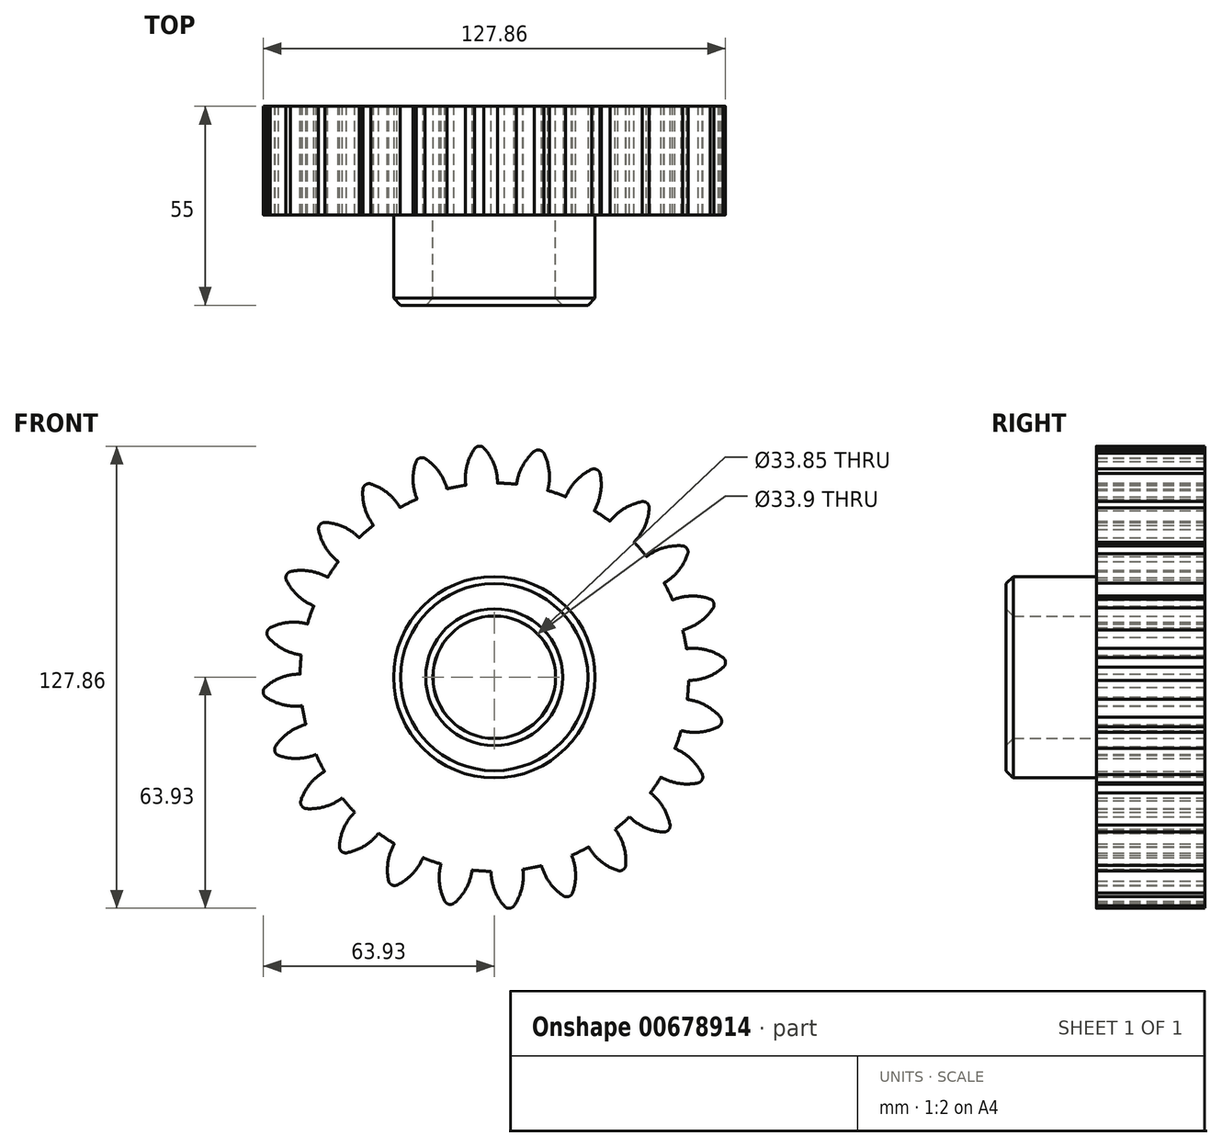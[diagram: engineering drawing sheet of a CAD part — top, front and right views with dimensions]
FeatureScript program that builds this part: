
annotation { "Feature Type Name" : "Feature", "Feature Type Description" : "" }
export const myFeature = defineFeature(function(context is Context, id is Id, definition is map)
    precondition{}
    {
        {
            var Q0;
            Q0=qCreatedBy(makeId("Front.planeOp"),FACE);
            var sketch = newSketch(context, id + "F0", { "sketchPlane" : qUnion([Q0])});
            skCircle(sketch, "E0", {"center": v(0, 0) * mm, "radius": 63.5 * mm, "construction": true});
            skCircle(sketch, "E1", {"center": v(0, 0) * mm, "radius": 58.67 * mm, "construction": true});
            skCircle(sketch, "E2", {"center": v(0, 0) * mm, "radius": 53.72 * mm});
            skLineSegment(sketch, "E3", {"start": v(0, 0) * mm, "end": v(0, 81.95) * mm, "construction": true});
            skLineSegment(sketch, "E4", {"start": v(0, 81.95) * mm, "end": v(0, 0) * mm, "construction": true});
            skLineSegment(sketch, "E5", {"start": v(0, 0) * mm, "end": v(-5.35, 81.6) * mm, "construction": true});
            skLineSegment(sketch, "E6", {"start": v(0, 58.67) * mm, "end": v(-69.28, 58.67) * mm, "construction": true});
            skLineSegment(sketch, "E7", {"start": v(0, 58.67) * mm, "end": v(-66.67, 34.4) * mm, "construction": true});
            skCircle(sketch, "E8", {"center": v(0, 0) * mm, "radius": 55.14 * mm, "construction": true});
            skCircle(sketch, "E9", {"center": v(0, 58.67) * mm, "radius": 14.6 * mm, "construction": true});
            skCircle(sketch, "E10", {"center": v(-13.72, 53.68) * mm, "radius": 14.6 * mm, "construction": true});
            skArc(sketch, "E11", {"start": v(0, 58.67) * mm, "mid": v(-1.2, 61.2) * mm, "end": v(-2.86, 63.44) * mm});
            skArc(sketch, "E12", {"start": v(0.88, 53.71) * mm, "mid": v(0.65, 56.23) * mm, "end": v(0, 58.67) * mm});
            skArc(sketch, "E13.MirrorCS", {"start": v(-7.66, 58.17) * mm, "mid": v(-6.8, 60.82) * mm, "end": v(-5.45, 63.27) * mm});
            skArc(sketch, "E14.MirrorCS", {"start": v(-7.88, 53.14) * mm, "mid": v(-7.99, 55.67) * mm, "end": v(-7.66, 58.17) * mm});
            skArc(sketch, "E15", {"start": v(-2.86, 63.44) * mm, "mid": v(-4.2, 63.93) * mm, "end": v(-5.45, 63.27) * mm});
            skPoint(sketch, "E16.0.midPoint", {"position": v(20.96, 6.95) * mm});
            skCircle(sketch, "E17", {"center": v(0, 0) * mm, "radius": 33.14 * mm});
            skPoint(sketch, "E18.0.midPoint", {"position": v(11.07, -7.08) * mm});
            skCircle(sketch, "E19", {"center": v(0, 0) * mm, "radius": 16.92 * mm});
            skSolve(sketch);
        }
        {
            var Q0;
            Q0=makeQuery(id+"F0.imprint","IMPRINT",FACE,{"disambiguationData":[TD([[makeQuery(id+"F0.imprint","IMPRINT",EDGE,{"derivedFrom":sQuery(id+"F0.wireOp",EDGE,"E17")}),-1.0]])]});
            var Q1;
            Q1=makeQuery(id+"F0.imprint","IMPRINT",FACE,{"disambiguationData":[TD([[makeQuery(id+"F0.imprint","IMPRINT",EDGE,{"derivedFrom":sQuery(id+"F0.wireOp",EDGE,"E17")}),1.0]])]});
            var Q2;
            Q2=makeQuery(id+"F0.imprint","IMPRINT",FACE,{"disambiguationData":[TD([[makeQuery(id+"F0.imprint","IMPRINT",EDGE,{"derivedFrom":sQuery(id+"F0.wireOp",EDGE,"E11")}),1.0]])]});
            extrude(context, id + "F1", {"entities" : qUnion([Q0, Q1, Q2]), "depth" : 30 * mm, "offsetDistance" : 25 * mm});
        }
        {
            var Q0;
            Q0=makeQuery(id+"F1.opExtrude","SWEPT_BODY",BODY,{"disambiguationData":[OSD([sQuery(id+"F0.wireOp",EDGE,"E2"),sQuery(id+"F0.wireOp",EDGE,"E11"),sQuery(id+"F0.wireOp",EDGE,"E12"),sQuery(id+"F0.wireOp",EDGE,"E13.MirrorCS"),sQuery(id+"F0.wireOp",EDGE,"E14.MirrorCS"),sQuery(id+"F0.wireOp",EDGE,"E15")])]});
            var Q1;
            Q1=makeQuery(id+"F1.opExtrude","SWEPT_FACE",FACE,{"disambiguationData":[OSD([sQuery(id+"F0.wireOp",EDGE,"E2")])]});
            circularPattern(context, id + "F2", {"operationType" : NewBodyOperationType.ADD, "entities" : qUnion([Q0]), "axis" : qUnion([Q1]), "angle" : 360 * degree, "instanceCount" : 24, "equalSpace" : true});
        }
        {
            var Q0;
            Q0=makeQuery(id+"F1.opExtrude","CAP_FACE",FACE,{"disambiguationData":[OSD([sQuery(id+"F0.wireOp",EDGE,"E2"),sQuery(id+"F0.wireOp",EDGE,"E11"),sQuery(id+"F0.wireOp",EDGE,"E12"),sQuery(id+"F0.wireOp",EDGE,"E13.MirrorCS"),sQuery(id+"F0.wireOp",EDGE,"E14.MirrorCS"),sQuery(id+"F0.wireOp",EDGE,"E15"),sQuery(id+"F0.wireOp",EDGE,"E16.0"),sQuery(id+"F0.wireOp",EDGE,"E16.1"),sQuery(id+"F0.wireOp",EDGE,"E16.2"),sQuery(id+"F0.wireOp",EDGE,"E16.3"),sQuery(id+"F0.wireOp",EDGE,"E16.4")])],"isStart":false});
            fillet(context, id + "F3", {"entities" : qUnion([Q0]), "radius" : 0.02 * mm, "tangentPropagation" : true, "allowEdgeOverflow" : false});
        }
        {
            var Q0;
            {var subQ0=makeQuery(id+"F1.opExtrude","CAP_FACE",FACE,{"disambiguationData":[OSD([sQuery(id+"F0.wireOp",EDGE,"E2"),sQuery(id+"F0.wireOp",EDGE,"E11"),sQuery(id+"F0.wireOp",EDGE,"E12"),sQuery(id+"F0.wireOp",EDGE,"E13.MirrorCS"),sQuery(id+"F0.wireOp",EDGE,"E14.MirrorCS"),sQuery(id+"F0.wireOp",EDGE,"E15"),sQuery(id+"F0.wireOp",EDGE,"E18.0"),sQuery(id+"F0.wireOp",EDGE,"E18.1"),sQuery(id+"F0.wireOp",EDGE,"E18.2"),sQuery(id+"F0.wireOp",EDGE,"E18.3"),sQuery(id+"F0.wireOp",EDGE,"E18.4"),sQuery(id+"F0.wireOp",EDGE,"E18.5")])],"isStart":false});Q0=makeQuery(id+"F2.boolean.opBoolean","MERGE",FACE,{"derivedFrom":[subQ0,makeQuery(id+"F2.opPattern","COPY",FACE,{"derivedFrom":subQ0,"instanceName":"1"}),makeQuery(id+"F2.opPattern","COPY",FACE,{"derivedFrom":subQ0,"instanceName":"2"}),makeQuery(id+"F2.opPattern","COPY",FACE,{"derivedFrom":subQ0,"instanceName":"3"}),makeQuery(id+"F2.opPattern","COPY",FACE,{"derivedFrom":subQ0,"instanceName":"4"}),makeQuery(id+"F2.opPattern","COPY",FACE,{"derivedFrom":subQ0,"instanceName":"5"}),makeQuery(id+"F2.opPattern","COPY",FACE,{"derivedFrom":subQ0,"instanceName":"6"}),makeQuery(id+"F2.opPattern","COPY",FACE,{"derivedFrom":subQ0,"instanceName":"7"}),makeQuery(id+"F2.opPattern","COPY",FACE,{"derivedFrom":subQ0,"instanceName":"8"}),makeQuery(id+"F2.opPattern","COPY",FACE,{"derivedFrom":subQ0,"instanceName":"9"}),makeQuery(id+"F2.opPattern","COPY",FACE,{"derivedFrom":subQ0,"instanceName":"10"}),makeQuery(id+"F2.opPattern","COPY",FACE,{"derivedFrom":subQ0,"instanceName":"11"}),makeQuery(id+"F2.opPattern","COPY",FACE,{"derivedFrom":subQ0,"instanceName":"12"}),makeQuery(id+"F2.opPattern","COPY",FACE,{"derivedFrom":subQ0,"instanceName":"13"}),makeQuery(id+"F2.opPattern","COPY",FACE,{"derivedFrom":subQ0,"instanceName":"14"}),makeQuery(id+"F2.opPattern","COPY",FACE,{"derivedFrom":subQ0,"instanceName":"15"}),makeQuery(id+"F2.opPattern","COPY",FACE,{"derivedFrom":subQ0,"instanceName":"16"}),makeQuery(id+"F2.opPattern","COPY",FACE,{"derivedFrom":subQ0,"instanceName":"17"}),makeQuery(id+"F2.opPattern","COPY",FACE,{"derivedFrom":subQ0,"instanceName":"18"}),makeQuery(id+"F2.opPattern","COPY",FACE,{"derivedFrom":subQ0,"instanceName":"19"}),makeQuery(id+"F2.opPattern","COPY",FACE,{"derivedFrom":subQ0,"instanceName":"20"}),makeQuery(id+"F2.opPattern","COPY",FACE,{"derivedFrom":subQ0,"instanceName":"21"}),makeQuery(id+"F2.opPattern","COPY",FACE,{"derivedFrom":subQ0,"instanceName":"22"}),makeQuery(id+"F2.opPattern","COPY",FACE,{"derivedFrom":subQ0,"instanceName":"23"})]});}
            var sketch = newSketch(context, id + "F4", { "sketchPlane" : qUnion([Q0])});
            skCircle(sketch, "E20", {"center": v(0, 0) * mm, "radius": 27.86 * mm});
            skSolve(sketch);
        }
        {
            var Q0;
            Q0=makeQuery(id+"F4.imprint","IMPRINT",FACE,{"disambiguationData":[TD([[makeQuery(id+"F4.imprint","IMPRINT",EDGE,{"derivedFrom":sQuery(id+"F4.wireOp",EDGE,"E20")}),1.0]])]});
            extrude(context, id + "F5", {"entities" : qUnion([Q0]), "operationType" : NewBodyOperationType.ADD, "depth" : 25 * mm, "offsetDistance" : 25 * mm});
        }
        {
            var Q0;
            Q0=makeQuery(id+"F5.opExtrude","CAP_EDGE",EDGE,{"disambiguationData":[OSD([sQuery(id+"F4.wireOp",EDGE,"E20")])],"isStart":false});
            var Q1;
            Q1=makeQuery(id+"F5.opExtrude","CAP_EDGE",EDGE,{"disambiguationData":[OSD([sQuery(id+"F0.wireOp",EDGE,"E2"),sQuery(id+"F0.wireOp",EDGE,"E11"),sQuery(id+"F0.wireOp",EDGE,"E12"),sQuery(id+"F0.wireOp",EDGE,"E13.MirrorCS"),sQuery(id+"F0.wireOp",EDGE,"E14.MirrorCS"),sQuery(id+"F0.wireOp",EDGE,"E15"),sQuery(id+"F0.wireOp",EDGE,"E19")])],"isStart":false});
            var Q2;
            {var subQ0=sQuery(id+"F0.wireOp",EDGE,"E14.MirrorCS");var subQ1=makeQuery(id+"F1.opExtrude","CAP_FACE",FACE,{"disambiguationData":[OSD([sQuery(id+"F0.wireOp",EDGE,"E2"),sQuery(id+"F0.wireOp",EDGE,"E11"),sQuery(id+"F0.wireOp",EDGE,"E12"),sQuery(id+"F0.wireOp",EDGE,"E13.MirrorCS"),subQ0,sQuery(id+"F0.wireOp",EDGE,"E15"),sQuery(id+"F0.wireOp",EDGE,"E19")])],"isStart":false});Q2=makeQuery(id+"F3.opFillet","BLEND_EDGE",EDGE,{"blendedFrom":[makeQuery(id+"F1.opExtrude","CAP_EDGE",EDGE,{"disambiguationData":[OSD([subQ0])],"isStart":false}),makeQuery(id+"F2.boolean.opBoolean","MERGE",FACE,{"derivedFrom":[subQ1,makeQuery(id+"F2.opPattern","COPY",FACE,{"derivedFrom":subQ1,"instanceName":"1"}),makeQuery(id+"F2.opPattern","COPY",FACE,{"derivedFrom":subQ1,"instanceName":"2"}),makeQuery(id+"F2.opPattern","COPY",FACE,{"derivedFrom":subQ1,"instanceName":"3"}),makeQuery(id+"F2.opPattern","COPY",FACE,{"derivedFrom":subQ1,"instanceName":"4"}),makeQuery(id+"F2.opPattern","COPY",FACE,{"derivedFrom":subQ1,"instanceName":"5"}),makeQuery(id+"F2.opPattern","COPY",FACE,{"derivedFrom":subQ1,"instanceName":"6"}),makeQuery(id+"F2.opPattern","COPY",FACE,{"derivedFrom":subQ1,"instanceName":"7"}),makeQuery(id+"F2.opPattern","COPY",FACE,{"derivedFrom":subQ1,"instanceName":"8"}),makeQuery(id+"F2.opPattern","COPY",FACE,{"derivedFrom":subQ1,"instanceName":"9"}),makeQuery(id+"F2.opPattern","COPY",FACE,{"derivedFrom":subQ1,"instanceName":"10"}),makeQuery(id+"F2.opPattern","COPY",FACE,{"derivedFrom":subQ1,"instanceName":"11"}),makeQuery(id+"F2.opPattern","COPY",FACE,{"derivedFrom":subQ1,"instanceName":"12"}),makeQuery(id+"F2.opPattern","COPY",FACE,{"derivedFrom":subQ1,"instanceName":"13"}),makeQuery(id+"F2.opPattern","COPY",FACE,{"derivedFrom":subQ1,"instanceName":"14"}),makeQuery(id+"F2.opPattern","COPY",FACE,{"derivedFrom":subQ1,"instanceName":"15"}),makeQuery(id+"F2.opPattern","COPY",FACE,{"derivedFrom":subQ1,"instanceName":"16"}),makeQuery(id+"F2.opPattern","COPY",FACE,{"derivedFrom":subQ1,"instanceName":"17"}),makeQuery(id+"F2.opPattern","COPY",FACE,{"derivedFrom":subQ1,"instanceName":"18"}),makeQuery(id+"F2.opPattern","COPY",FACE,{"derivedFrom":subQ1,"instanceName":"19"}),makeQuery(id+"F2.opPattern","COPY",FACE,{"derivedFrom":subQ1,"instanceName":"20"}),makeQuery(id+"F2.opPattern","COPY",FACE,{"derivedFrom":subQ1,"instanceName":"21"}),makeQuery(id+"F2.opPattern","COPY",FACE,{"derivedFrom":subQ1,"instanceName":"22"}),makeQuery(id+"F2.opPattern","COPY",FACE,{"derivedFrom":subQ1,"instanceName":"23"})]})],"blendedInto":[makeQuery(id+"F2.boolean.opBoolean","MERGE",FACE,{"derivedFrom":[subQ1,makeQuery(id+"F2.opPattern","COPY",FACE,{"derivedFrom":subQ1,"instanceName":"1"}),makeQuery(id+"F2.opPattern","COPY",FACE,{"derivedFrom":subQ1,"instanceName":"2"}),makeQuery(id+"F2.opPattern","COPY",FACE,{"derivedFrom":subQ1,"instanceName":"3"}),makeQuery(id+"F2.opPattern","COPY",FACE,{"derivedFrom":subQ1,"instanceName":"4"}),makeQuery(id+"F2.opPattern","COPY",FACE,{"derivedFrom":subQ1,"instanceName":"5"}),makeQuery(id+"F2.opPattern","COPY",FACE,{"derivedFrom":subQ1,"instanceName":"6"}),makeQuery(id+"F2.opPattern","COPY",FACE,{"derivedFrom":subQ1,"instanceName":"7"}),makeQuery(id+"F2.opPattern","COPY",FACE,{"derivedFrom":subQ1,"instanceName":"8"}),makeQuery(id+"F2.opPattern","COPY",FACE,{"derivedFrom":subQ1,"instanceName":"9"}),makeQuery(id+"F2.opPattern","COPY",FACE,{"derivedFrom":subQ1,"instanceName":"10"}),makeQuery(id+"F2.opPattern","COPY",FACE,{"derivedFrom":subQ1,"instanceName":"11"}),makeQuery(id+"F2.opPattern","COPY",FACE,{"derivedFrom":subQ1,"instanceName":"12"}),makeQuery(id+"F2.opPattern","COPY",FACE,{"derivedFrom":subQ1,"instanceName":"13"}),makeQuery(id+"F2.opPattern","COPY",FACE,{"derivedFrom":subQ1,"instanceName":"14"}),makeQuery(id+"F2.opPattern","COPY",FACE,{"derivedFrom":subQ1,"instanceName":"15"}),makeQuery(id+"F2.opPattern","COPY",FACE,{"derivedFrom":subQ1,"instanceName":"16"}),makeQuery(id+"F2.opPattern","COPY",FACE,{"derivedFrom":subQ1,"instanceName":"17"}),makeQuery(id+"F2.opPattern","COPY",FACE,{"derivedFrom":subQ1,"instanceName":"18"}),makeQuery(id+"F2.opPattern","COPY",FACE,{"derivedFrom":subQ1,"instanceName":"19"}),makeQuery(id+"F2.opPattern","COPY",FACE,{"derivedFrom":subQ1,"instanceName":"20"}),makeQuery(id+"F2.opPattern","COPY",FACE,{"derivedFrom":subQ1,"instanceName":"21"}),makeQuery(id+"F2.opPattern","COPY",FACE,{"derivedFrom":subQ1,"instanceName":"22"}),makeQuery(id+"F2.opPattern","COPY",FACE,{"derivedFrom":subQ1,"instanceName":"23"})]})]});}
            var Q3;
            {var subQ0=sQuery(id+"F0.wireOp",EDGE,"E12");var subQ1=makeQuery(id+"F1.opExtrude","CAP_FACE",FACE,{"disambiguationData":[OSD([sQuery(id+"F0.wireOp",EDGE,"E2"),sQuery(id+"F0.wireOp",EDGE,"E11"),subQ0,sQuery(id+"F0.wireOp",EDGE,"E13.MirrorCS"),sQuery(id+"F0.wireOp",EDGE,"E14.MirrorCS"),sQuery(id+"F0.wireOp",EDGE,"E15"),sQuery(id+"F0.wireOp",EDGE,"E19")])],"isStart":false});Q3=makeQuery(id+"F3.opFillet","BLEND_EDGE",EDGE,{"blendedFrom":[makeQuery(id+"F1.opExtrude","CAP_EDGE",EDGE,{"disambiguationData":[OSD([subQ0])],"isStart":false}),makeQuery(id+"F2.boolean.opBoolean","MERGE",FACE,{"derivedFrom":[subQ1,makeQuery(id+"F2.opPattern","COPY",FACE,{"derivedFrom":subQ1,"instanceName":"1"}),makeQuery(id+"F2.opPattern","COPY",FACE,{"derivedFrom":subQ1,"instanceName":"2"}),makeQuery(id+"F2.opPattern","COPY",FACE,{"derivedFrom":subQ1,"instanceName":"3"}),makeQuery(id+"F2.opPattern","COPY",FACE,{"derivedFrom":subQ1,"instanceName":"4"}),makeQuery(id+"F2.opPattern","COPY",FACE,{"derivedFrom":subQ1,"instanceName":"5"}),makeQuery(id+"F2.opPattern","COPY",FACE,{"derivedFrom":subQ1,"instanceName":"6"}),makeQuery(id+"F2.opPattern","COPY",FACE,{"derivedFrom":subQ1,"instanceName":"7"}),makeQuery(id+"F2.opPattern","COPY",FACE,{"derivedFrom":subQ1,"instanceName":"8"}),makeQuery(id+"F2.opPattern","COPY",FACE,{"derivedFrom":subQ1,"instanceName":"9"}),makeQuery(id+"F2.opPattern","COPY",FACE,{"derivedFrom":subQ1,"instanceName":"10"}),makeQuery(id+"F2.opPattern","COPY",FACE,{"derivedFrom":subQ1,"instanceName":"11"}),makeQuery(id+"F2.opPattern","COPY",FACE,{"derivedFrom":subQ1,"instanceName":"12"}),makeQuery(id+"F2.opPattern","COPY",FACE,{"derivedFrom":subQ1,"instanceName":"13"}),makeQuery(id+"F2.opPattern","COPY",FACE,{"derivedFrom":subQ1,"instanceName":"14"}),makeQuery(id+"F2.opPattern","COPY",FACE,{"derivedFrom":subQ1,"instanceName":"15"}),makeQuery(id+"F2.opPattern","COPY",FACE,{"derivedFrom":subQ1,"instanceName":"16"}),makeQuery(id+"F2.opPattern","COPY",FACE,{"derivedFrom":subQ1,"instanceName":"17"}),makeQuery(id+"F2.opPattern","COPY",FACE,{"derivedFrom":subQ1,"instanceName":"18"}),makeQuery(id+"F2.opPattern","COPY",FACE,{"derivedFrom":subQ1,"instanceName":"19"}),makeQuery(id+"F2.opPattern","COPY",FACE,{"derivedFrom":subQ1,"instanceName":"20"}),makeQuery(id+"F2.opPattern","COPY",FACE,{"derivedFrom":subQ1,"instanceName":"21"}),makeQuery(id+"F2.opPattern","COPY",FACE,{"derivedFrom":subQ1,"instanceName":"22"}),makeQuery(id+"F2.opPattern","COPY",FACE,{"derivedFrom":subQ1,"instanceName":"23"})]})],"blendedInto":[makeQuery(id+"F2.boolean.opBoolean","MERGE",FACE,{"derivedFrom":[subQ1,makeQuery(id+"F2.opPattern","COPY",FACE,{"derivedFrom":subQ1,"instanceName":"1"}),makeQuery(id+"F2.opPattern","COPY",FACE,{"derivedFrom":subQ1,"instanceName":"2"}),makeQuery(id+"F2.opPattern","COPY",FACE,{"derivedFrom":subQ1,"instanceName":"3"}),makeQuery(id+"F2.opPattern","COPY",FACE,{"derivedFrom":subQ1,"instanceName":"4"}),makeQuery(id+"F2.opPattern","COPY",FACE,{"derivedFrom":subQ1,"instanceName":"5"}),makeQuery(id+"F2.opPattern","COPY",FACE,{"derivedFrom":subQ1,"instanceName":"6"}),makeQuery(id+"F2.opPattern","COPY",FACE,{"derivedFrom":subQ1,"instanceName":"7"}),makeQuery(id+"F2.opPattern","COPY",FACE,{"derivedFrom":subQ1,"instanceName":"8"}),makeQuery(id+"F2.opPattern","COPY",FACE,{"derivedFrom":subQ1,"instanceName":"9"}),makeQuery(id+"F2.opPattern","COPY",FACE,{"derivedFrom":subQ1,"instanceName":"10"}),makeQuery(id+"F2.opPattern","COPY",FACE,{"derivedFrom":subQ1,"instanceName":"11"}),makeQuery(id+"F2.opPattern","COPY",FACE,{"derivedFrom":subQ1,"instanceName":"12"}),makeQuery(id+"F2.opPattern","COPY",FACE,{"derivedFrom":subQ1,"instanceName":"13"}),makeQuery(id+"F2.opPattern","COPY",FACE,{"derivedFrom":subQ1,"instanceName":"14"}),makeQuery(id+"F2.opPattern","COPY",FACE,{"derivedFrom":subQ1,"instanceName":"15"}),makeQuery(id+"F2.opPattern","COPY",FACE,{"derivedFrom":subQ1,"instanceName":"16"}),makeQuery(id+"F2.opPattern","COPY",FACE,{"derivedFrom":subQ1,"instanceName":"17"}),makeQuery(id+"F2.opPattern","COPY",FACE,{"derivedFrom":subQ1,"instanceName":"18"}),makeQuery(id+"F2.opPattern","COPY",FACE,{"derivedFrom":subQ1,"instanceName":"19"}),makeQuery(id+"F2.opPattern","COPY",FACE,{"derivedFrom":subQ1,"instanceName":"20"}),makeQuery(id+"F2.opPattern","COPY",FACE,{"derivedFrom":subQ1,"instanceName":"21"}),makeQuery(id+"F2.opPattern","COPY",FACE,{"derivedFrom":subQ1,"instanceName":"22"}),makeQuery(id+"F2.opPattern","COPY",FACE,{"derivedFrom":subQ1,"instanceName":"23"})]})]});}
            var Q4;
            {var subQ0=sQuery(id+"F0.wireOp",EDGE,"E14.MirrorCS");var subQ1=makeQuery(id+"F1.opExtrude","CAP_FACE",FACE,{"disambiguationData":[OSD([sQuery(id+"F0.wireOp",EDGE,"E2"),sQuery(id+"F0.wireOp",EDGE,"E11"),sQuery(id+"F0.wireOp",EDGE,"E12"),sQuery(id+"F0.wireOp",EDGE,"E13.MirrorCS"),subQ0,sQuery(id+"F0.wireOp",EDGE,"E15"),sQuery(id+"F0.wireOp",EDGE,"E19")])],"isStart":false});Q4=makeQuery(id+"F3.opFillet","BLEND_EDGE",EDGE,{"blendedFrom":[makeQuery(id+"F2.opPattern","COPY",EDGE,{"derivedFrom":makeQuery(id+"F1.opExtrude","CAP_EDGE",EDGE,{"disambiguationData":[OSD([subQ0])],"isStart":false}),"instanceName":"1"}),makeQuery(id+"F2.boolean.opBoolean","MERGE",FACE,{"derivedFrom":[subQ1,makeQuery(id+"F2.opPattern","COPY",FACE,{"derivedFrom":subQ1,"instanceName":"1"}),makeQuery(id+"F2.opPattern","COPY",FACE,{"derivedFrom":subQ1,"instanceName":"2"}),makeQuery(id+"F2.opPattern","COPY",FACE,{"derivedFrom":subQ1,"instanceName":"3"}),makeQuery(id+"F2.opPattern","COPY",FACE,{"derivedFrom":subQ1,"instanceName":"4"}),makeQuery(id+"F2.opPattern","COPY",FACE,{"derivedFrom":subQ1,"instanceName":"5"}),makeQuery(id+"F2.opPattern","COPY",FACE,{"derivedFrom":subQ1,"instanceName":"6"}),makeQuery(id+"F2.opPattern","COPY",FACE,{"derivedFrom":subQ1,"instanceName":"7"}),makeQuery(id+"F2.opPattern","COPY",FACE,{"derivedFrom":subQ1,"instanceName":"8"}),makeQuery(id+"F2.opPattern","COPY",FACE,{"derivedFrom":subQ1,"instanceName":"9"}),makeQuery(id+"F2.opPattern","COPY",FACE,{"derivedFrom":subQ1,"instanceName":"10"}),makeQuery(id+"F2.opPattern","COPY",FACE,{"derivedFrom":subQ1,"instanceName":"11"}),makeQuery(id+"F2.opPattern","COPY",FACE,{"derivedFrom":subQ1,"instanceName":"12"}),makeQuery(id+"F2.opPattern","COPY",FACE,{"derivedFrom":subQ1,"instanceName":"13"}),makeQuery(id+"F2.opPattern","COPY",FACE,{"derivedFrom":subQ1,"instanceName":"14"}),makeQuery(id+"F2.opPattern","COPY",FACE,{"derivedFrom":subQ1,"instanceName":"15"}),makeQuery(id+"F2.opPattern","COPY",FACE,{"derivedFrom":subQ1,"instanceName":"16"}),makeQuery(id+"F2.opPattern","COPY",FACE,{"derivedFrom":subQ1,"instanceName":"17"}),makeQuery(id+"F2.opPattern","COPY",FACE,{"derivedFrom":subQ1,"instanceName":"18"}),makeQuery(id+"F2.opPattern","COPY",FACE,{"derivedFrom":subQ1,"instanceName":"19"}),makeQuery(id+"F2.opPattern","COPY",FACE,{"derivedFrom":subQ1,"instanceName":"20"}),makeQuery(id+"F2.opPattern","COPY",FACE,{"derivedFrom":subQ1,"instanceName":"21"}),makeQuery(id+"F2.opPattern","COPY",FACE,{"derivedFrom":subQ1,"instanceName":"22"}),makeQuery(id+"F2.opPattern","COPY",FACE,{"derivedFrom":subQ1,"instanceName":"23"})]})],"blendedInto":[makeQuery(id+"F2.boolean.opBoolean","MERGE",FACE,{"derivedFrom":[subQ1,makeQuery(id+"F2.opPattern","COPY",FACE,{"derivedFrom":subQ1,"instanceName":"1"}),makeQuery(id+"F2.opPattern","COPY",FACE,{"derivedFrom":subQ1,"instanceName":"2"}),makeQuery(id+"F2.opPattern","COPY",FACE,{"derivedFrom":subQ1,"instanceName":"3"}),makeQuery(id+"F2.opPattern","COPY",FACE,{"derivedFrom":subQ1,"instanceName":"4"}),makeQuery(id+"F2.opPattern","COPY",FACE,{"derivedFrom":subQ1,"instanceName":"5"}),makeQuery(id+"F2.opPattern","COPY",FACE,{"derivedFrom":subQ1,"instanceName":"6"}),makeQuery(id+"F2.opPattern","COPY",FACE,{"derivedFrom":subQ1,"instanceName":"7"}),makeQuery(id+"F2.opPattern","COPY",FACE,{"derivedFrom":subQ1,"instanceName":"8"}),makeQuery(id+"F2.opPattern","COPY",FACE,{"derivedFrom":subQ1,"instanceName":"9"}),makeQuery(id+"F2.opPattern","COPY",FACE,{"derivedFrom":subQ1,"instanceName":"10"}),makeQuery(id+"F2.opPattern","COPY",FACE,{"derivedFrom":subQ1,"instanceName":"11"}),makeQuery(id+"F2.opPattern","COPY",FACE,{"derivedFrom":subQ1,"instanceName":"12"}),makeQuery(id+"F2.opPattern","COPY",FACE,{"derivedFrom":subQ1,"instanceName":"13"}),makeQuery(id+"F2.opPattern","COPY",FACE,{"derivedFrom":subQ1,"instanceName":"14"}),makeQuery(id+"F2.opPattern","COPY",FACE,{"derivedFrom":subQ1,"instanceName":"15"}),makeQuery(id+"F2.opPattern","COPY",FACE,{"derivedFrom":subQ1,"instanceName":"16"}),makeQuery(id+"F2.opPattern","COPY",FACE,{"derivedFrom":subQ1,"instanceName":"17"}),makeQuery(id+"F2.opPattern","COPY",FACE,{"derivedFrom":subQ1,"instanceName":"18"}),makeQuery(id+"F2.opPattern","COPY",FACE,{"derivedFrom":subQ1,"instanceName":"19"}),makeQuery(id+"F2.opPattern","COPY",FACE,{"derivedFrom":subQ1,"instanceName":"20"}),makeQuery(id+"F2.opPattern","COPY",FACE,{"derivedFrom":subQ1,"instanceName":"21"}),makeQuery(id+"F2.opPattern","COPY",FACE,{"derivedFrom":subQ1,"instanceName":"22"}),makeQuery(id+"F2.opPattern","COPY",FACE,{"derivedFrom":subQ1,"instanceName":"23"})]})]});}
            var Q5;
            {var subQ0=sQuery(id+"F0.wireOp",EDGE,"E12");var subQ1=makeQuery(id+"F1.opExtrude","CAP_FACE",FACE,{"disambiguationData":[OSD([sQuery(id+"F0.wireOp",EDGE,"E2"),sQuery(id+"F0.wireOp",EDGE,"E11"),subQ0,sQuery(id+"F0.wireOp",EDGE,"E13.MirrorCS"),sQuery(id+"F0.wireOp",EDGE,"E14.MirrorCS"),sQuery(id+"F0.wireOp",EDGE,"E15"),sQuery(id+"F0.wireOp",EDGE,"E19")])],"isStart":false});Q5=makeQuery(id+"F3.opFillet","BLEND_EDGE",EDGE,{"blendedFrom":[makeQuery(id+"F2.opPattern","COPY",EDGE,{"derivedFrom":makeQuery(id+"F1.opExtrude","CAP_EDGE",EDGE,{"disambiguationData":[OSD([subQ0])],"isStart":false}),"instanceName":"1"}),makeQuery(id+"F2.boolean.opBoolean","MERGE",FACE,{"derivedFrom":[subQ1,makeQuery(id+"F2.opPattern","COPY",FACE,{"derivedFrom":subQ1,"instanceName":"1"}),makeQuery(id+"F2.opPattern","COPY",FACE,{"derivedFrom":subQ1,"instanceName":"2"}),makeQuery(id+"F2.opPattern","COPY",FACE,{"derivedFrom":subQ1,"instanceName":"3"}),makeQuery(id+"F2.opPattern","COPY",FACE,{"derivedFrom":subQ1,"instanceName":"4"}),makeQuery(id+"F2.opPattern","COPY",FACE,{"derivedFrom":subQ1,"instanceName":"5"}),makeQuery(id+"F2.opPattern","COPY",FACE,{"derivedFrom":subQ1,"instanceName":"6"}),makeQuery(id+"F2.opPattern","COPY",FACE,{"derivedFrom":subQ1,"instanceName":"7"}),makeQuery(id+"F2.opPattern","COPY",FACE,{"derivedFrom":subQ1,"instanceName":"8"}),makeQuery(id+"F2.opPattern","COPY",FACE,{"derivedFrom":subQ1,"instanceName":"9"}),makeQuery(id+"F2.opPattern","COPY",FACE,{"derivedFrom":subQ1,"instanceName":"10"}),makeQuery(id+"F2.opPattern","COPY",FACE,{"derivedFrom":subQ1,"instanceName":"11"}),makeQuery(id+"F2.opPattern","COPY",FACE,{"derivedFrom":subQ1,"instanceName":"12"}),makeQuery(id+"F2.opPattern","COPY",FACE,{"derivedFrom":subQ1,"instanceName":"13"}),makeQuery(id+"F2.opPattern","COPY",FACE,{"derivedFrom":subQ1,"instanceName":"14"}),makeQuery(id+"F2.opPattern","COPY",FACE,{"derivedFrom":subQ1,"instanceName":"15"}),makeQuery(id+"F2.opPattern","COPY",FACE,{"derivedFrom":subQ1,"instanceName":"16"}),makeQuery(id+"F2.opPattern","COPY",FACE,{"derivedFrom":subQ1,"instanceName":"17"}),makeQuery(id+"F2.opPattern","COPY",FACE,{"derivedFrom":subQ1,"instanceName":"18"}),makeQuery(id+"F2.opPattern","COPY",FACE,{"derivedFrom":subQ1,"instanceName":"19"}),makeQuery(id+"F2.opPattern","COPY",FACE,{"derivedFrom":subQ1,"instanceName":"20"}),makeQuery(id+"F2.opPattern","COPY",FACE,{"derivedFrom":subQ1,"instanceName":"21"}),makeQuery(id+"F2.opPattern","COPY",FACE,{"derivedFrom":subQ1,"instanceName":"22"}),makeQuery(id+"F2.opPattern","COPY",FACE,{"derivedFrom":subQ1,"instanceName":"23"})]})],"blendedInto":[makeQuery(id+"F2.boolean.opBoolean","MERGE",FACE,{"derivedFrom":[subQ1,makeQuery(id+"F2.opPattern","COPY",FACE,{"derivedFrom":subQ1,"instanceName":"1"}),makeQuery(id+"F2.opPattern","COPY",FACE,{"derivedFrom":subQ1,"instanceName":"2"}),makeQuery(id+"F2.opPattern","COPY",FACE,{"derivedFrom":subQ1,"instanceName":"3"}),makeQuery(id+"F2.opPattern","COPY",FACE,{"derivedFrom":subQ1,"instanceName":"4"}),makeQuery(id+"F2.opPattern","COPY",FACE,{"derivedFrom":subQ1,"instanceName":"5"}),makeQuery(id+"F2.opPattern","COPY",FACE,{"derivedFrom":subQ1,"instanceName":"6"}),makeQuery(id+"F2.opPattern","COPY",FACE,{"derivedFrom":subQ1,"instanceName":"7"}),makeQuery(id+"F2.opPattern","COPY",FACE,{"derivedFrom":subQ1,"instanceName":"8"}),makeQuery(id+"F2.opPattern","COPY",FACE,{"derivedFrom":subQ1,"instanceName":"9"}),makeQuery(id+"F2.opPattern","COPY",FACE,{"derivedFrom":subQ1,"instanceName":"10"}),makeQuery(id+"F2.opPattern","COPY",FACE,{"derivedFrom":subQ1,"instanceName":"11"}),makeQuery(id+"F2.opPattern","COPY",FACE,{"derivedFrom":subQ1,"instanceName":"12"}),makeQuery(id+"F2.opPattern","COPY",FACE,{"derivedFrom":subQ1,"instanceName":"13"}),makeQuery(id+"F2.opPattern","COPY",FACE,{"derivedFrom":subQ1,"instanceName":"14"}),makeQuery(id+"F2.opPattern","COPY",FACE,{"derivedFrom":subQ1,"instanceName":"15"}),makeQuery(id+"F2.opPattern","COPY",FACE,{"derivedFrom":subQ1,"instanceName":"16"}),makeQuery(id+"F2.opPattern","COPY",FACE,{"derivedFrom":subQ1,"instanceName":"17"}),makeQuery(id+"F2.opPattern","COPY",FACE,{"derivedFrom":subQ1,"instanceName":"18"}),makeQuery(id+"F2.opPattern","COPY",FACE,{"derivedFrom":subQ1,"instanceName":"19"}),makeQuery(id+"F2.opPattern","COPY",FACE,{"derivedFrom":subQ1,"instanceName":"20"}),makeQuery(id+"F2.opPattern","COPY",FACE,{"derivedFrom":subQ1,"instanceName":"21"}),makeQuery(id+"F2.opPattern","COPY",FACE,{"derivedFrom":subQ1,"instanceName":"22"}),makeQuery(id+"F2.opPattern","COPY",FACE,{"derivedFrom":subQ1,"instanceName":"23"})]})]});}
            var Q6;
            {var subQ0=sQuery(id+"F0.wireOp",EDGE,"E14.MirrorCS");var subQ1=makeQuery(id+"F1.opExtrude","CAP_FACE",FACE,{"disambiguationData":[OSD([sQuery(id+"F0.wireOp",EDGE,"E2"),sQuery(id+"F0.wireOp",EDGE,"E11"),sQuery(id+"F0.wireOp",EDGE,"E12"),sQuery(id+"F0.wireOp",EDGE,"E13.MirrorCS"),subQ0,sQuery(id+"F0.wireOp",EDGE,"E15"),sQuery(id+"F0.wireOp",EDGE,"E19")])],"isStart":false});Q6=makeQuery(id+"F3.opFillet","BLEND_EDGE",EDGE,{"blendedFrom":[makeQuery(id+"F2.opPattern","COPY",EDGE,{"derivedFrom":makeQuery(id+"F1.opExtrude","CAP_EDGE",EDGE,{"disambiguationData":[OSD([subQ0])],"isStart":false}),"instanceName":"2"}),makeQuery(id+"F2.boolean.opBoolean","MERGE",FACE,{"derivedFrom":[subQ1,makeQuery(id+"F2.opPattern","COPY",FACE,{"derivedFrom":subQ1,"instanceName":"1"}),makeQuery(id+"F2.opPattern","COPY",FACE,{"derivedFrom":subQ1,"instanceName":"2"}),makeQuery(id+"F2.opPattern","COPY",FACE,{"derivedFrom":subQ1,"instanceName":"3"}),makeQuery(id+"F2.opPattern","COPY",FACE,{"derivedFrom":subQ1,"instanceName":"4"}),makeQuery(id+"F2.opPattern","COPY",FACE,{"derivedFrom":subQ1,"instanceName":"5"}),makeQuery(id+"F2.opPattern","COPY",FACE,{"derivedFrom":subQ1,"instanceName":"6"}),makeQuery(id+"F2.opPattern","COPY",FACE,{"derivedFrom":subQ1,"instanceName":"7"}),makeQuery(id+"F2.opPattern","COPY",FACE,{"derivedFrom":subQ1,"instanceName":"8"}),makeQuery(id+"F2.opPattern","COPY",FACE,{"derivedFrom":subQ1,"instanceName":"9"}),makeQuery(id+"F2.opPattern","COPY",FACE,{"derivedFrom":subQ1,"instanceName":"10"}),makeQuery(id+"F2.opPattern","COPY",FACE,{"derivedFrom":subQ1,"instanceName":"11"}),makeQuery(id+"F2.opPattern","COPY",FACE,{"derivedFrom":subQ1,"instanceName":"12"}),makeQuery(id+"F2.opPattern","COPY",FACE,{"derivedFrom":subQ1,"instanceName":"13"}),makeQuery(id+"F2.opPattern","COPY",FACE,{"derivedFrom":subQ1,"instanceName":"14"}),makeQuery(id+"F2.opPattern","COPY",FACE,{"derivedFrom":subQ1,"instanceName":"15"}),makeQuery(id+"F2.opPattern","COPY",FACE,{"derivedFrom":subQ1,"instanceName":"16"}),makeQuery(id+"F2.opPattern","COPY",FACE,{"derivedFrom":subQ1,"instanceName":"17"}),makeQuery(id+"F2.opPattern","COPY",FACE,{"derivedFrom":subQ1,"instanceName":"18"}),makeQuery(id+"F2.opPattern","COPY",FACE,{"derivedFrom":subQ1,"instanceName":"19"}),makeQuery(id+"F2.opPattern","COPY",FACE,{"derivedFrom":subQ1,"instanceName":"20"}),makeQuery(id+"F2.opPattern","COPY",FACE,{"derivedFrom":subQ1,"instanceName":"21"}),makeQuery(id+"F2.opPattern","COPY",FACE,{"derivedFrom":subQ1,"instanceName":"22"}),makeQuery(id+"F2.opPattern","COPY",FACE,{"derivedFrom":subQ1,"instanceName":"23"})]})],"blendedInto":[makeQuery(id+"F2.boolean.opBoolean","MERGE",FACE,{"derivedFrom":[subQ1,makeQuery(id+"F2.opPattern","COPY",FACE,{"derivedFrom":subQ1,"instanceName":"1"}),makeQuery(id+"F2.opPattern","COPY",FACE,{"derivedFrom":subQ1,"instanceName":"2"}),makeQuery(id+"F2.opPattern","COPY",FACE,{"derivedFrom":subQ1,"instanceName":"3"}),makeQuery(id+"F2.opPattern","COPY",FACE,{"derivedFrom":subQ1,"instanceName":"4"}),makeQuery(id+"F2.opPattern","COPY",FACE,{"derivedFrom":subQ1,"instanceName":"5"}),makeQuery(id+"F2.opPattern","COPY",FACE,{"derivedFrom":subQ1,"instanceName":"6"}),makeQuery(id+"F2.opPattern","COPY",FACE,{"derivedFrom":subQ1,"instanceName":"7"}),makeQuery(id+"F2.opPattern","COPY",FACE,{"derivedFrom":subQ1,"instanceName":"8"}),makeQuery(id+"F2.opPattern","COPY",FACE,{"derivedFrom":subQ1,"instanceName":"9"}),makeQuery(id+"F2.opPattern","COPY",FACE,{"derivedFrom":subQ1,"instanceName":"10"}),makeQuery(id+"F2.opPattern","COPY",FACE,{"derivedFrom":subQ1,"instanceName":"11"}),makeQuery(id+"F2.opPattern","COPY",FACE,{"derivedFrom":subQ1,"instanceName":"12"}),makeQuery(id+"F2.opPattern","COPY",FACE,{"derivedFrom":subQ1,"instanceName":"13"}),makeQuery(id+"F2.opPattern","COPY",FACE,{"derivedFrom":subQ1,"instanceName":"14"}),makeQuery(id+"F2.opPattern","COPY",FACE,{"derivedFrom":subQ1,"instanceName":"15"}),makeQuery(id+"F2.opPattern","COPY",FACE,{"derivedFrom":subQ1,"instanceName":"16"}),makeQuery(id+"F2.opPattern","COPY",FACE,{"derivedFrom":subQ1,"instanceName":"17"}),makeQuery(id+"F2.opPattern","COPY",FACE,{"derivedFrom":subQ1,"instanceName":"18"}),makeQuery(id+"F2.opPattern","COPY",FACE,{"derivedFrom":subQ1,"instanceName":"19"}),makeQuery(id+"F2.opPattern","COPY",FACE,{"derivedFrom":subQ1,"instanceName":"20"}),makeQuery(id+"F2.opPattern","COPY",FACE,{"derivedFrom":subQ1,"instanceName":"21"}),makeQuery(id+"F2.opPattern","COPY",FACE,{"derivedFrom":subQ1,"instanceName":"22"}),makeQuery(id+"F2.opPattern","COPY",FACE,{"derivedFrom":subQ1,"instanceName":"23"})]})]});}
            var Q7;
            {var subQ0=sQuery(id+"F0.wireOp",EDGE,"E12");var subQ1=makeQuery(id+"F1.opExtrude","CAP_FACE",FACE,{"disambiguationData":[OSD([sQuery(id+"F0.wireOp",EDGE,"E2"),sQuery(id+"F0.wireOp",EDGE,"E11"),subQ0,sQuery(id+"F0.wireOp",EDGE,"E13.MirrorCS"),sQuery(id+"F0.wireOp",EDGE,"E14.MirrorCS"),sQuery(id+"F0.wireOp",EDGE,"E15"),sQuery(id+"F0.wireOp",EDGE,"E19")])],"isStart":false});Q7=makeQuery(id+"F3.opFillet","BLEND_EDGE",EDGE,{"blendedFrom":[makeQuery(id+"F2.opPattern","COPY",EDGE,{"derivedFrom":makeQuery(id+"F1.opExtrude","CAP_EDGE",EDGE,{"disambiguationData":[OSD([subQ0])],"isStart":false}),"instanceName":"2"}),makeQuery(id+"F2.boolean.opBoolean","MERGE",FACE,{"derivedFrom":[subQ1,makeQuery(id+"F2.opPattern","COPY",FACE,{"derivedFrom":subQ1,"instanceName":"1"}),makeQuery(id+"F2.opPattern","COPY",FACE,{"derivedFrom":subQ1,"instanceName":"2"}),makeQuery(id+"F2.opPattern","COPY",FACE,{"derivedFrom":subQ1,"instanceName":"3"}),makeQuery(id+"F2.opPattern","COPY",FACE,{"derivedFrom":subQ1,"instanceName":"4"}),makeQuery(id+"F2.opPattern","COPY",FACE,{"derivedFrom":subQ1,"instanceName":"5"}),makeQuery(id+"F2.opPattern","COPY",FACE,{"derivedFrom":subQ1,"instanceName":"6"}),makeQuery(id+"F2.opPattern","COPY",FACE,{"derivedFrom":subQ1,"instanceName":"7"}),makeQuery(id+"F2.opPattern","COPY",FACE,{"derivedFrom":subQ1,"instanceName":"8"}),makeQuery(id+"F2.opPattern","COPY",FACE,{"derivedFrom":subQ1,"instanceName":"9"}),makeQuery(id+"F2.opPattern","COPY",FACE,{"derivedFrom":subQ1,"instanceName":"10"}),makeQuery(id+"F2.opPattern","COPY",FACE,{"derivedFrom":subQ1,"instanceName":"11"}),makeQuery(id+"F2.opPattern","COPY",FACE,{"derivedFrom":subQ1,"instanceName":"12"}),makeQuery(id+"F2.opPattern","COPY",FACE,{"derivedFrom":subQ1,"instanceName":"13"}),makeQuery(id+"F2.opPattern","COPY",FACE,{"derivedFrom":subQ1,"instanceName":"14"}),makeQuery(id+"F2.opPattern","COPY",FACE,{"derivedFrom":subQ1,"instanceName":"15"}),makeQuery(id+"F2.opPattern","COPY",FACE,{"derivedFrom":subQ1,"instanceName":"16"}),makeQuery(id+"F2.opPattern","COPY",FACE,{"derivedFrom":subQ1,"instanceName":"17"}),makeQuery(id+"F2.opPattern","COPY",FACE,{"derivedFrom":subQ1,"instanceName":"18"}),makeQuery(id+"F2.opPattern","COPY",FACE,{"derivedFrom":subQ1,"instanceName":"19"}),makeQuery(id+"F2.opPattern","COPY",FACE,{"derivedFrom":subQ1,"instanceName":"20"}),makeQuery(id+"F2.opPattern","COPY",FACE,{"derivedFrom":subQ1,"instanceName":"21"}),makeQuery(id+"F2.opPattern","COPY",FACE,{"derivedFrom":subQ1,"instanceName":"22"}),makeQuery(id+"F2.opPattern","COPY",FACE,{"derivedFrom":subQ1,"instanceName":"23"})]})],"blendedInto":[makeQuery(id+"F2.boolean.opBoolean","MERGE",FACE,{"derivedFrom":[subQ1,makeQuery(id+"F2.opPattern","COPY",FACE,{"derivedFrom":subQ1,"instanceName":"1"}),makeQuery(id+"F2.opPattern","COPY",FACE,{"derivedFrom":subQ1,"instanceName":"2"}),makeQuery(id+"F2.opPattern","COPY",FACE,{"derivedFrom":subQ1,"instanceName":"3"}),makeQuery(id+"F2.opPattern","COPY",FACE,{"derivedFrom":subQ1,"instanceName":"4"}),makeQuery(id+"F2.opPattern","COPY",FACE,{"derivedFrom":subQ1,"instanceName":"5"}),makeQuery(id+"F2.opPattern","COPY",FACE,{"derivedFrom":subQ1,"instanceName":"6"}),makeQuery(id+"F2.opPattern","COPY",FACE,{"derivedFrom":subQ1,"instanceName":"7"}),makeQuery(id+"F2.opPattern","COPY",FACE,{"derivedFrom":subQ1,"instanceName":"8"}),makeQuery(id+"F2.opPattern","COPY",FACE,{"derivedFrom":subQ1,"instanceName":"9"}),makeQuery(id+"F2.opPattern","COPY",FACE,{"derivedFrom":subQ1,"instanceName":"10"}),makeQuery(id+"F2.opPattern","COPY",FACE,{"derivedFrom":subQ1,"instanceName":"11"}),makeQuery(id+"F2.opPattern","COPY",FACE,{"derivedFrom":subQ1,"instanceName":"12"}),makeQuery(id+"F2.opPattern","COPY",FACE,{"derivedFrom":subQ1,"instanceName":"13"}),makeQuery(id+"F2.opPattern","COPY",FACE,{"derivedFrom":subQ1,"instanceName":"14"}),makeQuery(id+"F2.opPattern","COPY",FACE,{"derivedFrom":subQ1,"instanceName":"15"}),makeQuery(id+"F2.opPattern","COPY",FACE,{"derivedFrom":subQ1,"instanceName":"16"}),makeQuery(id+"F2.opPattern","COPY",FACE,{"derivedFrom":subQ1,"instanceName":"17"}),makeQuery(id+"F2.opPattern","COPY",FACE,{"derivedFrom":subQ1,"instanceName":"18"}),makeQuery(id+"F2.opPattern","COPY",FACE,{"derivedFrom":subQ1,"instanceName":"19"}),makeQuery(id+"F2.opPattern","COPY",FACE,{"derivedFrom":subQ1,"instanceName":"20"}),makeQuery(id+"F2.opPattern","COPY",FACE,{"derivedFrom":subQ1,"instanceName":"21"}),makeQuery(id+"F2.opPattern","COPY",FACE,{"derivedFrom":subQ1,"instanceName":"22"}),makeQuery(id+"F2.opPattern","COPY",FACE,{"derivedFrom":subQ1,"instanceName":"23"})]})]});}
            var Q8;
            {var subQ0=sQuery(id+"F0.wireOp",EDGE,"E14.MirrorCS");var subQ1=makeQuery(id+"F1.opExtrude","CAP_FACE",FACE,{"disambiguationData":[OSD([sQuery(id+"F0.wireOp",EDGE,"E2"),sQuery(id+"F0.wireOp",EDGE,"E11"),sQuery(id+"F0.wireOp",EDGE,"E12"),sQuery(id+"F0.wireOp",EDGE,"E13.MirrorCS"),subQ0,sQuery(id+"F0.wireOp",EDGE,"E15"),sQuery(id+"F0.wireOp",EDGE,"E19")])],"isStart":false});Q8=makeQuery(id+"F3.opFillet","BLEND_EDGE",EDGE,{"blendedFrom":[makeQuery(id+"F2.opPattern","COPY",EDGE,{"derivedFrom":makeQuery(id+"F1.opExtrude","CAP_EDGE",EDGE,{"disambiguationData":[OSD([subQ0])],"isStart":false}),"instanceName":"3"}),makeQuery(id+"F2.boolean.opBoolean","MERGE",FACE,{"derivedFrom":[subQ1,makeQuery(id+"F2.opPattern","COPY",FACE,{"derivedFrom":subQ1,"instanceName":"1"}),makeQuery(id+"F2.opPattern","COPY",FACE,{"derivedFrom":subQ1,"instanceName":"2"}),makeQuery(id+"F2.opPattern","COPY",FACE,{"derivedFrom":subQ1,"instanceName":"3"}),makeQuery(id+"F2.opPattern","COPY",FACE,{"derivedFrom":subQ1,"instanceName":"4"}),makeQuery(id+"F2.opPattern","COPY",FACE,{"derivedFrom":subQ1,"instanceName":"5"}),makeQuery(id+"F2.opPattern","COPY",FACE,{"derivedFrom":subQ1,"instanceName":"6"}),makeQuery(id+"F2.opPattern","COPY",FACE,{"derivedFrom":subQ1,"instanceName":"7"}),makeQuery(id+"F2.opPattern","COPY",FACE,{"derivedFrom":subQ1,"instanceName":"8"}),makeQuery(id+"F2.opPattern","COPY",FACE,{"derivedFrom":subQ1,"instanceName":"9"}),makeQuery(id+"F2.opPattern","COPY",FACE,{"derivedFrom":subQ1,"instanceName":"10"}),makeQuery(id+"F2.opPattern","COPY",FACE,{"derivedFrom":subQ1,"instanceName":"11"}),makeQuery(id+"F2.opPattern","COPY",FACE,{"derivedFrom":subQ1,"instanceName":"12"}),makeQuery(id+"F2.opPattern","COPY",FACE,{"derivedFrom":subQ1,"instanceName":"13"}),makeQuery(id+"F2.opPattern","COPY",FACE,{"derivedFrom":subQ1,"instanceName":"14"}),makeQuery(id+"F2.opPattern","COPY",FACE,{"derivedFrom":subQ1,"instanceName":"15"}),makeQuery(id+"F2.opPattern","COPY",FACE,{"derivedFrom":subQ1,"instanceName":"16"}),makeQuery(id+"F2.opPattern","COPY",FACE,{"derivedFrom":subQ1,"instanceName":"17"}),makeQuery(id+"F2.opPattern","COPY",FACE,{"derivedFrom":subQ1,"instanceName":"18"}),makeQuery(id+"F2.opPattern","COPY",FACE,{"derivedFrom":subQ1,"instanceName":"19"}),makeQuery(id+"F2.opPattern","COPY",FACE,{"derivedFrom":subQ1,"instanceName":"20"}),makeQuery(id+"F2.opPattern","COPY",FACE,{"derivedFrom":subQ1,"instanceName":"21"}),makeQuery(id+"F2.opPattern","COPY",FACE,{"derivedFrom":subQ1,"instanceName":"22"}),makeQuery(id+"F2.opPattern","COPY",FACE,{"derivedFrom":subQ1,"instanceName":"23"})]})],"blendedInto":[makeQuery(id+"F2.boolean.opBoolean","MERGE",FACE,{"derivedFrom":[subQ1,makeQuery(id+"F2.opPattern","COPY",FACE,{"derivedFrom":subQ1,"instanceName":"1"}),makeQuery(id+"F2.opPattern","COPY",FACE,{"derivedFrom":subQ1,"instanceName":"2"}),makeQuery(id+"F2.opPattern","COPY",FACE,{"derivedFrom":subQ1,"instanceName":"3"}),makeQuery(id+"F2.opPattern","COPY",FACE,{"derivedFrom":subQ1,"instanceName":"4"}),makeQuery(id+"F2.opPattern","COPY",FACE,{"derivedFrom":subQ1,"instanceName":"5"}),makeQuery(id+"F2.opPattern","COPY",FACE,{"derivedFrom":subQ1,"instanceName":"6"}),makeQuery(id+"F2.opPattern","COPY",FACE,{"derivedFrom":subQ1,"instanceName":"7"}),makeQuery(id+"F2.opPattern","COPY",FACE,{"derivedFrom":subQ1,"instanceName":"8"}),makeQuery(id+"F2.opPattern","COPY",FACE,{"derivedFrom":subQ1,"instanceName":"9"}),makeQuery(id+"F2.opPattern","COPY",FACE,{"derivedFrom":subQ1,"instanceName":"10"}),makeQuery(id+"F2.opPattern","COPY",FACE,{"derivedFrom":subQ1,"instanceName":"11"}),makeQuery(id+"F2.opPattern","COPY",FACE,{"derivedFrom":subQ1,"instanceName":"12"}),makeQuery(id+"F2.opPattern","COPY",FACE,{"derivedFrom":subQ1,"instanceName":"13"}),makeQuery(id+"F2.opPattern","COPY",FACE,{"derivedFrom":subQ1,"instanceName":"14"}),makeQuery(id+"F2.opPattern","COPY",FACE,{"derivedFrom":subQ1,"instanceName":"15"}),makeQuery(id+"F2.opPattern","COPY",FACE,{"derivedFrom":subQ1,"instanceName":"16"}),makeQuery(id+"F2.opPattern","COPY",FACE,{"derivedFrom":subQ1,"instanceName":"17"}),makeQuery(id+"F2.opPattern","COPY",FACE,{"derivedFrom":subQ1,"instanceName":"18"}),makeQuery(id+"F2.opPattern","COPY",FACE,{"derivedFrom":subQ1,"instanceName":"19"}),makeQuery(id+"F2.opPattern","COPY",FACE,{"derivedFrom":subQ1,"instanceName":"20"}),makeQuery(id+"F2.opPattern","COPY",FACE,{"derivedFrom":subQ1,"instanceName":"21"}),makeQuery(id+"F2.opPattern","COPY",FACE,{"derivedFrom":subQ1,"instanceName":"22"}),makeQuery(id+"F2.opPattern","COPY",FACE,{"derivedFrom":subQ1,"instanceName":"23"})]})]});}
            var Q9;
            {var subQ0=sQuery(id+"F0.wireOp",EDGE,"E12");Q9=makeQuery(id+"F3.opFillet","BLEND_EDGE",EDGE,{"blendedFrom":[makeQuery(id+"F2.opPattern","COPY",EDGE,{"derivedFrom":makeQuery(id+"F1.opExtrude","CAP_EDGE",EDGE,{"disambiguationData":[OSD([subQ0])],"isStart":false}),"instanceName":"3"}),makeQuery(id+"F2.opPattern","COPY",FACE,{"derivedFrom":makeQuery(id+"F1.opExtrude","SWEPT_FACE",FACE,{"disambiguationData":[OSD([subQ0])]}),"instanceName":"3"})],"blendedInto":[makeQuery(id+"F2.opPattern","COPY",FACE,{"derivedFrom":makeQuery(id+"F1.opExtrude","SWEPT_FACE",FACE,{"disambiguationData":[OSD([subQ0])]}),"instanceName":"3"})]});}
            var Q10;
            {var subQ0=sQuery(id+"F0.wireOp",EDGE,"E14.MirrorCS");var subQ1=makeQuery(id+"F1.opExtrude","CAP_FACE",FACE,{"disambiguationData":[OSD([sQuery(id+"F0.wireOp",EDGE,"E2"),sQuery(id+"F0.wireOp",EDGE,"E11"),sQuery(id+"F0.wireOp",EDGE,"E12"),sQuery(id+"F0.wireOp",EDGE,"E13.MirrorCS"),subQ0,sQuery(id+"F0.wireOp",EDGE,"E15"),sQuery(id+"F0.wireOp",EDGE,"E19")])],"isStart":false});Q10=makeQuery(id+"F3.opFillet","BLEND_EDGE",EDGE,{"blendedFrom":[makeQuery(id+"F2.opPattern","COPY",EDGE,{"derivedFrom":makeQuery(id+"F1.opExtrude","CAP_EDGE",EDGE,{"disambiguationData":[OSD([subQ0])],"isStart":false}),"instanceName":"4"}),makeQuery(id+"F2.boolean.opBoolean","MERGE",FACE,{"derivedFrom":[subQ1,makeQuery(id+"F2.opPattern","COPY",FACE,{"derivedFrom":subQ1,"instanceName":"1"}),makeQuery(id+"F2.opPattern","COPY",FACE,{"derivedFrom":subQ1,"instanceName":"2"}),makeQuery(id+"F2.opPattern","COPY",FACE,{"derivedFrom":subQ1,"instanceName":"3"}),makeQuery(id+"F2.opPattern","COPY",FACE,{"derivedFrom":subQ1,"instanceName":"4"}),makeQuery(id+"F2.opPattern","COPY",FACE,{"derivedFrom":subQ1,"instanceName":"5"}),makeQuery(id+"F2.opPattern","COPY",FACE,{"derivedFrom":subQ1,"instanceName":"6"}),makeQuery(id+"F2.opPattern","COPY",FACE,{"derivedFrom":subQ1,"instanceName":"7"}),makeQuery(id+"F2.opPattern","COPY",FACE,{"derivedFrom":subQ1,"instanceName":"8"}),makeQuery(id+"F2.opPattern","COPY",FACE,{"derivedFrom":subQ1,"instanceName":"9"}),makeQuery(id+"F2.opPattern","COPY",FACE,{"derivedFrom":subQ1,"instanceName":"10"}),makeQuery(id+"F2.opPattern","COPY",FACE,{"derivedFrom":subQ1,"instanceName":"11"}),makeQuery(id+"F2.opPattern","COPY",FACE,{"derivedFrom":subQ1,"instanceName":"12"}),makeQuery(id+"F2.opPattern","COPY",FACE,{"derivedFrom":subQ1,"instanceName":"13"}),makeQuery(id+"F2.opPattern","COPY",FACE,{"derivedFrom":subQ1,"instanceName":"14"}),makeQuery(id+"F2.opPattern","COPY",FACE,{"derivedFrom":subQ1,"instanceName":"15"}),makeQuery(id+"F2.opPattern","COPY",FACE,{"derivedFrom":subQ1,"instanceName":"16"}),makeQuery(id+"F2.opPattern","COPY",FACE,{"derivedFrom":subQ1,"instanceName":"17"}),makeQuery(id+"F2.opPattern","COPY",FACE,{"derivedFrom":subQ1,"instanceName":"18"}),makeQuery(id+"F2.opPattern","COPY",FACE,{"derivedFrom":subQ1,"instanceName":"19"}),makeQuery(id+"F2.opPattern","COPY",FACE,{"derivedFrom":subQ1,"instanceName":"20"}),makeQuery(id+"F2.opPattern","COPY",FACE,{"derivedFrom":subQ1,"instanceName":"21"}),makeQuery(id+"F2.opPattern","COPY",FACE,{"derivedFrom":subQ1,"instanceName":"22"}),makeQuery(id+"F2.opPattern","COPY",FACE,{"derivedFrom":subQ1,"instanceName":"23"})]})],"blendedInto":[makeQuery(id+"F2.boolean.opBoolean","MERGE",FACE,{"derivedFrom":[subQ1,makeQuery(id+"F2.opPattern","COPY",FACE,{"derivedFrom":subQ1,"instanceName":"1"}),makeQuery(id+"F2.opPattern","COPY",FACE,{"derivedFrom":subQ1,"instanceName":"2"}),makeQuery(id+"F2.opPattern","COPY",FACE,{"derivedFrom":subQ1,"instanceName":"3"}),makeQuery(id+"F2.opPattern","COPY",FACE,{"derivedFrom":subQ1,"instanceName":"4"}),makeQuery(id+"F2.opPattern","COPY",FACE,{"derivedFrom":subQ1,"instanceName":"5"}),makeQuery(id+"F2.opPattern","COPY",FACE,{"derivedFrom":subQ1,"instanceName":"6"}),makeQuery(id+"F2.opPattern","COPY",FACE,{"derivedFrom":subQ1,"instanceName":"7"}),makeQuery(id+"F2.opPattern","COPY",FACE,{"derivedFrom":subQ1,"instanceName":"8"}),makeQuery(id+"F2.opPattern","COPY",FACE,{"derivedFrom":subQ1,"instanceName":"9"}),makeQuery(id+"F2.opPattern","COPY",FACE,{"derivedFrom":subQ1,"instanceName":"10"}),makeQuery(id+"F2.opPattern","COPY",FACE,{"derivedFrom":subQ1,"instanceName":"11"}),makeQuery(id+"F2.opPattern","COPY",FACE,{"derivedFrom":subQ1,"instanceName":"12"}),makeQuery(id+"F2.opPattern","COPY",FACE,{"derivedFrom":subQ1,"instanceName":"13"}),makeQuery(id+"F2.opPattern","COPY",FACE,{"derivedFrom":subQ1,"instanceName":"14"}),makeQuery(id+"F2.opPattern","COPY",FACE,{"derivedFrom":subQ1,"instanceName":"15"}),makeQuery(id+"F2.opPattern","COPY",FACE,{"derivedFrom":subQ1,"instanceName":"16"}),makeQuery(id+"F2.opPattern","COPY",FACE,{"derivedFrom":subQ1,"instanceName":"17"}),makeQuery(id+"F2.opPattern","COPY",FACE,{"derivedFrom":subQ1,"instanceName":"18"}),makeQuery(id+"F2.opPattern","COPY",FACE,{"derivedFrom":subQ1,"instanceName":"19"}),makeQuery(id+"F2.opPattern","COPY",FACE,{"derivedFrom":subQ1,"instanceName":"20"}),makeQuery(id+"F2.opPattern","COPY",FACE,{"derivedFrom":subQ1,"instanceName":"21"}),makeQuery(id+"F2.opPattern","COPY",FACE,{"derivedFrom":subQ1,"instanceName":"22"}),makeQuery(id+"F2.opPattern","COPY",FACE,{"derivedFrom":subQ1,"instanceName":"23"})]})]});}
            var Q11;
            {var subQ0=sQuery(id+"F0.wireOp",EDGE,"E12");var subQ1=makeQuery(id+"F1.opExtrude","CAP_FACE",FACE,{"disambiguationData":[OSD([sQuery(id+"F0.wireOp",EDGE,"E2"),sQuery(id+"F0.wireOp",EDGE,"E11"),subQ0,sQuery(id+"F0.wireOp",EDGE,"E13.MirrorCS"),sQuery(id+"F0.wireOp",EDGE,"E14.MirrorCS"),sQuery(id+"F0.wireOp",EDGE,"E15"),sQuery(id+"F0.wireOp",EDGE,"E19")])],"isStart":false});Q11=makeQuery(id+"F3.opFillet","BLEND_EDGE",EDGE,{"blendedFrom":[makeQuery(id+"F2.opPattern","COPY",EDGE,{"derivedFrom":makeQuery(id+"F1.opExtrude","CAP_EDGE",EDGE,{"disambiguationData":[OSD([subQ0])],"isStart":false}),"instanceName":"4"}),makeQuery(id+"F2.boolean.opBoolean","MERGE",FACE,{"derivedFrom":[subQ1,makeQuery(id+"F2.opPattern","COPY",FACE,{"derivedFrom":subQ1,"instanceName":"1"}),makeQuery(id+"F2.opPattern","COPY",FACE,{"derivedFrom":subQ1,"instanceName":"2"}),makeQuery(id+"F2.opPattern","COPY",FACE,{"derivedFrom":subQ1,"instanceName":"3"}),makeQuery(id+"F2.opPattern","COPY",FACE,{"derivedFrom":subQ1,"instanceName":"4"}),makeQuery(id+"F2.opPattern","COPY",FACE,{"derivedFrom":subQ1,"instanceName":"5"}),makeQuery(id+"F2.opPattern","COPY",FACE,{"derivedFrom":subQ1,"instanceName":"6"}),makeQuery(id+"F2.opPattern","COPY",FACE,{"derivedFrom":subQ1,"instanceName":"7"}),makeQuery(id+"F2.opPattern","COPY",FACE,{"derivedFrom":subQ1,"instanceName":"8"}),makeQuery(id+"F2.opPattern","COPY",FACE,{"derivedFrom":subQ1,"instanceName":"9"}),makeQuery(id+"F2.opPattern","COPY",FACE,{"derivedFrom":subQ1,"instanceName":"10"}),makeQuery(id+"F2.opPattern","COPY",FACE,{"derivedFrom":subQ1,"instanceName":"11"}),makeQuery(id+"F2.opPattern","COPY",FACE,{"derivedFrom":subQ1,"instanceName":"12"}),makeQuery(id+"F2.opPattern","COPY",FACE,{"derivedFrom":subQ1,"instanceName":"13"}),makeQuery(id+"F2.opPattern","COPY",FACE,{"derivedFrom":subQ1,"instanceName":"14"}),makeQuery(id+"F2.opPattern","COPY",FACE,{"derivedFrom":subQ1,"instanceName":"15"}),makeQuery(id+"F2.opPattern","COPY",FACE,{"derivedFrom":subQ1,"instanceName":"16"}),makeQuery(id+"F2.opPattern","COPY",FACE,{"derivedFrom":subQ1,"instanceName":"17"}),makeQuery(id+"F2.opPattern","COPY",FACE,{"derivedFrom":subQ1,"instanceName":"18"}),makeQuery(id+"F2.opPattern","COPY",FACE,{"derivedFrom":subQ1,"instanceName":"19"}),makeQuery(id+"F2.opPattern","COPY",FACE,{"derivedFrom":subQ1,"instanceName":"20"}),makeQuery(id+"F2.opPattern","COPY",FACE,{"derivedFrom":subQ1,"instanceName":"21"}),makeQuery(id+"F2.opPattern","COPY",FACE,{"derivedFrom":subQ1,"instanceName":"22"}),makeQuery(id+"F2.opPattern","COPY",FACE,{"derivedFrom":subQ1,"instanceName":"23"})]})],"blendedInto":[makeQuery(id+"F2.boolean.opBoolean","MERGE",FACE,{"derivedFrom":[subQ1,makeQuery(id+"F2.opPattern","COPY",FACE,{"derivedFrom":subQ1,"instanceName":"1"}),makeQuery(id+"F2.opPattern","COPY",FACE,{"derivedFrom":subQ1,"instanceName":"2"}),makeQuery(id+"F2.opPattern","COPY",FACE,{"derivedFrom":subQ1,"instanceName":"3"}),makeQuery(id+"F2.opPattern","COPY",FACE,{"derivedFrom":subQ1,"instanceName":"4"}),makeQuery(id+"F2.opPattern","COPY",FACE,{"derivedFrom":subQ1,"instanceName":"5"}),makeQuery(id+"F2.opPattern","COPY",FACE,{"derivedFrom":subQ1,"instanceName":"6"}),makeQuery(id+"F2.opPattern","COPY",FACE,{"derivedFrom":subQ1,"instanceName":"7"}),makeQuery(id+"F2.opPattern","COPY",FACE,{"derivedFrom":subQ1,"instanceName":"8"}),makeQuery(id+"F2.opPattern","COPY",FACE,{"derivedFrom":subQ1,"instanceName":"9"}),makeQuery(id+"F2.opPattern","COPY",FACE,{"derivedFrom":subQ1,"instanceName":"10"}),makeQuery(id+"F2.opPattern","COPY",FACE,{"derivedFrom":subQ1,"instanceName":"11"}),makeQuery(id+"F2.opPattern","COPY",FACE,{"derivedFrom":subQ1,"instanceName":"12"}),makeQuery(id+"F2.opPattern","COPY",FACE,{"derivedFrom":subQ1,"instanceName":"13"}),makeQuery(id+"F2.opPattern","COPY",FACE,{"derivedFrom":subQ1,"instanceName":"14"}),makeQuery(id+"F2.opPattern","COPY",FACE,{"derivedFrom":subQ1,"instanceName":"15"}),makeQuery(id+"F2.opPattern","COPY",FACE,{"derivedFrom":subQ1,"instanceName":"16"}),makeQuery(id+"F2.opPattern","COPY",FACE,{"derivedFrom":subQ1,"instanceName":"17"}),makeQuery(id+"F2.opPattern","COPY",FACE,{"derivedFrom":subQ1,"instanceName":"18"}),makeQuery(id+"F2.opPattern","COPY",FACE,{"derivedFrom":subQ1,"instanceName":"19"}),makeQuery(id+"F2.opPattern","COPY",FACE,{"derivedFrom":subQ1,"instanceName":"20"}),makeQuery(id+"F2.opPattern","COPY",FACE,{"derivedFrom":subQ1,"instanceName":"21"}),makeQuery(id+"F2.opPattern","COPY",FACE,{"derivedFrom":subQ1,"instanceName":"22"}),makeQuery(id+"F2.opPattern","COPY",FACE,{"derivedFrom":subQ1,"instanceName":"23"})]})]});}
            var Q12;
            {var subQ0=sQuery(id+"F0.wireOp",EDGE,"E12");Q12=makeQuery(id+"F3.opFillet","BLEND_EDGE",EDGE,{"blendedFrom":[makeQuery(id+"F2.opPattern","COPY",EDGE,{"derivedFrom":makeQuery(id+"F1.opExtrude","CAP_EDGE",EDGE,{"disambiguationData":[OSD([subQ0])],"isStart":false}),"instanceName":"5"}),makeQuery(id+"F2.opPattern","COPY",FACE,{"derivedFrom":makeQuery(id+"F1.opExtrude","SWEPT_FACE",FACE,{"disambiguationData":[OSD([subQ0])]}),"instanceName":"5"})],"blendedInto":[makeQuery(id+"F2.opPattern","COPY",FACE,{"derivedFrom":makeQuery(id+"F1.opExtrude","SWEPT_FACE",FACE,{"disambiguationData":[OSD([subQ0])]}),"instanceName":"5"})]});}
            var Q13;
            {var subQ0=sQuery(id+"F0.wireOp",EDGE,"E14.MirrorCS");var subQ1=makeQuery(id+"F1.opExtrude","CAP_FACE",FACE,{"disambiguationData":[OSD([sQuery(id+"F0.wireOp",EDGE,"E2"),sQuery(id+"F0.wireOp",EDGE,"E11"),sQuery(id+"F0.wireOp",EDGE,"E12"),sQuery(id+"F0.wireOp",EDGE,"E13.MirrorCS"),subQ0,sQuery(id+"F0.wireOp",EDGE,"E15"),sQuery(id+"F0.wireOp",EDGE,"E19")])],"isStart":false});Q13=makeQuery(id+"F3.opFillet","BLEND_EDGE",EDGE,{"blendedFrom":[makeQuery(id+"F2.opPattern","COPY",EDGE,{"derivedFrom":makeQuery(id+"F1.opExtrude","CAP_EDGE",EDGE,{"disambiguationData":[OSD([subQ0])],"isStart":false}),"instanceName":"5"}),makeQuery(id+"F2.boolean.opBoolean","MERGE",FACE,{"derivedFrom":[subQ1,makeQuery(id+"F2.opPattern","COPY",FACE,{"derivedFrom":subQ1,"instanceName":"1"}),makeQuery(id+"F2.opPattern","COPY",FACE,{"derivedFrom":subQ1,"instanceName":"2"}),makeQuery(id+"F2.opPattern","COPY",FACE,{"derivedFrom":subQ1,"instanceName":"3"}),makeQuery(id+"F2.opPattern","COPY",FACE,{"derivedFrom":subQ1,"instanceName":"4"}),makeQuery(id+"F2.opPattern","COPY",FACE,{"derivedFrom":subQ1,"instanceName":"5"}),makeQuery(id+"F2.opPattern","COPY",FACE,{"derivedFrom":subQ1,"instanceName":"6"}),makeQuery(id+"F2.opPattern","COPY",FACE,{"derivedFrom":subQ1,"instanceName":"7"}),makeQuery(id+"F2.opPattern","COPY",FACE,{"derivedFrom":subQ1,"instanceName":"8"}),makeQuery(id+"F2.opPattern","COPY",FACE,{"derivedFrom":subQ1,"instanceName":"9"}),makeQuery(id+"F2.opPattern","COPY",FACE,{"derivedFrom":subQ1,"instanceName":"10"}),makeQuery(id+"F2.opPattern","COPY",FACE,{"derivedFrom":subQ1,"instanceName":"11"}),makeQuery(id+"F2.opPattern","COPY",FACE,{"derivedFrom":subQ1,"instanceName":"12"}),makeQuery(id+"F2.opPattern","COPY",FACE,{"derivedFrom":subQ1,"instanceName":"13"}),makeQuery(id+"F2.opPattern","COPY",FACE,{"derivedFrom":subQ1,"instanceName":"14"}),makeQuery(id+"F2.opPattern","COPY",FACE,{"derivedFrom":subQ1,"instanceName":"15"}),makeQuery(id+"F2.opPattern","COPY",FACE,{"derivedFrom":subQ1,"instanceName":"16"}),makeQuery(id+"F2.opPattern","COPY",FACE,{"derivedFrom":subQ1,"instanceName":"17"}),makeQuery(id+"F2.opPattern","COPY",FACE,{"derivedFrom":subQ1,"instanceName":"18"}),makeQuery(id+"F2.opPattern","COPY",FACE,{"derivedFrom":subQ1,"instanceName":"19"}),makeQuery(id+"F2.opPattern","COPY",FACE,{"derivedFrom":subQ1,"instanceName":"20"}),makeQuery(id+"F2.opPattern","COPY",FACE,{"derivedFrom":subQ1,"instanceName":"21"}),makeQuery(id+"F2.opPattern","COPY",FACE,{"derivedFrom":subQ1,"instanceName":"22"}),makeQuery(id+"F2.opPattern","COPY",FACE,{"derivedFrom":subQ1,"instanceName":"23"})]})],"blendedInto":[makeQuery(id+"F2.boolean.opBoolean","MERGE",FACE,{"derivedFrom":[subQ1,makeQuery(id+"F2.opPattern","COPY",FACE,{"derivedFrom":subQ1,"instanceName":"1"}),makeQuery(id+"F2.opPattern","COPY",FACE,{"derivedFrom":subQ1,"instanceName":"2"}),makeQuery(id+"F2.opPattern","COPY",FACE,{"derivedFrom":subQ1,"instanceName":"3"}),makeQuery(id+"F2.opPattern","COPY",FACE,{"derivedFrom":subQ1,"instanceName":"4"}),makeQuery(id+"F2.opPattern","COPY",FACE,{"derivedFrom":subQ1,"instanceName":"5"}),makeQuery(id+"F2.opPattern","COPY",FACE,{"derivedFrom":subQ1,"instanceName":"6"}),makeQuery(id+"F2.opPattern","COPY",FACE,{"derivedFrom":subQ1,"instanceName":"7"}),makeQuery(id+"F2.opPattern","COPY",FACE,{"derivedFrom":subQ1,"instanceName":"8"}),makeQuery(id+"F2.opPattern","COPY",FACE,{"derivedFrom":subQ1,"instanceName":"9"}),makeQuery(id+"F2.opPattern","COPY",FACE,{"derivedFrom":subQ1,"instanceName":"10"}),makeQuery(id+"F2.opPattern","COPY",FACE,{"derivedFrom":subQ1,"instanceName":"11"}),makeQuery(id+"F2.opPattern","COPY",FACE,{"derivedFrom":subQ1,"instanceName":"12"}),makeQuery(id+"F2.opPattern","COPY",FACE,{"derivedFrom":subQ1,"instanceName":"13"}),makeQuery(id+"F2.opPattern","COPY",FACE,{"derivedFrom":subQ1,"instanceName":"14"}),makeQuery(id+"F2.opPattern","COPY",FACE,{"derivedFrom":subQ1,"instanceName":"15"}),makeQuery(id+"F2.opPattern","COPY",FACE,{"derivedFrom":subQ1,"instanceName":"16"}),makeQuery(id+"F2.opPattern","COPY",FACE,{"derivedFrom":subQ1,"instanceName":"17"}),makeQuery(id+"F2.opPattern","COPY",FACE,{"derivedFrom":subQ1,"instanceName":"18"}),makeQuery(id+"F2.opPattern","COPY",FACE,{"derivedFrom":subQ1,"instanceName":"19"}),makeQuery(id+"F2.opPattern","COPY",FACE,{"derivedFrom":subQ1,"instanceName":"20"}),makeQuery(id+"F2.opPattern","COPY",FACE,{"derivedFrom":subQ1,"instanceName":"21"}),makeQuery(id+"F2.opPattern","COPY",FACE,{"derivedFrom":subQ1,"instanceName":"22"}),makeQuery(id+"F2.opPattern","COPY",FACE,{"derivedFrom":subQ1,"instanceName":"23"})]})]});}
            var Q14;
            {var subQ0=sQuery(id+"F0.wireOp",EDGE,"E12");var subQ1=makeQuery(id+"F1.opExtrude","CAP_FACE",FACE,{"disambiguationData":[OSD([sQuery(id+"F0.wireOp",EDGE,"E2"),sQuery(id+"F0.wireOp",EDGE,"E11"),subQ0,sQuery(id+"F0.wireOp",EDGE,"E13.MirrorCS"),sQuery(id+"F0.wireOp",EDGE,"E14.MirrorCS"),sQuery(id+"F0.wireOp",EDGE,"E15"),sQuery(id+"F0.wireOp",EDGE,"E19")])],"isStart":false});Q14=makeQuery(id+"F3.opFillet","BLEND_EDGE",EDGE,{"blendedFrom":[makeQuery(id+"F2.opPattern","COPY",EDGE,{"derivedFrom":makeQuery(id+"F1.opExtrude","CAP_EDGE",EDGE,{"disambiguationData":[OSD([subQ0])],"isStart":false}),"instanceName":"6"}),makeQuery(id+"F2.boolean.opBoolean","MERGE",FACE,{"derivedFrom":[subQ1,makeQuery(id+"F2.opPattern","COPY",FACE,{"derivedFrom":subQ1,"instanceName":"1"}),makeQuery(id+"F2.opPattern","COPY",FACE,{"derivedFrom":subQ1,"instanceName":"2"}),makeQuery(id+"F2.opPattern","COPY",FACE,{"derivedFrom":subQ1,"instanceName":"3"}),makeQuery(id+"F2.opPattern","COPY",FACE,{"derivedFrom":subQ1,"instanceName":"4"}),makeQuery(id+"F2.opPattern","COPY",FACE,{"derivedFrom":subQ1,"instanceName":"5"}),makeQuery(id+"F2.opPattern","COPY",FACE,{"derivedFrom":subQ1,"instanceName":"6"}),makeQuery(id+"F2.opPattern","COPY",FACE,{"derivedFrom":subQ1,"instanceName":"7"}),makeQuery(id+"F2.opPattern","COPY",FACE,{"derivedFrom":subQ1,"instanceName":"8"}),makeQuery(id+"F2.opPattern","COPY",FACE,{"derivedFrom":subQ1,"instanceName":"9"}),makeQuery(id+"F2.opPattern","COPY",FACE,{"derivedFrom":subQ1,"instanceName":"10"}),makeQuery(id+"F2.opPattern","COPY",FACE,{"derivedFrom":subQ1,"instanceName":"11"}),makeQuery(id+"F2.opPattern","COPY",FACE,{"derivedFrom":subQ1,"instanceName":"12"}),makeQuery(id+"F2.opPattern","COPY",FACE,{"derivedFrom":subQ1,"instanceName":"13"}),makeQuery(id+"F2.opPattern","COPY",FACE,{"derivedFrom":subQ1,"instanceName":"14"}),makeQuery(id+"F2.opPattern","COPY",FACE,{"derivedFrom":subQ1,"instanceName":"15"}),makeQuery(id+"F2.opPattern","COPY",FACE,{"derivedFrom":subQ1,"instanceName":"16"}),makeQuery(id+"F2.opPattern","COPY",FACE,{"derivedFrom":subQ1,"instanceName":"17"}),makeQuery(id+"F2.opPattern","COPY",FACE,{"derivedFrom":subQ1,"instanceName":"18"}),makeQuery(id+"F2.opPattern","COPY",FACE,{"derivedFrom":subQ1,"instanceName":"19"}),makeQuery(id+"F2.opPattern","COPY",FACE,{"derivedFrom":subQ1,"instanceName":"20"}),makeQuery(id+"F2.opPattern","COPY",FACE,{"derivedFrom":subQ1,"instanceName":"21"}),makeQuery(id+"F2.opPattern","COPY",FACE,{"derivedFrom":subQ1,"instanceName":"22"}),makeQuery(id+"F2.opPattern","COPY",FACE,{"derivedFrom":subQ1,"instanceName":"23"})]})],"blendedInto":[makeQuery(id+"F2.boolean.opBoolean","MERGE",FACE,{"derivedFrom":[subQ1,makeQuery(id+"F2.opPattern","COPY",FACE,{"derivedFrom":subQ1,"instanceName":"1"}),makeQuery(id+"F2.opPattern","COPY",FACE,{"derivedFrom":subQ1,"instanceName":"2"}),makeQuery(id+"F2.opPattern","COPY",FACE,{"derivedFrom":subQ1,"instanceName":"3"}),makeQuery(id+"F2.opPattern","COPY",FACE,{"derivedFrom":subQ1,"instanceName":"4"}),makeQuery(id+"F2.opPattern","COPY",FACE,{"derivedFrom":subQ1,"instanceName":"5"}),makeQuery(id+"F2.opPattern","COPY",FACE,{"derivedFrom":subQ1,"instanceName":"6"}),makeQuery(id+"F2.opPattern","COPY",FACE,{"derivedFrom":subQ1,"instanceName":"7"}),makeQuery(id+"F2.opPattern","COPY",FACE,{"derivedFrom":subQ1,"instanceName":"8"}),makeQuery(id+"F2.opPattern","COPY",FACE,{"derivedFrom":subQ1,"instanceName":"9"}),makeQuery(id+"F2.opPattern","COPY",FACE,{"derivedFrom":subQ1,"instanceName":"10"}),makeQuery(id+"F2.opPattern","COPY",FACE,{"derivedFrom":subQ1,"instanceName":"11"}),makeQuery(id+"F2.opPattern","COPY",FACE,{"derivedFrom":subQ1,"instanceName":"12"}),makeQuery(id+"F2.opPattern","COPY",FACE,{"derivedFrom":subQ1,"instanceName":"13"}),makeQuery(id+"F2.opPattern","COPY",FACE,{"derivedFrom":subQ1,"instanceName":"14"}),makeQuery(id+"F2.opPattern","COPY",FACE,{"derivedFrom":subQ1,"instanceName":"15"}),makeQuery(id+"F2.opPattern","COPY",FACE,{"derivedFrom":subQ1,"instanceName":"16"}),makeQuery(id+"F2.opPattern","COPY",FACE,{"derivedFrom":subQ1,"instanceName":"17"}),makeQuery(id+"F2.opPattern","COPY",FACE,{"derivedFrom":subQ1,"instanceName":"18"}),makeQuery(id+"F2.opPattern","COPY",FACE,{"derivedFrom":subQ1,"instanceName":"19"}),makeQuery(id+"F2.opPattern","COPY",FACE,{"derivedFrom":subQ1,"instanceName":"20"}),makeQuery(id+"F2.opPattern","COPY",FACE,{"derivedFrom":subQ1,"instanceName":"21"}),makeQuery(id+"F2.opPattern","COPY",FACE,{"derivedFrom":subQ1,"instanceName":"22"}),makeQuery(id+"F2.opPattern","COPY",FACE,{"derivedFrom":subQ1,"instanceName":"23"})]})]});}
            var Q15;
            {var subQ0=sQuery(id+"F0.wireOp",EDGE,"E14.MirrorCS");var subQ1=makeQuery(id+"F1.opExtrude","CAP_FACE",FACE,{"disambiguationData":[OSD([sQuery(id+"F0.wireOp",EDGE,"E2"),sQuery(id+"F0.wireOp",EDGE,"E11"),sQuery(id+"F0.wireOp",EDGE,"E12"),sQuery(id+"F0.wireOp",EDGE,"E13.MirrorCS"),subQ0,sQuery(id+"F0.wireOp",EDGE,"E15"),sQuery(id+"F0.wireOp",EDGE,"E19")])],"isStart":false});Q15=makeQuery(id+"F3.opFillet","BLEND_EDGE",EDGE,{"blendedFrom":[makeQuery(id+"F2.opPattern","COPY",EDGE,{"derivedFrom":makeQuery(id+"F1.opExtrude","CAP_EDGE",EDGE,{"disambiguationData":[OSD([subQ0])],"isStart":false}),"instanceName":"6"}),makeQuery(id+"F2.boolean.opBoolean","MERGE",FACE,{"derivedFrom":[subQ1,makeQuery(id+"F2.opPattern","COPY",FACE,{"derivedFrom":subQ1,"instanceName":"1"}),makeQuery(id+"F2.opPattern","COPY",FACE,{"derivedFrom":subQ1,"instanceName":"2"}),makeQuery(id+"F2.opPattern","COPY",FACE,{"derivedFrom":subQ1,"instanceName":"3"}),makeQuery(id+"F2.opPattern","COPY",FACE,{"derivedFrom":subQ1,"instanceName":"4"}),makeQuery(id+"F2.opPattern","COPY",FACE,{"derivedFrom":subQ1,"instanceName":"5"}),makeQuery(id+"F2.opPattern","COPY",FACE,{"derivedFrom":subQ1,"instanceName":"6"}),makeQuery(id+"F2.opPattern","COPY",FACE,{"derivedFrom":subQ1,"instanceName":"7"}),makeQuery(id+"F2.opPattern","COPY",FACE,{"derivedFrom":subQ1,"instanceName":"8"}),makeQuery(id+"F2.opPattern","COPY",FACE,{"derivedFrom":subQ1,"instanceName":"9"}),makeQuery(id+"F2.opPattern","COPY",FACE,{"derivedFrom":subQ1,"instanceName":"10"}),makeQuery(id+"F2.opPattern","COPY",FACE,{"derivedFrom":subQ1,"instanceName":"11"}),makeQuery(id+"F2.opPattern","COPY",FACE,{"derivedFrom":subQ1,"instanceName":"12"}),makeQuery(id+"F2.opPattern","COPY",FACE,{"derivedFrom":subQ1,"instanceName":"13"}),makeQuery(id+"F2.opPattern","COPY",FACE,{"derivedFrom":subQ1,"instanceName":"14"}),makeQuery(id+"F2.opPattern","COPY",FACE,{"derivedFrom":subQ1,"instanceName":"15"}),makeQuery(id+"F2.opPattern","COPY",FACE,{"derivedFrom":subQ1,"instanceName":"16"}),makeQuery(id+"F2.opPattern","COPY",FACE,{"derivedFrom":subQ1,"instanceName":"17"}),makeQuery(id+"F2.opPattern","COPY",FACE,{"derivedFrom":subQ1,"instanceName":"18"}),makeQuery(id+"F2.opPattern","COPY",FACE,{"derivedFrom":subQ1,"instanceName":"19"}),makeQuery(id+"F2.opPattern","COPY",FACE,{"derivedFrom":subQ1,"instanceName":"20"}),makeQuery(id+"F2.opPattern","COPY",FACE,{"derivedFrom":subQ1,"instanceName":"21"}),makeQuery(id+"F2.opPattern","COPY",FACE,{"derivedFrom":subQ1,"instanceName":"22"}),makeQuery(id+"F2.opPattern","COPY",FACE,{"derivedFrom":subQ1,"instanceName":"23"})]})],"blendedInto":[makeQuery(id+"F2.boolean.opBoolean","MERGE",FACE,{"derivedFrom":[subQ1,makeQuery(id+"F2.opPattern","COPY",FACE,{"derivedFrom":subQ1,"instanceName":"1"}),makeQuery(id+"F2.opPattern","COPY",FACE,{"derivedFrom":subQ1,"instanceName":"2"}),makeQuery(id+"F2.opPattern","COPY",FACE,{"derivedFrom":subQ1,"instanceName":"3"}),makeQuery(id+"F2.opPattern","COPY",FACE,{"derivedFrom":subQ1,"instanceName":"4"}),makeQuery(id+"F2.opPattern","COPY",FACE,{"derivedFrom":subQ1,"instanceName":"5"}),makeQuery(id+"F2.opPattern","COPY",FACE,{"derivedFrom":subQ1,"instanceName":"6"}),makeQuery(id+"F2.opPattern","COPY",FACE,{"derivedFrom":subQ1,"instanceName":"7"}),makeQuery(id+"F2.opPattern","COPY",FACE,{"derivedFrom":subQ1,"instanceName":"8"}),makeQuery(id+"F2.opPattern","COPY",FACE,{"derivedFrom":subQ1,"instanceName":"9"}),makeQuery(id+"F2.opPattern","COPY",FACE,{"derivedFrom":subQ1,"instanceName":"10"}),makeQuery(id+"F2.opPattern","COPY",FACE,{"derivedFrom":subQ1,"instanceName":"11"}),makeQuery(id+"F2.opPattern","COPY",FACE,{"derivedFrom":subQ1,"instanceName":"12"}),makeQuery(id+"F2.opPattern","COPY",FACE,{"derivedFrom":subQ1,"instanceName":"13"}),makeQuery(id+"F2.opPattern","COPY",FACE,{"derivedFrom":subQ1,"instanceName":"14"}),makeQuery(id+"F2.opPattern","COPY",FACE,{"derivedFrom":subQ1,"instanceName":"15"}),makeQuery(id+"F2.opPattern","COPY",FACE,{"derivedFrom":subQ1,"instanceName":"16"}),makeQuery(id+"F2.opPattern","COPY",FACE,{"derivedFrom":subQ1,"instanceName":"17"}),makeQuery(id+"F2.opPattern","COPY",FACE,{"derivedFrom":subQ1,"instanceName":"18"}),makeQuery(id+"F2.opPattern","COPY",FACE,{"derivedFrom":subQ1,"instanceName":"19"}),makeQuery(id+"F2.opPattern","COPY",FACE,{"derivedFrom":subQ1,"instanceName":"20"}),makeQuery(id+"F2.opPattern","COPY",FACE,{"derivedFrom":subQ1,"instanceName":"21"}),makeQuery(id+"F2.opPattern","COPY",FACE,{"derivedFrom":subQ1,"instanceName":"22"}),makeQuery(id+"F2.opPattern","COPY",FACE,{"derivedFrom":subQ1,"instanceName":"23"})]})]});}
            var Q16;
            {var subQ0=sQuery(id+"F0.wireOp",EDGE,"E14.MirrorCS");var subQ1=makeQuery(id+"F1.opExtrude","CAP_FACE",FACE,{"disambiguationData":[OSD([sQuery(id+"F0.wireOp",EDGE,"E2"),sQuery(id+"F0.wireOp",EDGE,"E11"),sQuery(id+"F0.wireOp",EDGE,"E12"),sQuery(id+"F0.wireOp",EDGE,"E13.MirrorCS"),subQ0,sQuery(id+"F0.wireOp",EDGE,"E15"),sQuery(id+"F0.wireOp",EDGE,"E19")])],"isStart":false});Q16=makeQuery(id+"F3.opFillet","BLEND_EDGE",EDGE,{"blendedFrom":[makeQuery(id+"F2.opPattern","COPY",EDGE,{"derivedFrom":makeQuery(id+"F1.opExtrude","CAP_EDGE",EDGE,{"disambiguationData":[OSD([subQ0])],"isStart":false}),"instanceName":"7"}),makeQuery(id+"F2.boolean.opBoolean","MERGE",FACE,{"derivedFrom":[subQ1,makeQuery(id+"F2.opPattern","COPY",FACE,{"derivedFrom":subQ1,"instanceName":"1"}),makeQuery(id+"F2.opPattern","COPY",FACE,{"derivedFrom":subQ1,"instanceName":"2"}),makeQuery(id+"F2.opPattern","COPY",FACE,{"derivedFrom":subQ1,"instanceName":"3"}),makeQuery(id+"F2.opPattern","COPY",FACE,{"derivedFrom":subQ1,"instanceName":"4"}),makeQuery(id+"F2.opPattern","COPY",FACE,{"derivedFrom":subQ1,"instanceName":"5"}),makeQuery(id+"F2.opPattern","COPY",FACE,{"derivedFrom":subQ1,"instanceName":"6"}),makeQuery(id+"F2.opPattern","COPY",FACE,{"derivedFrom":subQ1,"instanceName":"7"}),makeQuery(id+"F2.opPattern","COPY",FACE,{"derivedFrom":subQ1,"instanceName":"8"}),makeQuery(id+"F2.opPattern","COPY",FACE,{"derivedFrom":subQ1,"instanceName":"9"}),makeQuery(id+"F2.opPattern","COPY",FACE,{"derivedFrom":subQ1,"instanceName":"10"}),makeQuery(id+"F2.opPattern","COPY",FACE,{"derivedFrom":subQ1,"instanceName":"11"}),makeQuery(id+"F2.opPattern","COPY",FACE,{"derivedFrom":subQ1,"instanceName":"12"}),makeQuery(id+"F2.opPattern","COPY",FACE,{"derivedFrom":subQ1,"instanceName":"13"}),makeQuery(id+"F2.opPattern","COPY",FACE,{"derivedFrom":subQ1,"instanceName":"14"}),makeQuery(id+"F2.opPattern","COPY",FACE,{"derivedFrom":subQ1,"instanceName":"15"}),makeQuery(id+"F2.opPattern","COPY",FACE,{"derivedFrom":subQ1,"instanceName":"16"}),makeQuery(id+"F2.opPattern","COPY",FACE,{"derivedFrom":subQ1,"instanceName":"17"}),makeQuery(id+"F2.opPattern","COPY",FACE,{"derivedFrom":subQ1,"instanceName":"18"}),makeQuery(id+"F2.opPattern","COPY",FACE,{"derivedFrom":subQ1,"instanceName":"19"}),makeQuery(id+"F2.opPattern","COPY",FACE,{"derivedFrom":subQ1,"instanceName":"20"}),makeQuery(id+"F2.opPattern","COPY",FACE,{"derivedFrom":subQ1,"instanceName":"21"}),makeQuery(id+"F2.opPattern","COPY",FACE,{"derivedFrom":subQ1,"instanceName":"22"}),makeQuery(id+"F2.opPattern","COPY",FACE,{"derivedFrom":subQ1,"instanceName":"23"})]})],"blendedInto":[makeQuery(id+"F2.boolean.opBoolean","MERGE",FACE,{"derivedFrom":[subQ1,makeQuery(id+"F2.opPattern","COPY",FACE,{"derivedFrom":subQ1,"instanceName":"1"}),makeQuery(id+"F2.opPattern","COPY",FACE,{"derivedFrom":subQ1,"instanceName":"2"}),makeQuery(id+"F2.opPattern","COPY",FACE,{"derivedFrom":subQ1,"instanceName":"3"}),makeQuery(id+"F2.opPattern","COPY",FACE,{"derivedFrom":subQ1,"instanceName":"4"}),makeQuery(id+"F2.opPattern","COPY",FACE,{"derivedFrom":subQ1,"instanceName":"5"}),makeQuery(id+"F2.opPattern","COPY",FACE,{"derivedFrom":subQ1,"instanceName":"6"}),makeQuery(id+"F2.opPattern","COPY",FACE,{"derivedFrom":subQ1,"instanceName":"7"}),makeQuery(id+"F2.opPattern","COPY",FACE,{"derivedFrom":subQ1,"instanceName":"8"}),makeQuery(id+"F2.opPattern","COPY",FACE,{"derivedFrom":subQ1,"instanceName":"9"}),makeQuery(id+"F2.opPattern","COPY",FACE,{"derivedFrom":subQ1,"instanceName":"10"}),makeQuery(id+"F2.opPattern","COPY",FACE,{"derivedFrom":subQ1,"instanceName":"11"}),makeQuery(id+"F2.opPattern","COPY",FACE,{"derivedFrom":subQ1,"instanceName":"12"}),makeQuery(id+"F2.opPattern","COPY",FACE,{"derivedFrom":subQ1,"instanceName":"13"}),makeQuery(id+"F2.opPattern","COPY",FACE,{"derivedFrom":subQ1,"instanceName":"14"}),makeQuery(id+"F2.opPattern","COPY",FACE,{"derivedFrom":subQ1,"instanceName":"15"}),makeQuery(id+"F2.opPattern","COPY",FACE,{"derivedFrom":subQ1,"instanceName":"16"}),makeQuery(id+"F2.opPattern","COPY",FACE,{"derivedFrom":subQ1,"instanceName":"17"}),makeQuery(id+"F2.opPattern","COPY",FACE,{"derivedFrom":subQ1,"instanceName":"18"}),makeQuery(id+"F2.opPattern","COPY",FACE,{"derivedFrom":subQ1,"instanceName":"19"}),makeQuery(id+"F2.opPattern","COPY",FACE,{"derivedFrom":subQ1,"instanceName":"20"}),makeQuery(id+"F2.opPattern","COPY",FACE,{"derivedFrom":subQ1,"instanceName":"21"}),makeQuery(id+"F2.opPattern","COPY",FACE,{"derivedFrom":subQ1,"instanceName":"22"}),makeQuery(id+"F2.opPattern","COPY",FACE,{"derivedFrom":subQ1,"instanceName":"23"})]})]});}
            var Q17;
            {var subQ0=sQuery(id+"F0.wireOp",EDGE,"E12");Q17=makeQuery(id+"F3.opFillet","BLEND_EDGE",EDGE,{"blendedFrom":[makeQuery(id+"F2.opPattern","COPY",EDGE,{"derivedFrom":makeQuery(id+"F1.opExtrude","CAP_EDGE",EDGE,{"disambiguationData":[OSD([subQ0])],"isStart":false}),"instanceName":"7"}),makeQuery(id+"F2.opPattern","COPY",FACE,{"derivedFrom":makeQuery(id+"F1.opExtrude","SWEPT_FACE",FACE,{"disambiguationData":[OSD([subQ0])]}),"instanceName":"7"})],"blendedInto":[makeQuery(id+"F2.opPattern","COPY",FACE,{"derivedFrom":makeQuery(id+"F1.opExtrude","SWEPT_FACE",FACE,{"disambiguationData":[OSD([subQ0])]}),"instanceName":"7"})]});}
            var Q18;
            {var subQ0=sQuery(id+"F0.wireOp",EDGE,"E14.MirrorCS");var subQ1=makeQuery(id+"F1.opExtrude","CAP_FACE",FACE,{"disambiguationData":[OSD([sQuery(id+"F0.wireOp",EDGE,"E2"),sQuery(id+"F0.wireOp",EDGE,"E11"),sQuery(id+"F0.wireOp",EDGE,"E12"),sQuery(id+"F0.wireOp",EDGE,"E13.MirrorCS"),subQ0,sQuery(id+"F0.wireOp",EDGE,"E15"),sQuery(id+"F0.wireOp",EDGE,"E19")])],"isStart":false});Q18=makeQuery(id+"F3.opFillet","BLEND_EDGE",EDGE,{"blendedFrom":[makeQuery(id+"F2.opPattern","COPY",EDGE,{"derivedFrom":makeQuery(id+"F1.opExtrude","CAP_EDGE",EDGE,{"disambiguationData":[OSD([subQ0])],"isStart":false}),"instanceName":"8"}),makeQuery(id+"F2.boolean.opBoolean","MERGE",FACE,{"derivedFrom":[subQ1,makeQuery(id+"F2.opPattern","COPY",FACE,{"derivedFrom":subQ1,"instanceName":"1"}),makeQuery(id+"F2.opPattern","COPY",FACE,{"derivedFrom":subQ1,"instanceName":"2"}),makeQuery(id+"F2.opPattern","COPY",FACE,{"derivedFrom":subQ1,"instanceName":"3"}),makeQuery(id+"F2.opPattern","COPY",FACE,{"derivedFrom":subQ1,"instanceName":"4"}),makeQuery(id+"F2.opPattern","COPY",FACE,{"derivedFrom":subQ1,"instanceName":"5"}),makeQuery(id+"F2.opPattern","COPY",FACE,{"derivedFrom":subQ1,"instanceName":"6"}),makeQuery(id+"F2.opPattern","COPY",FACE,{"derivedFrom":subQ1,"instanceName":"7"}),makeQuery(id+"F2.opPattern","COPY",FACE,{"derivedFrom":subQ1,"instanceName":"8"}),makeQuery(id+"F2.opPattern","COPY",FACE,{"derivedFrom":subQ1,"instanceName":"9"}),makeQuery(id+"F2.opPattern","COPY",FACE,{"derivedFrom":subQ1,"instanceName":"10"}),makeQuery(id+"F2.opPattern","COPY",FACE,{"derivedFrom":subQ1,"instanceName":"11"}),makeQuery(id+"F2.opPattern","COPY",FACE,{"derivedFrom":subQ1,"instanceName":"12"}),makeQuery(id+"F2.opPattern","COPY",FACE,{"derivedFrom":subQ1,"instanceName":"13"}),makeQuery(id+"F2.opPattern","COPY",FACE,{"derivedFrom":subQ1,"instanceName":"14"}),makeQuery(id+"F2.opPattern","COPY",FACE,{"derivedFrom":subQ1,"instanceName":"15"}),makeQuery(id+"F2.opPattern","COPY",FACE,{"derivedFrom":subQ1,"instanceName":"16"}),makeQuery(id+"F2.opPattern","COPY",FACE,{"derivedFrom":subQ1,"instanceName":"17"}),makeQuery(id+"F2.opPattern","COPY",FACE,{"derivedFrom":subQ1,"instanceName":"18"}),makeQuery(id+"F2.opPattern","COPY",FACE,{"derivedFrom":subQ1,"instanceName":"19"}),makeQuery(id+"F2.opPattern","COPY",FACE,{"derivedFrom":subQ1,"instanceName":"20"}),makeQuery(id+"F2.opPattern","COPY",FACE,{"derivedFrom":subQ1,"instanceName":"21"}),makeQuery(id+"F2.opPattern","COPY",FACE,{"derivedFrom":subQ1,"instanceName":"22"}),makeQuery(id+"F2.opPattern","COPY",FACE,{"derivedFrom":subQ1,"instanceName":"23"})]})],"blendedInto":[makeQuery(id+"F2.boolean.opBoolean","MERGE",FACE,{"derivedFrom":[subQ1,makeQuery(id+"F2.opPattern","COPY",FACE,{"derivedFrom":subQ1,"instanceName":"1"}),makeQuery(id+"F2.opPattern","COPY",FACE,{"derivedFrom":subQ1,"instanceName":"2"}),makeQuery(id+"F2.opPattern","COPY",FACE,{"derivedFrom":subQ1,"instanceName":"3"}),makeQuery(id+"F2.opPattern","COPY",FACE,{"derivedFrom":subQ1,"instanceName":"4"}),makeQuery(id+"F2.opPattern","COPY",FACE,{"derivedFrom":subQ1,"instanceName":"5"}),makeQuery(id+"F2.opPattern","COPY",FACE,{"derivedFrom":subQ1,"instanceName":"6"}),makeQuery(id+"F2.opPattern","COPY",FACE,{"derivedFrom":subQ1,"instanceName":"7"}),makeQuery(id+"F2.opPattern","COPY",FACE,{"derivedFrom":subQ1,"instanceName":"8"}),makeQuery(id+"F2.opPattern","COPY",FACE,{"derivedFrom":subQ1,"instanceName":"9"}),makeQuery(id+"F2.opPattern","COPY",FACE,{"derivedFrom":subQ1,"instanceName":"10"}),makeQuery(id+"F2.opPattern","COPY",FACE,{"derivedFrom":subQ1,"instanceName":"11"}),makeQuery(id+"F2.opPattern","COPY",FACE,{"derivedFrom":subQ1,"instanceName":"12"}),makeQuery(id+"F2.opPattern","COPY",FACE,{"derivedFrom":subQ1,"instanceName":"13"}),makeQuery(id+"F2.opPattern","COPY",FACE,{"derivedFrom":subQ1,"instanceName":"14"}),makeQuery(id+"F2.opPattern","COPY",FACE,{"derivedFrom":subQ1,"instanceName":"15"}),makeQuery(id+"F2.opPattern","COPY",FACE,{"derivedFrom":subQ1,"instanceName":"16"}),makeQuery(id+"F2.opPattern","COPY",FACE,{"derivedFrom":subQ1,"instanceName":"17"}),makeQuery(id+"F2.opPattern","COPY",FACE,{"derivedFrom":subQ1,"instanceName":"18"}),makeQuery(id+"F2.opPattern","COPY",FACE,{"derivedFrom":subQ1,"instanceName":"19"}),makeQuery(id+"F2.opPattern","COPY",FACE,{"derivedFrom":subQ1,"instanceName":"20"}),makeQuery(id+"F2.opPattern","COPY",FACE,{"derivedFrom":subQ1,"instanceName":"21"}),makeQuery(id+"F2.opPattern","COPY",FACE,{"derivedFrom":subQ1,"instanceName":"22"}),makeQuery(id+"F2.opPattern","COPY",FACE,{"derivedFrom":subQ1,"instanceName":"23"})]})]});}
            var Q19;
            {var subQ0=sQuery(id+"F0.wireOp",EDGE,"E12");var subQ1=makeQuery(id+"F1.opExtrude","CAP_FACE",FACE,{"disambiguationData":[OSD([sQuery(id+"F0.wireOp",EDGE,"E2"),sQuery(id+"F0.wireOp",EDGE,"E11"),subQ0,sQuery(id+"F0.wireOp",EDGE,"E13.MirrorCS"),sQuery(id+"F0.wireOp",EDGE,"E14.MirrorCS"),sQuery(id+"F0.wireOp",EDGE,"E15"),sQuery(id+"F0.wireOp",EDGE,"E19")])],"isStart":false});Q19=makeQuery(id+"F3.opFillet","BLEND_EDGE",EDGE,{"blendedFrom":[makeQuery(id+"F2.opPattern","COPY",EDGE,{"derivedFrom":makeQuery(id+"F1.opExtrude","CAP_EDGE",EDGE,{"disambiguationData":[OSD([subQ0])],"isStart":false}),"instanceName":"8"}),makeQuery(id+"F2.boolean.opBoolean","MERGE",FACE,{"derivedFrom":[subQ1,makeQuery(id+"F2.opPattern","COPY",FACE,{"derivedFrom":subQ1,"instanceName":"1"}),makeQuery(id+"F2.opPattern","COPY",FACE,{"derivedFrom":subQ1,"instanceName":"2"}),makeQuery(id+"F2.opPattern","COPY",FACE,{"derivedFrom":subQ1,"instanceName":"3"}),makeQuery(id+"F2.opPattern","COPY",FACE,{"derivedFrom":subQ1,"instanceName":"4"}),makeQuery(id+"F2.opPattern","COPY",FACE,{"derivedFrom":subQ1,"instanceName":"5"}),makeQuery(id+"F2.opPattern","COPY",FACE,{"derivedFrom":subQ1,"instanceName":"6"}),makeQuery(id+"F2.opPattern","COPY",FACE,{"derivedFrom":subQ1,"instanceName":"7"}),makeQuery(id+"F2.opPattern","COPY",FACE,{"derivedFrom":subQ1,"instanceName":"8"}),makeQuery(id+"F2.opPattern","COPY",FACE,{"derivedFrom":subQ1,"instanceName":"9"}),makeQuery(id+"F2.opPattern","COPY",FACE,{"derivedFrom":subQ1,"instanceName":"10"}),makeQuery(id+"F2.opPattern","COPY",FACE,{"derivedFrom":subQ1,"instanceName":"11"}),makeQuery(id+"F2.opPattern","COPY",FACE,{"derivedFrom":subQ1,"instanceName":"12"}),makeQuery(id+"F2.opPattern","COPY",FACE,{"derivedFrom":subQ1,"instanceName":"13"}),makeQuery(id+"F2.opPattern","COPY",FACE,{"derivedFrom":subQ1,"instanceName":"14"}),makeQuery(id+"F2.opPattern","COPY",FACE,{"derivedFrom":subQ1,"instanceName":"15"}),makeQuery(id+"F2.opPattern","COPY",FACE,{"derivedFrom":subQ1,"instanceName":"16"}),makeQuery(id+"F2.opPattern","COPY",FACE,{"derivedFrom":subQ1,"instanceName":"17"}),makeQuery(id+"F2.opPattern","COPY",FACE,{"derivedFrom":subQ1,"instanceName":"18"}),makeQuery(id+"F2.opPattern","COPY",FACE,{"derivedFrom":subQ1,"instanceName":"19"}),makeQuery(id+"F2.opPattern","COPY",FACE,{"derivedFrom":subQ1,"instanceName":"20"}),makeQuery(id+"F2.opPattern","COPY",FACE,{"derivedFrom":subQ1,"instanceName":"21"}),makeQuery(id+"F2.opPattern","COPY",FACE,{"derivedFrom":subQ1,"instanceName":"22"}),makeQuery(id+"F2.opPattern","COPY",FACE,{"derivedFrom":subQ1,"instanceName":"23"})]})],"blendedInto":[makeQuery(id+"F2.boolean.opBoolean","MERGE",FACE,{"derivedFrom":[subQ1,makeQuery(id+"F2.opPattern","COPY",FACE,{"derivedFrom":subQ1,"instanceName":"1"}),makeQuery(id+"F2.opPattern","COPY",FACE,{"derivedFrom":subQ1,"instanceName":"2"}),makeQuery(id+"F2.opPattern","COPY",FACE,{"derivedFrom":subQ1,"instanceName":"3"}),makeQuery(id+"F2.opPattern","COPY",FACE,{"derivedFrom":subQ1,"instanceName":"4"}),makeQuery(id+"F2.opPattern","COPY",FACE,{"derivedFrom":subQ1,"instanceName":"5"}),makeQuery(id+"F2.opPattern","COPY",FACE,{"derivedFrom":subQ1,"instanceName":"6"}),makeQuery(id+"F2.opPattern","COPY",FACE,{"derivedFrom":subQ1,"instanceName":"7"}),makeQuery(id+"F2.opPattern","COPY",FACE,{"derivedFrom":subQ1,"instanceName":"8"}),makeQuery(id+"F2.opPattern","COPY",FACE,{"derivedFrom":subQ1,"instanceName":"9"}),makeQuery(id+"F2.opPattern","COPY",FACE,{"derivedFrom":subQ1,"instanceName":"10"}),makeQuery(id+"F2.opPattern","COPY",FACE,{"derivedFrom":subQ1,"instanceName":"11"}),makeQuery(id+"F2.opPattern","COPY",FACE,{"derivedFrom":subQ1,"instanceName":"12"}),makeQuery(id+"F2.opPattern","COPY",FACE,{"derivedFrom":subQ1,"instanceName":"13"}),makeQuery(id+"F2.opPattern","COPY",FACE,{"derivedFrom":subQ1,"instanceName":"14"}),makeQuery(id+"F2.opPattern","COPY",FACE,{"derivedFrom":subQ1,"instanceName":"15"}),makeQuery(id+"F2.opPattern","COPY",FACE,{"derivedFrom":subQ1,"instanceName":"16"}),makeQuery(id+"F2.opPattern","COPY",FACE,{"derivedFrom":subQ1,"instanceName":"17"}),makeQuery(id+"F2.opPattern","COPY",FACE,{"derivedFrom":subQ1,"instanceName":"18"}),makeQuery(id+"F2.opPattern","COPY",FACE,{"derivedFrom":subQ1,"instanceName":"19"}),makeQuery(id+"F2.opPattern","COPY",FACE,{"derivedFrom":subQ1,"instanceName":"20"}),makeQuery(id+"F2.opPattern","COPY",FACE,{"derivedFrom":subQ1,"instanceName":"21"}),makeQuery(id+"F2.opPattern","COPY",FACE,{"derivedFrom":subQ1,"instanceName":"22"}),makeQuery(id+"F2.opPattern","COPY",FACE,{"derivedFrom":subQ1,"instanceName":"23"})]})]});}
            var Q20;
            {var subQ0=sQuery(id+"F0.wireOp",EDGE,"E14.MirrorCS");var subQ1=makeQuery(id+"F1.opExtrude","CAP_FACE",FACE,{"disambiguationData":[OSD([sQuery(id+"F0.wireOp",EDGE,"E2"),sQuery(id+"F0.wireOp",EDGE,"E11"),sQuery(id+"F0.wireOp",EDGE,"E12"),sQuery(id+"F0.wireOp",EDGE,"E13.MirrorCS"),subQ0,sQuery(id+"F0.wireOp",EDGE,"E15"),sQuery(id+"F0.wireOp",EDGE,"E19")])],"isStart":false});Q20=makeQuery(id+"F3.opFillet","BLEND_EDGE",EDGE,{"blendedFrom":[makeQuery(id+"F2.opPattern","COPY",EDGE,{"derivedFrom":makeQuery(id+"F1.opExtrude","CAP_EDGE",EDGE,{"disambiguationData":[OSD([subQ0])],"isStart":false}),"instanceName":"9"}),makeQuery(id+"F2.boolean.opBoolean","MERGE",FACE,{"derivedFrom":[subQ1,makeQuery(id+"F2.opPattern","COPY",FACE,{"derivedFrom":subQ1,"instanceName":"1"}),makeQuery(id+"F2.opPattern","COPY",FACE,{"derivedFrom":subQ1,"instanceName":"2"}),makeQuery(id+"F2.opPattern","COPY",FACE,{"derivedFrom":subQ1,"instanceName":"3"}),makeQuery(id+"F2.opPattern","COPY",FACE,{"derivedFrom":subQ1,"instanceName":"4"}),makeQuery(id+"F2.opPattern","COPY",FACE,{"derivedFrom":subQ1,"instanceName":"5"}),makeQuery(id+"F2.opPattern","COPY",FACE,{"derivedFrom":subQ1,"instanceName":"6"}),makeQuery(id+"F2.opPattern","COPY",FACE,{"derivedFrom":subQ1,"instanceName":"7"}),makeQuery(id+"F2.opPattern","COPY",FACE,{"derivedFrom":subQ1,"instanceName":"8"}),makeQuery(id+"F2.opPattern","COPY",FACE,{"derivedFrom":subQ1,"instanceName":"9"}),makeQuery(id+"F2.opPattern","COPY",FACE,{"derivedFrom":subQ1,"instanceName":"10"}),makeQuery(id+"F2.opPattern","COPY",FACE,{"derivedFrom":subQ1,"instanceName":"11"}),makeQuery(id+"F2.opPattern","COPY",FACE,{"derivedFrom":subQ1,"instanceName":"12"}),makeQuery(id+"F2.opPattern","COPY",FACE,{"derivedFrom":subQ1,"instanceName":"13"}),makeQuery(id+"F2.opPattern","COPY",FACE,{"derivedFrom":subQ1,"instanceName":"14"}),makeQuery(id+"F2.opPattern","COPY",FACE,{"derivedFrom":subQ1,"instanceName":"15"}),makeQuery(id+"F2.opPattern","COPY",FACE,{"derivedFrom":subQ1,"instanceName":"16"}),makeQuery(id+"F2.opPattern","COPY",FACE,{"derivedFrom":subQ1,"instanceName":"17"}),makeQuery(id+"F2.opPattern","COPY",FACE,{"derivedFrom":subQ1,"instanceName":"18"}),makeQuery(id+"F2.opPattern","COPY",FACE,{"derivedFrom":subQ1,"instanceName":"19"}),makeQuery(id+"F2.opPattern","COPY",FACE,{"derivedFrom":subQ1,"instanceName":"20"}),makeQuery(id+"F2.opPattern","COPY",FACE,{"derivedFrom":subQ1,"instanceName":"21"}),makeQuery(id+"F2.opPattern","COPY",FACE,{"derivedFrom":subQ1,"instanceName":"22"}),makeQuery(id+"F2.opPattern","COPY",FACE,{"derivedFrom":subQ1,"instanceName":"23"})]})],"blendedInto":[makeQuery(id+"F2.boolean.opBoolean","MERGE",FACE,{"derivedFrom":[subQ1,makeQuery(id+"F2.opPattern","COPY",FACE,{"derivedFrom":subQ1,"instanceName":"1"}),makeQuery(id+"F2.opPattern","COPY",FACE,{"derivedFrom":subQ1,"instanceName":"2"}),makeQuery(id+"F2.opPattern","COPY",FACE,{"derivedFrom":subQ1,"instanceName":"3"}),makeQuery(id+"F2.opPattern","COPY",FACE,{"derivedFrom":subQ1,"instanceName":"4"}),makeQuery(id+"F2.opPattern","COPY",FACE,{"derivedFrom":subQ1,"instanceName":"5"}),makeQuery(id+"F2.opPattern","COPY",FACE,{"derivedFrom":subQ1,"instanceName":"6"}),makeQuery(id+"F2.opPattern","COPY",FACE,{"derivedFrom":subQ1,"instanceName":"7"}),makeQuery(id+"F2.opPattern","COPY",FACE,{"derivedFrom":subQ1,"instanceName":"8"}),makeQuery(id+"F2.opPattern","COPY",FACE,{"derivedFrom":subQ1,"instanceName":"9"}),makeQuery(id+"F2.opPattern","COPY",FACE,{"derivedFrom":subQ1,"instanceName":"10"}),makeQuery(id+"F2.opPattern","COPY",FACE,{"derivedFrom":subQ1,"instanceName":"11"}),makeQuery(id+"F2.opPattern","COPY",FACE,{"derivedFrom":subQ1,"instanceName":"12"}),makeQuery(id+"F2.opPattern","COPY",FACE,{"derivedFrom":subQ1,"instanceName":"13"}),makeQuery(id+"F2.opPattern","COPY",FACE,{"derivedFrom":subQ1,"instanceName":"14"}),makeQuery(id+"F2.opPattern","COPY",FACE,{"derivedFrom":subQ1,"instanceName":"15"}),makeQuery(id+"F2.opPattern","COPY",FACE,{"derivedFrom":subQ1,"instanceName":"16"}),makeQuery(id+"F2.opPattern","COPY",FACE,{"derivedFrom":subQ1,"instanceName":"17"}),makeQuery(id+"F2.opPattern","COPY",FACE,{"derivedFrom":subQ1,"instanceName":"18"}),makeQuery(id+"F2.opPattern","COPY",FACE,{"derivedFrom":subQ1,"instanceName":"19"}),makeQuery(id+"F2.opPattern","COPY",FACE,{"derivedFrom":subQ1,"instanceName":"20"}),makeQuery(id+"F2.opPattern","COPY",FACE,{"derivedFrom":subQ1,"instanceName":"21"}),makeQuery(id+"F2.opPattern","COPY",FACE,{"derivedFrom":subQ1,"instanceName":"22"}),makeQuery(id+"F2.opPattern","COPY",FACE,{"derivedFrom":subQ1,"instanceName":"23"})]})]});}
            var Q21;
            {var subQ0=sQuery(id+"F0.wireOp",EDGE,"E12");var subQ1=makeQuery(id+"F1.opExtrude","CAP_FACE",FACE,{"disambiguationData":[OSD([sQuery(id+"F0.wireOp",EDGE,"E2"),sQuery(id+"F0.wireOp",EDGE,"E11"),subQ0,sQuery(id+"F0.wireOp",EDGE,"E13.MirrorCS"),sQuery(id+"F0.wireOp",EDGE,"E14.MirrorCS"),sQuery(id+"F0.wireOp",EDGE,"E15"),sQuery(id+"F0.wireOp",EDGE,"E19")])],"isStart":false});Q21=makeQuery(id+"F3.opFillet","BLEND_EDGE",EDGE,{"blendedFrom":[makeQuery(id+"F2.opPattern","COPY",EDGE,{"derivedFrom":makeQuery(id+"F1.opExtrude","CAP_EDGE",EDGE,{"disambiguationData":[OSD([subQ0])],"isStart":false}),"instanceName":"9"}),makeQuery(id+"F2.boolean.opBoolean","MERGE",FACE,{"derivedFrom":[subQ1,makeQuery(id+"F2.opPattern","COPY",FACE,{"derivedFrom":subQ1,"instanceName":"1"}),makeQuery(id+"F2.opPattern","COPY",FACE,{"derivedFrom":subQ1,"instanceName":"2"}),makeQuery(id+"F2.opPattern","COPY",FACE,{"derivedFrom":subQ1,"instanceName":"3"}),makeQuery(id+"F2.opPattern","COPY",FACE,{"derivedFrom":subQ1,"instanceName":"4"}),makeQuery(id+"F2.opPattern","COPY",FACE,{"derivedFrom":subQ1,"instanceName":"5"}),makeQuery(id+"F2.opPattern","COPY",FACE,{"derivedFrom":subQ1,"instanceName":"6"}),makeQuery(id+"F2.opPattern","COPY",FACE,{"derivedFrom":subQ1,"instanceName":"7"}),makeQuery(id+"F2.opPattern","COPY",FACE,{"derivedFrom":subQ1,"instanceName":"8"}),makeQuery(id+"F2.opPattern","COPY",FACE,{"derivedFrom":subQ1,"instanceName":"9"}),makeQuery(id+"F2.opPattern","COPY",FACE,{"derivedFrom":subQ1,"instanceName":"10"}),makeQuery(id+"F2.opPattern","COPY",FACE,{"derivedFrom":subQ1,"instanceName":"11"}),makeQuery(id+"F2.opPattern","COPY",FACE,{"derivedFrom":subQ1,"instanceName":"12"}),makeQuery(id+"F2.opPattern","COPY",FACE,{"derivedFrom":subQ1,"instanceName":"13"}),makeQuery(id+"F2.opPattern","COPY",FACE,{"derivedFrom":subQ1,"instanceName":"14"}),makeQuery(id+"F2.opPattern","COPY",FACE,{"derivedFrom":subQ1,"instanceName":"15"}),makeQuery(id+"F2.opPattern","COPY",FACE,{"derivedFrom":subQ1,"instanceName":"16"}),makeQuery(id+"F2.opPattern","COPY",FACE,{"derivedFrom":subQ1,"instanceName":"17"}),makeQuery(id+"F2.opPattern","COPY",FACE,{"derivedFrom":subQ1,"instanceName":"18"}),makeQuery(id+"F2.opPattern","COPY",FACE,{"derivedFrom":subQ1,"instanceName":"19"}),makeQuery(id+"F2.opPattern","COPY",FACE,{"derivedFrom":subQ1,"instanceName":"20"}),makeQuery(id+"F2.opPattern","COPY",FACE,{"derivedFrom":subQ1,"instanceName":"21"}),makeQuery(id+"F2.opPattern","COPY",FACE,{"derivedFrom":subQ1,"instanceName":"22"}),makeQuery(id+"F2.opPattern","COPY",FACE,{"derivedFrom":subQ1,"instanceName":"23"})]})],"blendedInto":[makeQuery(id+"F2.boolean.opBoolean","MERGE",FACE,{"derivedFrom":[subQ1,makeQuery(id+"F2.opPattern","COPY",FACE,{"derivedFrom":subQ1,"instanceName":"1"}),makeQuery(id+"F2.opPattern","COPY",FACE,{"derivedFrom":subQ1,"instanceName":"2"}),makeQuery(id+"F2.opPattern","COPY",FACE,{"derivedFrom":subQ1,"instanceName":"3"}),makeQuery(id+"F2.opPattern","COPY",FACE,{"derivedFrom":subQ1,"instanceName":"4"}),makeQuery(id+"F2.opPattern","COPY",FACE,{"derivedFrom":subQ1,"instanceName":"5"}),makeQuery(id+"F2.opPattern","COPY",FACE,{"derivedFrom":subQ1,"instanceName":"6"}),makeQuery(id+"F2.opPattern","COPY",FACE,{"derivedFrom":subQ1,"instanceName":"7"}),makeQuery(id+"F2.opPattern","COPY",FACE,{"derivedFrom":subQ1,"instanceName":"8"}),makeQuery(id+"F2.opPattern","COPY",FACE,{"derivedFrom":subQ1,"instanceName":"9"}),makeQuery(id+"F2.opPattern","COPY",FACE,{"derivedFrom":subQ1,"instanceName":"10"}),makeQuery(id+"F2.opPattern","COPY",FACE,{"derivedFrom":subQ1,"instanceName":"11"}),makeQuery(id+"F2.opPattern","COPY",FACE,{"derivedFrom":subQ1,"instanceName":"12"}),makeQuery(id+"F2.opPattern","COPY",FACE,{"derivedFrom":subQ1,"instanceName":"13"}),makeQuery(id+"F2.opPattern","COPY",FACE,{"derivedFrom":subQ1,"instanceName":"14"}),makeQuery(id+"F2.opPattern","COPY",FACE,{"derivedFrom":subQ1,"instanceName":"15"}),makeQuery(id+"F2.opPattern","COPY",FACE,{"derivedFrom":subQ1,"instanceName":"16"}),makeQuery(id+"F2.opPattern","COPY",FACE,{"derivedFrom":subQ1,"instanceName":"17"}),makeQuery(id+"F2.opPattern","COPY",FACE,{"derivedFrom":subQ1,"instanceName":"18"}),makeQuery(id+"F2.opPattern","COPY",FACE,{"derivedFrom":subQ1,"instanceName":"19"}),makeQuery(id+"F2.opPattern","COPY",FACE,{"derivedFrom":subQ1,"instanceName":"20"}),makeQuery(id+"F2.opPattern","COPY",FACE,{"derivedFrom":subQ1,"instanceName":"21"}),makeQuery(id+"F2.opPattern","COPY",FACE,{"derivedFrom":subQ1,"instanceName":"22"}),makeQuery(id+"F2.opPattern","COPY",FACE,{"derivedFrom":subQ1,"instanceName":"23"})]})]});}
            var Q22;
            {var subQ0=sQuery(id+"F0.wireOp",EDGE,"E14.MirrorCS");var subQ1=makeQuery(id+"F1.opExtrude","CAP_FACE",FACE,{"disambiguationData":[OSD([sQuery(id+"F0.wireOp",EDGE,"E2"),sQuery(id+"F0.wireOp",EDGE,"E11"),sQuery(id+"F0.wireOp",EDGE,"E12"),sQuery(id+"F0.wireOp",EDGE,"E13.MirrorCS"),subQ0,sQuery(id+"F0.wireOp",EDGE,"E15"),sQuery(id+"F0.wireOp",EDGE,"E19")])],"isStart":false});Q22=makeQuery(id+"F3.opFillet","BLEND_EDGE",EDGE,{"blendedFrom":[makeQuery(id+"F2.opPattern","COPY",EDGE,{"derivedFrom":makeQuery(id+"F1.opExtrude","CAP_EDGE",EDGE,{"disambiguationData":[OSD([subQ0])],"isStart":false}),"instanceName":"10"}),makeQuery(id+"F2.boolean.opBoolean","MERGE",FACE,{"derivedFrom":[subQ1,makeQuery(id+"F2.opPattern","COPY",FACE,{"derivedFrom":subQ1,"instanceName":"1"}),makeQuery(id+"F2.opPattern","COPY",FACE,{"derivedFrom":subQ1,"instanceName":"2"}),makeQuery(id+"F2.opPattern","COPY",FACE,{"derivedFrom":subQ1,"instanceName":"3"}),makeQuery(id+"F2.opPattern","COPY",FACE,{"derivedFrom":subQ1,"instanceName":"4"}),makeQuery(id+"F2.opPattern","COPY",FACE,{"derivedFrom":subQ1,"instanceName":"5"}),makeQuery(id+"F2.opPattern","COPY",FACE,{"derivedFrom":subQ1,"instanceName":"6"}),makeQuery(id+"F2.opPattern","COPY",FACE,{"derivedFrom":subQ1,"instanceName":"7"}),makeQuery(id+"F2.opPattern","COPY",FACE,{"derivedFrom":subQ1,"instanceName":"8"}),makeQuery(id+"F2.opPattern","COPY",FACE,{"derivedFrom":subQ1,"instanceName":"9"}),makeQuery(id+"F2.opPattern","COPY",FACE,{"derivedFrom":subQ1,"instanceName":"10"}),makeQuery(id+"F2.opPattern","COPY",FACE,{"derivedFrom":subQ1,"instanceName":"11"}),makeQuery(id+"F2.opPattern","COPY",FACE,{"derivedFrom":subQ1,"instanceName":"12"}),makeQuery(id+"F2.opPattern","COPY",FACE,{"derivedFrom":subQ1,"instanceName":"13"}),makeQuery(id+"F2.opPattern","COPY",FACE,{"derivedFrom":subQ1,"instanceName":"14"}),makeQuery(id+"F2.opPattern","COPY",FACE,{"derivedFrom":subQ1,"instanceName":"15"}),makeQuery(id+"F2.opPattern","COPY",FACE,{"derivedFrom":subQ1,"instanceName":"16"}),makeQuery(id+"F2.opPattern","COPY",FACE,{"derivedFrom":subQ1,"instanceName":"17"}),makeQuery(id+"F2.opPattern","COPY",FACE,{"derivedFrom":subQ1,"instanceName":"18"}),makeQuery(id+"F2.opPattern","COPY",FACE,{"derivedFrom":subQ1,"instanceName":"19"}),makeQuery(id+"F2.opPattern","COPY",FACE,{"derivedFrom":subQ1,"instanceName":"20"}),makeQuery(id+"F2.opPattern","COPY",FACE,{"derivedFrom":subQ1,"instanceName":"21"}),makeQuery(id+"F2.opPattern","COPY",FACE,{"derivedFrom":subQ1,"instanceName":"22"}),makeQuery(id+"F2.opPattern","COPY",FACE,{"derivedFrom":subQ1,"instanceName":"23"})]})],"blendedInto":[makeQuery(id+"F2.boolean.opBoolean","MERGE",FACE,{"derivedFrom":[subQ1,makeQuery(id+"F2.opPattern","COPY",FACE,{"derivedFrom":subQ1,"instanceName":"1"}),makeQuery(id+"F2.opPattern","COPY",FACE,{"derivedFrom":subQ1,"instanceName":"2"}),makeQuery(id+"F2.opPattern","COPY",FACE,{"derivedFrom":subQ1,"instanceName":"3"}),makeQuery(id+"F2.opPattern","COPY",FACE,{"derivedFrom":subQ1,"instanceName":"4"}),makeQuery(id+"F2.opPattern","COPY",FACE,{"derivedFrom":subQ1,"instanceName":"5"}),makeQuery(id+"F2.opPattern","COPY",FACE,{"derivedFrom":subQ1,"instanceName":"6"}),makeQuery(id+"F2.opPattern","COPY",FACE,{"derivedFrom":subQ1,"instanceName":"7"}),makeQuery(id+"F2.opPattern","COPY",FACE,{"derivedFrom":subQ1,"instanceName":"8"}),makeQuery(id+"F2.opPattern","COPY",FACE,{"derivedFrom":subQ1,"instanceName":"9"}),makeQuery(id+"F2.opPattern","COPY",FACE,{"derivedFrom":subQ1,"instanceName":"10"}),makeQuery(id+"F2.opPattern","COPY",FACE,{"derivedFrom":subQ1,"instanceName":"11"}),makeQuery(id+"F2.opPattern","COPY",FACE,{"derivedFrom":subQ1,"instanceName":"12"}),makeQuery(id+"F2.opPattern","COPY",FACE,{"derivedFrom":subQ1,"instanceName":"13"}),makeQuery(id+"F2.opPattern","COPY",FACE,{"derivedFrom":subQ1,"instanceName":"14"}),makeQuery(id+"F2.opPattern","COPY",FACE,{"derivedFrom":subQ1,"instanceName":"15"}),makeQuery(id+"F2.opPattern","COPY",FACE,{"derivedFrom":subQ1,"instanceName":"16"}),makeQuery(id+"F2.opPattern","COPY",FACE,{"derivedFrom":subQ1,"instanceName":"17"}),makeQuery(id+"F2.opPattern","COPY",FACE,{"derivedFrom":subQ1,"instanceName":"18"}),makeQuery(id+"F2.opPattern","COPY",FACE,{"derivedFrom":subQ1,"instanceName":"19"}),makeQuery(id+"F2.opPattern","COPY",FACE,{"derivedFrom":subQ1,"instanceName":"20"}),makeQuery(id+"F2.opPattern","COPY",FACE,{"derivedFrom":subQ1,"instanceName":"21"}),makeQuery(id+"F2.opPattern","COPY",FACE,{"derivedFrom":subQ1,"instanceName":"22"}),makeQuery(id+"F2.opPattern","COPY",FACE,{"derivedFrom":subQ1,"instanceName":"23"})]})]});}
            var Q23;
            {var subQ0=sQuery(id+"F0.wireOp",EDGE,"E12");var subQ1=makeQuery(id+"F1.opExtrude","CAP_FACE",FACE,{"disambiguationData":[OSD([sQuery(id+"F0.wireOp",EDGE,"E2"),sQuery(id+"F0.wireOp",EDGE,"E11"),subQ0,sQuery(id+"F0.wireOp",EDGE,"E13.MirrorCS"),sQuery(id+"F0.wireOp",EDGE,"E14.MirrorCS"),sQuery(id+"F0.wireOp",EDGE,"E15"),sQuery(id+"F0.wireOp",EDGE,"E19")])],"isStart":false});Q23=makeQuery(id+"F3.opFillet","BLEND_EDGE",EDGE,{"blendedFrom":[makeQuery(id+"F2.opPattern","COPY",EDGE,{"derivedFrom":makeQuery(id+"F1.opExtrude","CAP_EDGE",EDGE,{"disambiguationData":[OSD([subQ0])],"isStart":false}),"instanceName":"10"}),makeQuery(id+"F2.boolean.opBoolean","MERGE",FACE,{"derivedFrom":[subQ1,makeQuery(id+"F2.opPattern","COPY",FACE,{"derivedFrom":subQ1,"instanceName":"1"}),makeQuery(id+"F2.opPattern","COPY",FACE,{"derivedFrom":subQ1,"instanceName":"2"}),makeQuery(id+"F2.opPattern","COPY",FACE,{"derivedFrom":subQ1,"instanceName":"3"}),makeQuery(id+"F2.opPattern","COPY",FACE,{"derivedFrom":subQ1,"instanceName":"4"}),makeQuery(id+"F2.opPattern","COPY",FACE,{"derivedFrom":subQ1,"instanceName":"5"}),makeQuery(id+"F2.opPattern","COPY",FACE,{"derivedFrom":subQ1,"instanceName":"6"}),makeQuery(id+"F2.opPattern","COPY",FACE,{"derivedFrom":subQ1,"instanceName":"7"}),makeQuery(id+"F2.opPattern","COPY",FACE,{"derivedFrom":subQ1,"instanceName":"8"}),makeQuery(id+"F2.opPattern","COPY",FACE,{"derivedFrom":subQ1,"instanceName":"9"}),makeQuery(id+"F2.opPattern","COPY",FACE,{"derivedFrom":subQ1,"instanceName":"10"}),makeQuery(id+"F2.opPattern","COPY",FACE,{"derivedFrom":subQ1,"instanceName":"11"}),makeQuery(id+"F2.opPattern","COPY",FACE,{"derivedFrom":subQ1,"instanceName":"12"}),makeQuery(id+"F2.opPattern","COPY",FACE,{"derivedFrom":subQ1,"instanceName":"13"}),makeQuery(id+"F2.opPattern","COPY",FACE,{"derivedFrom":subQ1,"instanceName":"14"}),makeQuery(id+"F2.opPattern","COPY",FACE,{"derivedFrom":subQ1,"instanceName":"15"}),makeQuery(id+"F2.opPattern","COPY",FACE,{"derivedFrom":subQ1,"instanceName":"16"}),makeQuery(id+"F2.opPattern","COPY",FACE,{"derivedFrom":subQ1,"instanceName":"17"}),makeQuery(id+"F2.opPattern","COPY",FACE,{"derivedFrom":subQ1,"instanceName":"18"}),makeQuery(id+"F2.opPattern","COPY",FACE,{"derivedFrom":subQ1,"instanceName":"19"}),makeQuery(id+"F2.opPattern","COPY",FACE,{"derivedFrom":subQ1,"instanceName":"20"}),makeQuery(id+"F2.opPattern","COPY",FACE,{"derivedFrom":subQ1,"instanceName":"21"}),makeQuery(id+"F2.opPattern","COPY",FACE,{"derivedFrom":subQ1,"instanceName":"22"}),makeQuery(id+"F2.opPattern","COPY",FACE,{"derivedFrom":subQ1,"instanceName":"23"})]})],"blendedInto":[makeQuery(id+"F2.boolean.opBoolean","MERGE",FACE,{"derivedFrom":[subQ1,makeQuery(id+"F2.opPattern","COPY",FACE,{"derivedFrom":subQ1,"instanceName":"1"}),makeQuery(id+"F2.opPattern","COPY",FACE,{"derivedFrom":subQ1,"instanceName":"2"}),makeQuery(id+"F2.opPattern","COPY",FACE,{"derivedFrom":subQ1,"instanceName":"3"}),makeQuery(id+"F2.opPattern","COPY",FACE,{"derivedFrom":subQ1,"instanceName":"4"}),makeQuery(id+"F2.opPattern","COPY",FACE,{"derivedFrom":subQ1,"instanceName":"5"}),makeQuery(id+"F2.opPattern","COPY",FACE,{"derivedFrom":subQ1,"instanceName":"6"}),makeQuery(id+"F2.opPattern","COPY",FACE,{"derivedFrom":subQ1,"instanceName":"7"}),makeQuery(id+"F2.opPattern","COPY",FACE,{"derivedFrom":subQ1,"instanceName":"8"}),makeQuery(id+"F2.opPattern","COPY",FACE,{"derivedFrom":subQ1,"instanceName":"9"}),makeQuery(id+"F2.opPattern","COPY",FACE,{"derivedFrom":subQ1,"instanceName":"10"}),makeQuery(id+"F2.opPattern","COPY",FACE,{"derivedFrom":subQ1,"instanceName":"11"}),makeQuery(id+"F2.opPattern","COPY",FACE,{"derivedFrom":subQ1,"instanceName":"12"}),makeQuery(id+"F2.opPattern","COPY",FACE,{"derivedFrom":subQ1,"instanceName":"13"}),makeQuery(id+"F2.opPattern","COPY",FACE,{"derivedFrom":subQ1,"instanceName":"14"}),makeQuery(id+"F2.opPattern","COPY",FACE,{"derivedFrom":subQ1,"instanceName":"15"}),makeQuery(id+"F2.opPattern","COPY",FACE,{"derivedFrom":subQ1,"instanceName":"16"}),makeQuery(id+"F2.opPattern","COPY",FACE,{"derivedFrom":subQ1,"instanceName":"17"}),makeQuery(id+"F2.opPattern","COPY",FACE,{"derivedFrom":subQ1,"instanceName":"18"}),makeQuery(id+"F2.opPattern","COPY",FACE,{"derivedFrom":subQ1,"instanceName":"19"}),makeQuery(id+"F2.opPattern","COPY",FACE,{"derivedFrom":subQ1,"instanceName":"20"}),makeQuery(id+"F2.opPattern","COPY",FACE,{"derivedFrom":subQ1,"instanceName":"21"}),makeQuery(id+"F2.opPattern","COPY",FACE,{"derivedFrom":subQ1,"instanceName":"22"}),makeQuery(id+"F2.opPattern","COPY",FACE,{"derivedFrom":subQ1,"instanceName":"23"})]})]});}
            var Q24;
            {var subQ0=sQuery(id+"F0.wireOp",EDGE,"E14.MirrorCS");var subQ1=makeQuery(id+"F1.opExtrude","CAP_FACE",FACE,{"disambiguationData":[OSD([sQuery(id+"F0.wireOp",EDGE,"E2"),sQuery(id+"F0.wireOp",EDGE,"E11"),sQuery(id+"F0.wireOp",EDGE,"E12"),sQuery(id+"F0.wireOp",EDGE,"E13.MirrorCS"),subQ0,sQuery(id+"F0.wireOp",EDGE,"E15"),sQuery(id+"F0.wireOp",EDGE,"E19")])],"isStart":false});Q24=makeQuery(id+"F3.opFillet","BLEND_EDGE",EDGE,{"blendedFrom":[makeQuery(id+"F2.opPattern","COPY",EDGE,{"derivedFrom":makeQuery(id+"F1.opExtrude","CAP_EDGE",EDGE,{"disambiguationData":[OSD([subQ0])],"isStart":false}),"instanceName":"11"}),makeQuery(id+"F2.boolean.opBoolean","MERGE",FACE,{"derivedFrom":[subQ1,makeQuery(id+"F2.opPattern","COPY",FACE,{"derivedFrom":subQ1,"instanceName":"1"}),makeQuery(id+"F2.opPattern","COPY",FACE,{"derivedFrom":subQ1,"instanceName":"2"}),makeQuery(id+"F2.opPattern","COPY",FACE,{"derivedFrom":subQ1,"instanceName":"3"}),makeQuery(id+"F2.opPattern","COPY",FACE,{"derivedFrom":subQ1,"instanceName":"4"}),makeQuery(id+"F2.opPattern","COPY",FACE,{"derivedFrom":subQ1,"instanceName":"5"}),makeQuery(id+"F2.opPattern","COPY",FACE,{"derivedFrom":subQ1,"instanceName":"6"}),makeQuery(id+"F2.opPattern","COPY",FACE,{"derivedFrom":subQ1,"instanceName":"7"}),makeQuery(id+"F2.opPattern","COPY",FACE,{"derivedFrom":subQ1,"instanceName":"8"}),makeQuery(id+"F2.opPattern","COPY",FACE,{"derivedFrom":subQ1,"instanceName":"9"}),makeQuery(id+"F2.opPattern","COPY",FACE,{"derivedFrom":subQ1,"instanceName":"10"}),makeQuery(id+"F2.opPattern","COPY",FACE,{"derivedFrom":subQ1,"instanceName":"11"}),makeQuery(id+"F2.opPattern","COPY",FACE,{"derivedFrom":subQ1,"instanceName":"12"}),makeQuery(id+"F2.opPattern","COPY",FACE,{"derivedFrom":subQ1,"instanceName":"13"}),makeQuery(id+"F2.opPattern","COPY",FACE,{"derivedFrom":subQ1,"instanceName":"14"}),makeQuery(id+"F2.opPattern","COPY",FACE,{"derivedFrom":subQ1,"instanceName":"15"}),makeQuery(id+"F2.opPattern","COPY",FACE,{"derivedFrom":subQ1,"instanceName":"16"}),makeQuery(id+"F2.opPattern","COPY",FACE,{"derivedFrom":subQ1,"instanceName":"17"}),makeQuery(id+"F2.opPattern","COPY",FACE,{"derivedFrom":subQ1,"instanceName":"18"}),makeQuery(id+"F2.opPattern","COPY",FACE,{"derivedFrom":subQ1,"instanceName":"19"}),makeQuery(id+"F2.opPattern","COPY",FACE,{"derivedFrom":subQ1,"instanceName":"20"}),makeQuery(id+"F2.opPattern","COPY",FACE,{"derivedFrom":subQ1,"instanceName":"21"}),makeQuery(id+"F2.opPattern","COPY",FACE,{"derivedFrom":subQ1,"instanceName":"22"}),makeQuery(id+"F2.opPattern","COPY",FACE,{"derivedFrom":subQ1,"instanceName":"23"})]})],"blendedInto":[makeQuery(id+"F2.boolean.opBoolean","MERGE",FACE,{"derivedFrom":[subQ1,makeQuery(id+"F2.opPattern","COPY",FACE,{"derivedFrom":subQ1,"instanceName":"1"}),makeQuery(id+"F2.opPattern","COPY",FACE,{"derivedFrom":subQ1,"instanceName":"2"}),makeQuery(id+"F2.opPattern","COPY",FACE,{"derivedFrom":subQ1,"instanceName":"3"}),makeQuery(id+"F2.opPattern","COPY",FACE,{"derivedFrom":subQ1,"instanceName":"4"}),makeQuery(id+"F2.opPattern","COPY",FACE,{"derivedFrom":subQ1,"instanceName":"5"}),makeQuery(id+"F2.opPattern","COPY",FACE,{"derivedFrom":subQ1,"instanceName":"6"}),makeQuery(id+"F2.opPattern","COPY",FACE,{"derivedFrom":subQ1,"instanceName":"7"}),makeQuery(id+"F2.opPattern","COPY",FACE,{"derivedFrom":subQ1,"instanceName":"8"}),makeQuery(id+"F2.opPattern","COPY",FACE,{"derivedFrom":subQ1,"instanceName":"9"}),makeQuery(id+"F2.opPattern","COPY",FACE,{"derivedFrom":subQ1,"instanceName":"10"}),makeQuery(id+"F2.opPattern","COPY",FACE,{"derivedFrom":subQ1,"instanceName":"11"}),makeQuery(id+"F2.opPattern","COPY",FACE,{"derivedFrom":subQ1,"instanceName":"12"}),makeQuery(id+"F2.opPattern","COPY",FACE,{"derivedFrom":subQ1,"instanceName":"13"}),makeQuery(id+"F2.opPattern","COPY",FACE,{"derivedFrom":subQ1,"instanceName":"14"}),makeQuery(id+"F2.opPattern","COPY",FACE,{"derivedFrom":subQ1,"instanceName":"15"}),makeQuery(id+"F2.opPattern","COPY",FACE,{"derivedFrom":subQ1,"instanceName":"16"}),makeQuery(id+"F2.opPattern","COPY",FACE,{"derivedFrom":subQ1,"instanceName":"17"}),makeQuery(id+"F2.opPattern","COPY",FACE,{"derivedFrom":subQ1,"instanceName":"18"}),makeQuery(id+"F2.opPattern","COPY",FACE,{"derivedFrom":subQ1,"instanceName":"19"}),makeQuery(id+"F2.opPattern","COPY",FACE,{"derivedFrom":subQ1,"instanceName":"20"}),makeQuery(id+"F2.opPattern","COPY",FACE,{"derivedFrom":subQ1,"instanceName":"21"}),makeQuery(id+"F2.opPattern","COPY",FACE,{"derivedFrom":subQ1,"instanceName":"22"}),makeQuery(id+"F2.opPattern","COPY",FACE,{"derivedFrom":subQ1,"instanceName":"23"})]})]});}
            var Q25;
            {var subQ0=sQuery(id+"F0.wireOp",EDGE,"E12");var subQ1=makeQuery(id+"F1.opExtrude","CAP_FACE",FACE,{"disambiguationData":[OSD([sQuery(id+"F0.wireOp",EDGE,"E2"),sQuery(id+"F0.wireOp",EDGE,"E11"),subQ0,sQuery(id+"F0.wireOp",EDGE,"E13.MirrorCS"),sQuery(id+"F0.wireOp",EDGE,"E14.MirrorCS"),sQuery(id+"F0.wireOp",EDGE,"E15"),sQuery(id+"F0.wireOp",EDGE,"E19")])],"isStart":false});Q25=makeQuery(id+"F3.opFillet","BLEND_EDGE",EDGE,{"blendedFrom":[makeQuery(id+"F2.opPattern","COPY",EDGE,{"derivedFrom":makeQuery(id+"F1.opExtrude","CAP_EDGE",EDGE,{"disambiguationData":[OSD([subQ0])],"isStart":false}),"instanceName":"11"}),makeQuery(id+"F2.boolean.opBoolean","MERGE",FACE,{"derivedFrom":[subQ1,makeQuery(id+"F2.opPattern","COPY",FACE,{"derivedFrom":subQ1,"instanceName":"1"}),makeQuery(id+"F2.opPattern","COPY",FACE,{"derivedFrom":subQ1,"instanceName":"2"}),makeQuery(id+"F2.opPattern","COPY",FACE,{"derivedFrom":subQ1,"instanceName":"3"}),makeQuery(id+"F2.opPattern","COPY",FACE,{"derivedFrom":subQ1,"instanceName":"4"}),makeQuery(id+"F2.opPattern","COPY",FACE,{"derivedFrom":subQ1,"instanceName":"5"}),makeQuery(id+"F2.opPattern","COPY",FACE,{"derivedFrom":subQ1,"instanceName":"6"}),makeQuery(id+"F2.opPattern","COPY",FACE,{"derivedFrom":subQ1,"instanceName":"7"}),makeQuery(id+"F2.opPattern","COPY",FACE,{"derivedFrom":subQ1,"instanceName":"8"}),makeQuery(id+"F2.opPattern","COPY",FACE,{"derivedFrom":subQ1,"instanceName":"9"}),makeQuery(id+"F2.opPattern","COPY",FACE,{"derivedFrom":subQ1,"instanceName":"10"}),makeQuery(id+"F2.opPattern","COPY",FACE,{"derivedFrom":subQ1,"instanceName":"11"}),makeQuery(id+"F2.opPattern","COPY",FACE,{"derivedFrom":subQ1,"instanceName":"12"}),makeQuery(id+"F2.opPattern","COPY",FACE,{"derivedFrom":subQ1,"instanceName":"13"}),makeQuery(id+"F2.opPattern","COPY",FACE,{"derivedFrom":subQ1,"instanceName":"14"}),makeQuery(id+"F2.opPattern","COPY",FACE,{"derivedFrom":subQ1,"instanceName":"15"}),makeQuery(id+"F2.opPattern","COPY",FACE,{"derivedFrom":subQ1,"instanceName":"16"}),makeQuery(id+"F2.opPattern","COPY",FACE,{"derivedFrom":subQ1,"instanceName":"17"}),makeQuery(id+"F2.opPattern","COPY",FACE,{"derivedFrom":subQ1,"instanceName":"18"}),makeQuery(id+"F2.opPattern","COPY",FACE,{"derivedFrom":subQ1,"instanceName":"19"}),makeQuery(id+"F2.opPattern","COPY",FACE,{"derivedFrom":subQ1,"instanceName":"20"}),makeQuery(id+"F2.opPattern","COPY",FACE,{"derivedFrom":subQ1,"instanceName":"21"}),makeQuery(id+"F2.opPattern","COPY",FACE,{"derivedFrom":subQ1,"instanceName":"22"}),makeQuery(id+"F2.opPattern","COPY",FACE,{"derivedFrom":subQ1,"instanceName":"23"})]})],"blendedInto":[makeQuery(id+"F2.boolean.opBoolean","MERGE",FACE,{"derivedFrom":[subQ1,makeQuery(id+"F2.opPattern","COPY",FACE,{"derivedFrom":subQ1,"instanceName":"1"}),makeQuery(id+"F2.opPattern","COPY",FACE,{"derivedFrom":subQ1,"instanceName":"2"}),makeQuery(id+"F2.opPattern","COPY",FACE,{"derivedFrom":subQ1,"instanceName":"3"}),makeQuery(id+"F2.opPattern","COPY",FACE,{"derivedFrom":subQ1,"instanceName":"4"}),makeQuery(id+"F2.opPattern","COPY",FACE,{"derivedFrom":subQ1,"instanceName":"5"}),makeQuery(id+"F2.opPattern","COPY",FACE,{"derivedFrom":subQ1,"instanceName":"6"}),makeQuery(id+"F2.opPattern","COPY",FACE,{"derivedFrom":subQ1,"instanceName":"7"}),makeQuery(id+"F2.opPattern","COPY",FACE,{"derivedFrom":subQ1,"instanceName":"8"}),makeQuery(id+"F2.opPattern","COPY",FACE,{"derivedFrom":subQ1,"instanceName":"9"}),makeQuery(id+"F2.opPattern","COPY",FACE,{"derivedFrom":subQ1,"instanceName":"10"}),makeQuery(id+"F2.opPattern","COPY",FACE,{"derivedFrom":subQ1,"instanceName":"11"}),makeQuery(id+"F2.opPattern","COPY",FACE,{"derivedFrom":subQ1,"instanceName":"12"}),makeQuery(id+"F2.opPattern","COPY",FACE,{"derivedFrom":subQ1,"instanceName":"13"}),makeQuery(id+"F2.opPattern","COPY",FACE,{"derivedFrom":subQ1,"instanceName":"14"}),makeQuery(id+"F2.opPattern","COPY",FACE,{"derivedFrom":subQ1,"instanceName":"15"}),makeQuery(id+"F2.opPattern","COPY",FACE,{"derivedFrom":subQ1,"instanceName":"16"}),makeQuery(id+"F2.opPattern","COPY",FACE,{"derivedFrom":subQ1,"instanceName":"17"}),makeQuery(id+"F2.opPattern","COPY",FACE,{"derivedFrom":subQ1,"instanceName":"18"}),makeQuery(id+"F2.opPattern","COPY",FACE,{"derivedFrom":subQ1,"instanceName":"19"}),makeQuery(id+"F2.opPattern","COPY",FACE,{"derivedFrom":subQ1,"instanceName":"20"}),makeQuery(id+"F2.opPattern","COPY",FACE,{"derivedFrom":subQ1,"instanceName":"21"}),makeQuery(id+"F2.opPattern","COPY",FACE,{"derivedFrom":subQ1,"instanceName":"22"}),makeQuery(id+"F2.opPattern","COPY",FACE,{"derivedFrom":subQ1,"instanceName":"23"})]})]});}
            var Q26;
            {var subQ0=sQuery(id+"F0.wireOp",EDGE,"E14.MirrorCS");var subQ1=makeQuery(id+"F1.opExtrude","CAP_FACE",FACE,{"disambiguationData":[OSD([sQuery(id+"F0.wireOp",EDGE,"E2"),sQuery(id+"F0.wireOp",EDGE,"E11"),sQuery(id+"F0.wireOp",EDGE,"E12"),sQuery(id+"F0.wireOp",EDGE,"E13.MirrorCS"),subQ0,sQuery(id+"F0.wireOp",EDGE,"E15"),sQuery(id+"F0.wireOp",EDGE,"E19")])],"isStart":false});Q26=makeQuery(id+"F3.opFillet","BLEND_EDGE",EDGE,{"blendedFrom":[makeQuery(id+"F2.opPattern","COPY",EDGE,{"derivedFrom":makeQuery(id+"F1.opExtrude","CAP_EDGE",EDGE,{"disambiguationData":[OSD([subQ0])],"isStart":false}),"instanceName":"12"}),makeQuery(id+"F2.boolean.opBoolean","MERGE",FACE,{"derivedFrom":[subQ1,makeQuery(id+"F2.opPattern","COPY",FACE,{"derivedFrom":subQ1,"instanceName":"1"}),makeQuery(id+"F2.opPattern","COPY",FACE,{"derivedFrom":subQ1,"instanceName":"2"}),makeQuery(id+"F2.opPattern","COPY",FACE,{"derivedFrom":subQ1,"instanceName":"3"}),makeQuery(id+"F2.opPattern","COPY",FACE,{"derivedFrom":subQ1,"instanceName":"4"}),makeQuery(id+"F2.opPattern","COPY",FACE,{"derivedFrom":subQ1,"instanceName":"5"}),makeQuery(id+"F2.opPattern","COPY",FACE,{"derivedFrom":subQ1,"instanceName":"6"}),makeQuery(id+"F2.opPattern","COPY",FACE,{"derivedFrom":subQ1,"instanceName":"7"}),makeQuery(id+"F2.opPattern","COPY",FACE,{"derivedFrom":subQ1,"instanceName":"8"}),makeQuery(id+"F2.opPattern","COPY",FACE,{"derivedFrom":subQ1,"instanceName":"9"}),makeQuery(id+"F2.opPattern","COPY",FACE,{"derivedFrom":subQ1,"instanceName":"10"}),makeQuery(id+"F2.opPattern","COPY",FACE,{"derivedFrom":subQ1,"instanceName":"11"}),makeQuery(id+"F2.opPattern","COPY",FACE,{"derivedFrom":subQ1,"instanceName":"12"}),makeQuery(id+"F2.opPattern","COPY",FACE,{"derivedFrom":subQ1,"instanceName":"13"}),makeQuery(id+"F2.opPattern","COPY",FACE,{"derivedFrom":subQ1,"instanceName":"14"}),makeQuery(id+"F2.opPattern","COPY",FACE,{"derivedFrom":subQ1,"instanceName":"15"}),makeQuery(id+"F2.opPattern","COPY",FACE,{"derivedFrom":subQ1,"instanceName":"16"}),makeQuery(id+"F2.opPattern","COPY",FACE,{"derivedFrom":subQ1,"instanceName":"17"}),makeQuery(id+"F2.opPattern","COPY",FACE,{"derivedFrom":subQ1,"instanceName":"18"}),makeQuery(id+"F2.opPattern","COPY",FACE,{"derivedFrom":subQ1,"instanceName":"19"}),makeQuery(id+"F2.opPattern","COPY",FACE,{"derivedFrom":subQ1,"instanceName":"20"}),makeQuery(id+"F2.opPattern","COPY",FACE,{"derivedFrom":subQ1,"instanceName":"21"}),makeQuery(id+"F2.opPattern","COPY",FACE,{"derivedFrom":subQ1,"instanceName":"22"}),makeQuery(id+"F2.opPattern","COPY",FACE,{"derivedFrom":subQ1,"instanceName":"23"})]})],"blendedInto":[makeQuery(id+"F2.boolean.opBoolean","MERGE",FACE,{"derivedFrom":[subQ1,makeQuery(id+"F2.opPattern","COPY",FACE,{"derivedFrom":subQ1,"instanceName":"1"}),makeQuery(id+"F2.opPattern","COPY",FACE,{"derivedFrom":subQ1,"instanceName":"2"}),makeQuery(id+"F2.opPattern","COPY",FACE,{"derivedFrom":subQ1,"instanceName":"3"}),makeQuery(id+"F2.opPattern","COPY",FACE,{"derivedFrom":subQ1,"instanceName":"4"}),makeQuery(id+"F2.opPattern","COPY",FACE,{"derivedFrom":subQ1,"instanceName":"5"}),makeQuery(id+"F2.opPattern","COPY",FACE,{"derivedFrom":subQ1,"instanceName":"6"}),makeQuery(id+"F2.opPattern","COPY",FACE,{"derivedFrom":subQ1,"instanceName":"7"}),makeQuery(id+"F2.opPattern","COPY",FACE,{"derivedFrom":subQ1,"instanceName":"8"}),makeQuery(id+"F2.opPattern","COPY",FACE,{"derivedFrom":subQ1,"instanceName":"9"}),makeQuery(id+"F2.opPattern","COPY",FACE,{"derivedFrom":subQ1,"instanceName":"10"}),makeQuery(id+"F2.opPattern","COPY",FACE,{"derivedFrom":subQ1,"instanceName":"11"}),makeQuery(id+"F2.opPattern","COPY",FACE,{"derivedFrom":subQ1,"instanceName":"12"}),makeQuery(id+"F2.opPattern","COPY",FACE,{"derivedFrom":subQ1,"instanceName":"13"}),makeQuery(id+"F2.opPattern","COPY",FACE,{"derivedFrom":subQ1,"instanceName":"14"}),makeQuery(id+"F2.opPattern","COPY",FACE,{"derivedFrom":subQ1,"instanceName":"15"}),makeQuery(id+"F2.opPattern","COPY",FACE,{"derivedFrom":subQ1,"instanceName":"16"}),makeQuery(id+"F2.opPattern","COPY",FACE,{"derivedFrom":subQ1,"instanceName":"17"}),makeQuery(id+"F2.opPattern","COPY",FACE,{"derivedFrom":subQ1,"instanceName":"18"}),makeQuery(id+"F2.opPattern","COPY",FACE,{"derivedFrom":subQ1,"instanceName":"19"}),makeQuery(id+"F2.opPattern","COPY",FACE,{"derivedFrom":subQ1,"instanceName":"20"}),makeQuery(id+"F2.opPattern","COPY",FACE,{"derivedFrom":subQ1,"instanceName":"21"}),makeQuery(id+"F2.opPattern","COPY",FACE,{"derivedFrom":subQ1,"instanceName":"22"}),makeQuery(id+"F2.opPattern","COPY",FACE,{"derivedFrom":subQ1,"instanceName":"23"})]})]});}
            var Q27;
            {var subQ0=sQuery(id+"F0.wireOp",EDGE,"E12");var subQ1=makeQuery(id+"F1.opExtrude","CAP_FACE",FACE,{"disambiguationData":[OSD([sQuery(id+"F0.wireOp",EDGE,"E2"),sQuery(id+"F0.wireOp",EDGE,"E11"),subQ0,sQuery(id+"F0.wireOp",EDGE,"E13.MirrorCS"),sQuery(id+"F0.wireOp",EDGE,"E14.MirrorCS"),sQuery(id+"F0.wireOp",EDGE,"E15"),sQuery(id+"F0.wireOp",EDGE,"E19")])],"isStart":false});Q27=makeQuery(id+"F3.opFillet","BLEND_EDGE",EDGE,{"blendedFrom":[makeQuery(id+"F2.opPattern","COPY",EDGE,{"derivedFrom":makeQuery(id+"F1.opExtrude","CAP_EDGE",EDGE,{"disambiguationData":[OSD([subQ0])],"isStart":false}),"instanceName":"12"}),makeQuery(id+"F2.boolean.opBoolean","MERGE",FACE,{"derivedFrom":[subQ1,makeQuery(id+"F2.opPattern","COPY",FACE,{"derivedFrom":subQ1,"instanceName":"1"}),makeQuery(id+"F2.opPattern","COPY",FACE,{"derivedFrom":subQ1,"instanceName":"2"}),makeQuery(id+"F2.opPattern","COPY",FACE,{"derivedFrom":subQ1,"instanceName":"3"}),makeQuery(id+"F2.opPattern","COPY",FACE,{"derivedFrom":subQ1,"instanceName":"4"}),makeQuery(id+"F2.opPattern","COPY",FACE,{"derivedFrom":subQ1,"instanceName":"5"}),makeQuery(id+"F2.opPattern","COPY",FACE,{"derivedFrom":subQ1,"instanceName":"6"}),makeQuery(id+"F2.opPattern","COPY",FACE,{"derivedFrom":subQ1,"instanceName":"7"}),makeQuery(id+"F2.opPattern","COPY",FACE,{"derivedFrom":subQ1,"instanceName":"8"}),makeQuery(id+"F2.opPattern","COPY",FACE,{"derivedFrom":subQ1,"instanceName":"9"}),makeQuery(id+"F2.opPattern","COPY",FACE,{"derivedFrom":subQ1,"instanceName":"10"}),makeQuery(id+"F2.opPattern","COPY",FACE,{"derivedFrom":subQ1,"instanceName":"11"}),makeQuery(id+"F2.opPattern","COPY",FACE,{"derivedFrom":subQ1,"instanceName":"12"}),makeQuery(id+"F2.opPattern","COPY",FACE,{"derivedFrom":subQ1,"instanceName":"13"}),makeQuery(id+"F2.opPattern","COPY",FACE,{"derivedFrom":subQ1,"instanceName":"14"}),makeQuery(id+"F2.opPattern","COPY",FACE,{"derivedFrom":subQ1,"instanceName":"15"}),makeQuery(id+"F2.opPattern","COPY",FACE,{"derivedFrom":subQ1,"instanceName":"16"}),makeQuery(id+"F2.opPattern","COPY",FACE,{"derivedFrom":subQ1,"instanceName":"17"}),makeQuery(id+"F2.opPattern","COPY",FACE,{"derivedFrom":subQ1,"instanceName":"18"}),makeQuery(id+"F2.opPattern","COPY",FACE,{"derivedFrom":subQ1,"instanceName":"19"}),makeQuery(id+"F2.opPattern","COPY",FACE,{"derivedFrom":subQ1,"instanceName":"20"}),makeQuery(id+"F2.opPattern","COPY",FACE,{"derivedFrom":subQ1,"instanceName":"21"}),makeQuery(id+"F2.opPattern","COPY",FACE,{"derivedFrom":subQ1,"instanceName":"22"}),makeQuery(id+"F2.opPattern","COPY",FACE,{"derivedFrom":subQ1,"instanceName":"23"})]})],"blendedInto":[makeQuery(id+"F2.boolean.opBoolean","MERGE",FACE,{"derivedFrom":[subQ1,makeQuery(id+"F2.opPattern","COPY",FACE,{"derivedFrom":subQ1,"instanceName":"1"}),makeQuery(id+"F2.opPattern","COPY",FACE,{"derivedFrom":subQ1,"instanceName":"2"}),makeQuery(id+"F2.opPattern","COPY",FACE,{"derivedFrom":subQ1,"instanceName":"3"}),makeQuery(id+"F2.opPattern","COPY",FACE,{"derivedFrom":subQ1,"instanceName":"4"}),makeQuery(id+"F2.opPattern","COPY",FACE,{"derivedFrom":subQ1,"instanceName":"5"}),makeQuery(id+"F2.opPattern","COPY",FACE,{"derivedFrom":subQ1,"instanceName":"6"}),makeQuery(id+"F2.opPattern","COPY",FACE,{"derivedFrom":subQ1,"instanceName":"7"}),makeQuery(id+"F2.opPattern","COPY",FACE,{"derivedFrom":subQ1,"instanceName":"8"}),makeQuery(id+"F2.opPattern","COPY",FACE,{"derivedFrom":subQ1,"instanceName":"9"}),makeQuery(id+"F2.opPattern","COPY",FACE,{"derivedFrom":subQ1,"instanceName":"10"}),makeQuery(id+"F2.opPattern","COPY",FACE,{"derivedFrom":subQ1,"instanceName":"11"}),makeQuery(id+"F2.opPattern","COPY",FACE,{"derivedFrom":subQ1,"instanceName":"12"}),makeQuery(id+"F2.opPattern","COPY",FACE,{"derivedFrom":subQ1,"instanceName":"13"}),makeQuery(id+"F2.opPattern","COPY",FACE,{"derivedFrom":subQ1,"instanceName":"14"}),makeQuery(id+"F2.opPattern","COPY",FACE,{"derivedFrom":subQ1,"instanceName":"15"}),makeQuery(id+"F2.opPattern","COPY",FACE,{"derivedFrom":subQ1,"instanceName":"16"}),makeQuery(id+"F2.opPattern","COPY",FACE,{"derivedFrom":subQ1,"instanceName":"17"}),makeQuery(id+"F2.opPattern","COPY",FACE,{"derivedFrom":subQ1,"instanceName":"18"}),makeQuery(id+"F2.opPattern","COPY",FACE,{"derivedFrom":subQ1,"instanceName":"19"}),makeQuery(id+"F2.opPattern","COPY",FACE,{"derivedFrom":subQ1,"instanceName":"20"}),makeQuery(id+"F2.opPattern","COPY",FACE,{"derivedFrom":subQ1,"instanceName":"21"}),makeQuery(id+"F2.opPattern","COPY",FACE,{"derivedFrom":subQ1,"instanceName":"22"}),makeQuery(id+"F2.opPattern","COPY",FACE,{"derivedFrom":subQ1,"instanceName":"23"})]})]});}
            var Q28;
            {var subQ0=sQuery(id+"F0.wireOp",EDGE,"E14.MirrorCS");var subQ1=makeQuery(id+"F1.opExtrude","CAP_FACE",FACE,{"disambiguationData":[OSD([sQuery(id+"F0.wireOp",EDGE,"E2"),sQuery(id+"F0.wireOp",EDGE,"E11"),sQuery(id+"F0.wireOp",EDGE,"E12"),sQuery(id+"F0.wireOp",EDGE,"E13.MirrorCS"),subQ0,sQuery(id+"F0.wireOp",EDGE,"E15"),sQuery(id+"F0.wireOp",EDGE,"E19")])],"isStart":false});Q28=makeQuery(id+"F3.opFillet","BLEND_EDGE",EDGE,{"blendedFrom":[makeQuery(id+"F2.opPattern","COPY",EDGE,{"derivedFrom":makeQuery(id+"F1.opExtrude","CAP_EDGE",EDGE,{"disambiguationData":[OSD([subQ0])],"isStart":false}),"instanceName":"13"}),makeQuery(id+"F2.boolean.opBoolean","MERGE",FACE,{"derivedFrom":[subQ1,makeQuery(id+"F2.opPattern","COPY",FACE,{"derivedFrom":subQ1,"instanceName":"1"}),makeQuery(id+"F2.opPattern","COPY",FACE,{"derivedFrom":subQ1,"instanceName":"2"}),makeQuery(id+"F2.opPattern","COPY",FACE,{"derivedFrom":subQ1,"instanceName":"3"}),makeQuery(id+"F2.opPattern","COPY",FACE,{"derivedFrom":subQ1,"instanceName":"4"}),makeQuery(id+"F2.opPattern","COPY",FACE,{"derivedFrom":subQ1,"instanceName":"5"}),makeQuery(id+"F2.opPattern","COPY",FACE,{"derivedFrom":subQ1,"instanceName":"6"}),makeQuery(id+"F2.opPattern","COPY",FACE,{"derivedFrom":subQ1,"instanceName":"7"}),makeQuery(id+"F2.opPattern","COPY",FACE,{"derivedFrom":subQ1,"instanceName":"8"}),makeQuery(id+"F2.opPattern","COPY",FACE,{"derivedFrom":subQ1,"instanceName":"9"}),makeQuery(id+"F2.opPattern","COPY",FACE,{"derivedFrom":subQ1,"instanceName":"10"}),makeQuery(id+"F2.opPattern","COPY",FACE,{"derivedFrom":subQ1,"instanceName":"11"}),makeQuery(id+"F2.opPattern","COPY",FACE,{"derivedFrom":subQ1,"instanceName":"12"}),makeQuery(id+"F2.opPattern","COPY",FACE,{"derivedFrom":subQ1,"instanceName":"13"}),makeQuery(id+"F2.opPattern","COPY",FACE,{"derivedFrom":subQ1,"instanceName":"14"}),makeQuery(id+"F2.opPattern","COPY",FACE,{"derivedFrom":subQ1,"instanceName":"15"}),makeQuery(id+"F2.opPattern","COPY",FACE,{"derivedFrom":subQ1,"instanceName":"16"}),makeQuery(id+"F2.opPattern","COPY",FACE,{"derivedFrom":subQ1,"instanceName":"17"}),makeQuery(id+"F2.opPattern","COPY",FACE,{"derivedFrom":subQ1,"instanceName":"18"}),makeQuery(id+"F2.opPattern","COPY",FACE,{"derivedFrom":subQ1,"instanceName":"19"}),makeQuery(id+"F2.opPattern","COPY",FACE,{"derivedFrom":subQ1,"instanceName":"20"}),makeQuery(id+"F2.opPattern","COPY",FACE,{"derivedFrom":subQ1,"instanceName":"21"}),makeQuery(id+"F2.opPattern","COPY",FACE,{"derivedFrom":subQ1,"instanceName":"22"}),makeQuery(id+"F2.opPattern","COPY",FACE,{"derivedFrom":subQ1,"instanceName":"23"})]})],"blendedInto":[makeQuery(id+"F2.boolean.opBoolean","MERGE",FACE,{"derivedFrom":[subQ1,makeQuery(id+"F2.opPattern","COPY",FACE,{"derivedFrom":subQ1,"instanceName":"1"}),makeQuery(id+"F2.opPattern","COPY",FACE,{"derivedFrom":subQ1,"instanceName":"2"}),makeQuery(id+"F2.opPattern","COPY",FACE,{"derivedFrom":subQ1,"instanceName":"3"}),makeQuery(id+"F2.opPattern","COPY",FACE,{"derivedFrom":subQ1,"instanceName":"4"}),makeQuery(id+"F2.opPattern","COPY",FACE,{"derivedFrom":subQ1,"instanceName":"5"}),makeQuery(id+"F2.opPattern","COPY",FACE,{"derivedFrom":subQ1,"instanceName":"6"}),makeQuery(id+"F2.opPattern","COPY",FACE,{"derivedFrom":subQ1,"instanceName":"7"}),makeQuery(id+"F2.opPattern","COPY",FACE,{"derivedFrom":subQ1,"instanceName":"8"}),makeQuery(id+"F2.opPattern","COPY",FACE,{"derivedFrom":subQ1,"instanceName":"9"}),makeQuery(id+"F2.opPattern","COPY",FACE,{"derivedFrom":subQ1,"instanceName":"10"}),makeQuery(id+"F2.opPattern","COPY",FACE,{"derivedFrom":subQ1,"instanceName":"11"}),makeQuery(id+"F2.opPattern","COPY",FACE,{"derivedFrom":subQ1,"instanceName":"12"}),makeQuery(id+"F2.opPattern","COPY",FACE,{"derivedFrom":subQ1,"instanceName":"13"}),makeQuery(id+"F2.opPattern","COPY",FACE,{"derivedFrom":subQ1,"instanceName":"14"}),makeQuery(id+"F2.opPattern","COPY",FACE,{"derivedFrom":subQ1,"instanceName":"15"}),makeQuery(id+"F2.opPattern","COPY",FACE,{"derivedFrom":subQ1,"instanceName":"16"}),makeQuery(id+"F2.opPattern","COPY",FACE,{"derivedFrom":subQ1,"instanceName":"17"}),makeQuery(id+"F2.opPattern","COPY",FACE,{"derivedFrom":subQ1,"instanceName":"18"}),makeQuery(id+"F2.opPattern","COPY",FACE,{"derivedFrom":subQ1,"instanceName":"19"}),makeQuery(id+"F2.opPattern","COPY",FACE,{"derivedFrom":subQ1,"instanceName":"20"}),makeQuery(id+"F2.opPattern","COPY",FACE,{"derivedFrom":subQ1,"instanceName":"21"}),makeQuery(id+"F2.opPattern","COPY",FACE,{"derivedFrom":subQ1,"instanceName":"22"}),makeQuery(id+"F2.opPattern","COPY",FACE,{"derivedFrom":subQ1,"instanceName":"23"})]})]});}
            var Q29;
            {var subQ0=sQuery(id+"F0.wireOp",EDGE,"E12");var subQ1=makeQuery(id+"F1.opExtrude","CAP_FACE",FACE,{"disambiguationData":[OSD([sQuery(id+"F0.wireOp",EDGE,"E2"),sQuery(id+"F0.wireOp",EDGE,"E11"),subQ0,sQuery(id+"F0.wireOp",EDGE,"E13.MirrorCS"),sQuery(id+"F0.wireOp",EDGE,"E14.MirrorCS"),sQuery(id+"F0.wireOp",EDGE,"E15"),sQuery(id+"F0.wireOp",EDGE,"E19")])],"isStart":false});Q29=makeQuery(id+"F3.opFillet","BLEND_EDGE",EDGE,{"blendedFrom":[makeQuery(id+"F2.opPattern","COPY",EDGE,{"derivedFrom":makeQuery(id+"F1.opExtrude","CAP_EDGE",EDGE,{"disambiguationData":[OSD([subQ0])],"isStart":false}),"instanceName":"13"}),makeQuery(id+"F2.boolean.opBoolean","MERGE",FACE,{"derivedFrom":[subQ1,makeQuery(id+"F2.opPattern","COPY",FACE,{"derivedFrom":subQ1,"instanceName":"1"}),makeQuery(id+"F2.opPattern","COPY",FACE,{"derivedFrom":subQ1,"instanceName":"2"}),makeQuery(id+"F2.opPattern","COPY",FACE,{"derivedFrom":subQ1,"instanceName":"3"}),makeQuery(id+"F2.opPattern","COPY",FACE,{"derivedFrom":subQ1,"instanceName":"4"}),makeQuery(id+"F2.opPattern","COPY",FACE,{"derivedFrom":subQ1,"instanceName":"5"}),makeQuery(id+"F2.opPattern","COPY",FACE,{"derivedFrom":subQ1,"instanceName":"6"}),makeQuery(id+"F2.opPattern","COPY",FACE,{"derivedFrom":subQ1,"instanceName":"7"}),makeQuery(id+"F2.opPattern","COPY",FACE,{"derivedFrom":subQ1,"instanceName":"8"}),makeQuery(id+"F2.opPattern","COPY",FACE,{"derivedFrom":subQ1,"instanceName":"9"}),makeQuery(id+"F2.opPattern","COPY",FACE,{"derivedFrom":subQ1,"instanceName":"10"}),makeQuery(id+"F2.opPattern","COPY",FACE,{"derivedFrom":subQ1,"instanceName":"11"}),makeQuery(id+"F2.opPattern","COPY",FACE,{"derivedFrom":subQ1,"instanceName":"12"}),makeQuery(id+"F2.opPattern","COPY",FACE,{"derivedFrom":subQ1,"instanceName":"13"}),makeQuery(id+"F2.opPattern","COPY",FACE,{"derivedFrom":subQ1,"instanceName":"14"}),makeQuery(id+"F2.opPattern","COPY",FACE,{"derivedFrom":subQ1,"instanceName":"15"}),makeQuery(id+"F2.opPattern","COPY",FACE,{"derivedFrom":subQ1,"instanceName":"16"}),makeQuery(id+"F2.opPattern","COPY",FACE,{"derivedFrom":subQ1,"instanceName":"17"}),makeQuery(id+"F2.opPattern","COPY",FACE,{"derivedFrom":subQ1,"instanceName":"18"}),makeQuery(id+"F2.opPattern","COPY",FACE,{"derivedFrom":subQ1,"instanceName":"19"}),makeQuery(id+"F2.opPattern","COPY",FACE,{"derivedFrom":subQ1,"instanceName":"20"}),makeQuery(id+"F2.opPattern","COPY",FACE,{"derivedFrom":subQ1,"instanceName":"21"}),makeQuery(id+"F2.opPattern","COPY",FACE,{"derivedFrom":subQ1,"instanceName":"22"}),makeQuery(id+"F2.opPattern","COPY",FACE,{"derivedFrom":subQ1,"instanceName":"23"})]})],"blendedInto":[makeQuery(id+"F2.boolean.opBoolean","MERGE",FACE,{"derivedFrom":[subQ1,makeQuery(id+"F2.opPattern","COPY",FACE,{"derivedFrom":subQ1,"instanceName":"1"}),makeQuery(id+"F2.opPattern","COPY",FACE,{"derivedFrom":subQ1,"instanceName":"2"}),makeQuery(id+"F2.opPattern","COPY",FACE,{"derivedFrom":subQ1,"instanceName":"3"}),makeQuery(id+"F2.opPattern","COPY",FACE,{"derivedFrom":subQ1,"instanceName":"4"}),makeQuery(id+"F2.opPattern","COPY",FACE,{"derivedFrom":subQ1,"instanceName":"5"}),makeQuery(id+"F2.opPattern","COPY",FACE,{"derivedFrom":subQ1,"instanceName":"6"}),makeQuery(id+"F2.opPattern","COPY",FACE,{"derivedFrom":subQ1,"instanceName":"7"}),makeQuery(id+"F2.opPattern","COPY",FACE,{"derivedFrom":subQ1,"instanceName":"8"}),makeQuery(id+"F2.opPattern","COPY",FACE,{"derivedFrom":subQ1,"instanceName":"9"}),makeQuery(id+"F2.opPattern","COPY",FACE,{"derivedFrom":subQ1,"instanceName":"10"}),makeQuery(id+"F2.opPattern","COPY",FACE,{"derivedFrom":subQ1,"instanceName":"11"}),makeQuery(id+"F2.opPattern","COPY",FACE,{"derivedFrom":subQ1,"instanceName":"12"}),makeQuery(id+"F2.opPattern","COPY",FACE,{"derivedFrom":subQ1,"instanceName":"13"}),makeQuery(id+"F2.opPattern","COPY",FACE,{"derivedFrom":subQ1,"instanceName":"14"}),makeQuery(id+"F2.opPattern","COPY",FACE,{"derivedFrom":subQ1,"instanceName":"15"}),makeQuery(id+"F2.opPattern","COPY",FACE,{"derivedFrom":subQ1,"instanceName":"16"}),makeQuery(id+"F2.opPattern","COPY",FACE,{"derivedFrom":subQ1,"instanceName":"17"}),makeQuery(id+"F2.opPattern","COPY",FACE,{"derivedFrom":subQ1,"instanceName":"18"}),makeQuery(id+"F2.opPattern","COPY",FACE,{"derivedFrom":subQ1,"instanceName":"19"}),makeQuery(id+"F2.opPattern","COPY",FACE,{"derivedFrom":subQ1,"instanceName":"20"}),makeQuery(id+"F2.opPattern","COPY",FACE,{"derivedFrom":subQ1,"instanceName":"21"}),makeQuery(id+"F2.opPattern","COPY",FACE,{"derivedFrom":subQ1,"instanceName":"22"}),makeQuery(id+"F2.opPattern","COPY",FACE,{"derivedFrom":subQ1,"instanceName":"23"})]})]});}
            var Q30;
            {var subQ0=sQuery(id+"F0.wireOp",EDGE,"E14.MirrorCS");var subQ1=makeQuery(id+"F1.opExtrude","CAP_FACE",FACE,{"disambiguationData":[OSD([sQuery(id+"F0.wireOp",EDGE,"E2"),sQuery(id+"F0.wireOp",EDGE,"E11"),sQuery(id+"F0.wireOp",EDGE,"E12"),sQuery(id+"F0.wireOp",EDGE,"E13.MirrorCS"),subQ0,sQuery(id+"F0.wireOp",EDGE,"E15"),sQuery(id+"F0.wireOp",EDGE,"E19")])],"isStart":false});Q30=makeQuery(id+"F3.opFillet","BLEND_EDGE",EDGE,{"blendedFrom":[makeQuery(id+"F2.opPattern","COPY",EDGE,{"derivedFrom":makeQuery(id+"F1.opExtrude","CAP_EDGE",EDGE,{"disambiguationData":[OSD([subQ0])],"isStart":false}),"instanceName":"14"}),makeQuery(id+"F2.boolean.opBoolean","MERGE",FACE,{"derivedFrom":[subQ1,makeQuery(id+"F2.opPattern","COPY",FACE,{"derivedFrom":subQ1,"instanceName":"1"}),makeQuery(id+"F2.opPattern","COPY",FACE,{"derivedFrom":subQ1,"instanceName":"2"}),makeQuery(id+"F2.opPattern","COPY",FACE,{"derivedFrom":subQ1,"instanceName":"3"}),makeQuery(id+"F2.opPattern","COPY",FACE,{"derivedFrom":subQ1,"instanceName":"4"}),makeQuery(id+"F2.opPattern","COPY",FACE,{"derivedFrom":subQ1,"instanceName":"5"}),makeQuery(id+"F2.opPattern","COPY",FACE,{"derivedFrom":subQ1,"instanceName":"6"}),makeQuery(id+"F2.opPattern","COPY",FACE,{"derivedFrom":subQ1,"instanceName":"7"}),makeQuery(id+"F2.opPattern","COPY",FACE,{"derivedFrom":subQ1,"instanceName":"8"}),makeQuery(id+"F2.opPattern","COPY",FACE,{"derivedFrom":subQ1,"instanceName":"9"}),makeQuery(id+"F2.opPattern","COPY",FACE,{"derivedFrom":subQ1,"instanceName":"10"}),makeQuery(id+"F2.opPattern","COPY",FACE,{"derivedFrom":subQ1,"instanceName":"11"}),makeQuery(id+"F2.opPattern","COPY",FACE,{"derivedFrom":subQ1,"instanceName":"12"}),makeQuery(id+"F2.opPattern","COPY",FACE,{"derivedFrom":subQ1,"instanceName":"13"}),makeQuery(id+"F2.opPattern","COPY",FACE,{"derivedFrom":subQ1,"instanceName":"14"}),makeQuery(id+"F2.opPattern","COPY",FACE,{"derivedFrom":subQ1,"instanceName":"15"}),makeQuery(id+"F2.opPattern","COPY",FACE,{"derivedFrom":subQ1,"instanceName":"16"}),makeQuery(id+"F2.opPattern","COPY",FACE,{"derivedFrom":subQ1,"instanceName":"17"}),makeQuery(id+"F2.opPattern","COPY",FACE,{"derivedFrom":subQ1,"instanceName":"18"}),makeQuery(id+"F2.opPattern","COPY",FACE,{"derivedFrom":subQ1,"instanceName":"19"}),makeQuery(id+"F2.opPattern","COPY",FACE,{"derivedFrom":subQ1,"instanceName":"20"}),makeQuery(id+"F2.opPattern","COPY",FACE,{"derivedFrom":subQ1,"instanceName":"21"}),makeQuery(id+"F2.opPattern","COPY",FACE,{"derivedFrom":subQ1,"instanceName":"22"}),makeQuery(id+"F2.opPattern","COPY",FACE,{"derivedFrom":subQ1,"instanceName":"23"})]})],"blendedInto":[makeQuery(id+"F2.boolean.opBoolean","MERGE",FACE,{"derivedFrom":[subQ1,makeQuery(id+"F2.opPattern","COPY",FACE,{"derivedFrom":subQ1,"instanceName":"1"}),makeQuery(id+"F2.opPattern","COPY",FACE,{"derivedFrom":subQ1,"instanceName":"2"}),makeQuery(id+"F2.opPattern","COPY",FACE,{"derivedFrom":subQ1,"instanceName":"3"}),makeQuery(id+"F2.opPattern","COPY",FACE,{"derivedFrom":subQ1,"instanceName":"4"}),makeQuery(id+"F2.opPattern","COPY",FACE,{"derivedFrom":subQ1,"instanceName":"5"}),makeQuery(id+"F2.opPattern","COPY",FACE,{"derivedFrom":subQ1,"instanceName":"6"}),makeQuery(id+"F2.opPattern","COPY",FACE,{"derivedFrom":subQ1,"instanceName":"7"}),makeQuery(id+"F2.opPattern","COPY",FACE,{"derivedFrom":subQ1,"instanceName":"8"}),makeQuery(id+"F2.opPattern","COPY",FACE,{"derivedFrom":subQ1,"instanceName":"9"}),makeQuery(id+"F2.opPattern","COPY",FACE,{"derivedFrom":subQ1,"instanceName":"10"}),makeQuery(id+"F2.opPattern","COPY",FACE,{"derivedFrom":subQ1,"instanceName":"11"}),makeQuery(id+"F2.opPattern","COPY",FACE,{"derivedFrom":subQ1,"instanceName":"12"}),makeQuery(id+"F2.opPattern","COPY",FACE,{"derivedFrom":subQ1,"instanceName":"13"}),makeQuery(id+"F2.opPattern","COPY",FACE,{"derivedFrom":subQ1,"instanceName":"14"}),makeQuery(id+"F2.opPattern","COPY",FACE,{"derivedFrom":subQ1,"instanceName":"15"}),makeQuery(id+"F2.opPattern","COPY",FACE,{"derivedFrom":subQ1,"instanceName":"16"}),makeQuery(id+"F2.opPattern","COPY",FACE,{"derivedFrom":subQ1,"instanceName":"17"}),makeQuery(id+"F2.opPattern","COPY",FACE,{"derivedFrom":subQ1,"instanceName":"18"}),makeQuery(id+"F2.opPattern","COPY",FACE,{"derivedFrom":subQ1,"instanceName":"19"}),makeQuery(id+"F2.opPattern","COPY",FACE,{"derivedFrom":subQ1,"instanceName":"20"}),makeQuery(id+"F2.opPattern","COPY",FACE,{"derivedFrom":subQ1,"instanceName":"21"}),makeQuery(id+"F2.opPattern","COPY",FACE,{"derivedFrom":subQ1,"instanceName":"22"}),makeQuery(id+"F2.opPattern","COPY",FACE,{"derivedFrom":subQ1,"instanceName":"23"})]})]});}
            var Q31;
            {var subQ0=sQuery(id+"F0.wireOp",EDGE,"E12");var subQ1=makeQuery(id+"F1.opExtrude","CAP_FACE",FACE,{"disambiguationData":[OSD([sQuery(id+"F0.wireOp",EDGE,"E2"),sQuery(id+"F0.wireOp",EDGE,"E11"),subQ0,sQuery(id+"F0.wireOp",EDGE,"E13.MirrorCS"),sQuery(id+"F0.wireOp",EDGE,"E14.MirrorCS"),sQuery(id+"F0.wireOp",EDGE,"E15"),sQuery(id+"F0.wireOp",EDGE,"E19")])],"isStart":false});Q31=makeQuery(id+"F3.opFillet","BLEND_EDGE",EDGE,{"blendedFrom":[makeQuery(id+"F2.opPattern","COPY",EDGE,{"derivedFrom":makeQuery(id+"F1.opExtrude","CAP_EDGE",EDGE,{"disambiguationData":[OSD([subQ0])],"isStart":false}),"instanceName":"14"}),makeQuery(id+"F2.boolean.opBoolean","MERGE",FACE,{"derivedFrom":[subQ1,makeQuery(id+"F2.opPattern","COPY",FACE,{"derivedFrom":subQ1,"instanceName":"1"}),makeQuery(id+"F2.opPattern","COPY",FACE,{"derivedFrom":subQ1,"instanceName":"2"}),makeQuery(id+"F2.opPattern","COPY",FACE,{"derivedFrom":subQ1,"instanceName":"3"}),makeQuery(id+"F2.opPattern","COPY",FACE,{"derivedFrom":subQ1,"instanceName":"4"}),makeQuery(id+"F2.opPattern","COPY",FACE,{"derivedFrom":subQ1,"instanceName":"5"}),makeQuery(id+"F2.opPattern","COPY",FACE,{"derivedFrom":subQ1,"instanceName":"6"}),makeQuery(id+"F2.opPattern","COPY",FACE,{"derivedFrom":subQ1,"instanceName":"7"}),makeQuery(id+"F2.opPattern","COPY",FACE,{"derivedFrom":subQ1,"instanceName":"8"}),makeQuery(id+"F2.opPattern","COPY",FACE,{"derivedFrom":subQ1,"instanceName":"9"}),makeQuery(id+"F2.opPattern","COPY",FACE,{"derivedFrom":subQ1,"instanceName":"10"}),makeQuery(id+"F2.opPattern","COPY",FACE,{"derivedFrom":subQ1,"instanceName":"11"}),makeQuery(id+"F2.opPattern","COPY",FACE,{"derivedFrom":subQ1,"instanceName":"12"}),makeQuery(id+"F2.opPattern","COPY",FACE,{"derivedFrom":subQ1,"instanceName":"13"}),makeQuery(id+"F2.opPattern","COPY",FACE,{"derivedFrom":subQ1,"instanceName":"14"}),makeQuery(id+"F2.opPattern","COPY",FACE,{"derivedFrom":subQ1,"instanceName":"15"}),makeQuery(id+"F2.opPattern","COPY",FACE,{"derivedFrom":subQ1,"instanceName":"16"}),makeQuery(id+"F2.opPattern","COPY",FACE,{"derivedFrom":subQ1,"instanceName":"17"}),makeQuery(id+"F2.opPattern","COPY",FACE,{"derivedFrom":subQ1,"instanceName":"18"}),makeQuery(id+"F2.opPattern","COPY",FACE,{"derivedFrom":subQ1,"instanceName":"19"}),makeQuery(id+"F2.opPattern","COPY",FACE,{"derivedFrom":subQ1,"instanceName":"20"}),makeQuery(id+"F2.opPattern","COPY",FACE,{"derivedFrom":subQ1,"instanceName":"21"}),makeQuery(id+"F2.opPattern","COPY",FACE,{"derivedFrom":subQ1,"instanceName":"22"}),makeQuery(id+"F2.opPattern","COPY",FACE,{"derivedFrom":subQ1,"instanceName":"23"})]})],"blendedInto":[makeQuery(id+"F2.boolean.opBoolean","MERGE",FACE,{"derivedFrom":[subQ1,makeQuery(id+"F2.opPattern","COPY",FACE,{"derivedFrom":subQ1,"instanceName":"1"}),makeQuery(id+"F2.opPattern","COPY",FACE,{"derivedFrom":subQ1,"instanceName":"2"}),makeQuery(id+"F2.opPattern","COPY",FACE,{"derivedFrom":subQ1,"instanceName":"3"}),makeQuery(id+"F2.opPattern","COPY",FACE,{"derivedFrom":subQ1,"instanceName":"4"}),makeQuery(id+"F2.opPattern","COPY",FACE,{"derivedFrom":subQ1,"instanceName":"5"}),makeQuery(id+"F2.opPattern","COPY",FACE,{"derivedFrom":subQ1,"instanceName":"6"}),makeQuery(id+"F2.opPattern","COPY",FACE,{"derivedFrom":subQ1,"instanceName":"7"}),makeQuery(id+"F2.opPattern","COPY",FACE,{"derivedFrom":subQ1,"instanceName":"8"}),makeQuery(id+"F2.opPattern","COPY",FACE,{"derivedFrom":subQ1,"instanceName":"9"}),makeQuery(id+"F2.opPattern","COPY",FACE,{"derivedFrom":subQ1,"instanceName":"10"}),makeQuery(id+"F2.opPattern","COPY",FACE,{"derivedFrom":subQ1,"instanceName":"11"}),makeQuery(id+"F2.opPattern","COPY",FACE,{"derivedFrom":subQ1,"instanceName":"12"}),makeQuery(id+"F2.opPattern","COPY",FACE,{"derivedFrom":subQ1,"instanceName":"13"}),makeQuery(id+"F2.opPattern","COPY",FACE,{"derivedFrom":subQ1,"instanceName":"14"}),makeQuery(id+"F2.opPattern","COPY",FACE,{"derivedFrom":subQ1,"instanceName":"15"}),makeQuery(id+"F2.opPattern","COPY",FACE,{"derivedFrom":subQ1,"instanceName":"16"}),makeQuery(id+"F2.opPattern","COPY",FACE,{"derivedFrom":subQ1,"instanceName":"17"}),makeQuery(id+"F2.opPattern","COPY",FACE,{"derivedFrom":subQ1,"instanceName":"18"}),makeQuery(id+"F2.opPattern","COPY",FACE,{"derivedFrom":subQ1,"instanceName":"19"}),makeQuery(id+"F2.opPattern","COPY",FACE,{"derivedFrom":subQ1,"instanceName":"20"}),makeQuery(id+"F2.opPattern","COPY",FACE,{"derivedFrom":subQ1,"instanceName":"21"}),makeQuery(id+"F2.opPattern","COPY",FACE,{"derivedFrom":subQ1,"instanceName":"22"}),makeQuery(id+"F2.opPattern","COPY",FACE,{"derivedFrom":subQ1,"instanceName":"23"})]})]});}
            var Q32;
            {var subQ0=sQuery(id+"F0.wireOp",EDGE,"E14.MirrorCS");var subQ1=makeQuery(id+"F1.opExtrude","CAP_FACE",FACE,{"disambiguationData":[OSD([sQuery(id+"F0.wireOp",EDGE,"E2"),sQuery(id+"F0.wireOp",EDGE,"E11"),sQuery(id+"F0.wireOp",EDGE,"E12"),sQuery(id+"F0.wireOp",EDGE,"E13.MirrorCS"),subQ0,sQuery(id+"F0.wireOp",EDGE,"E15"),sQuery(id+"F0.wireOp",EDGE,"E19")])],"isStart":false});Q32=makeQuery(id+"F3.opFillet","BLEND_EDGE",EDGE,{"blendedFrom":[makeQuery(id+"F2.opPattern","COPY",EDGE,{"derivedFrom":makeQuery(id+"F1.opExtrude","CAP_EDGE",EDGE,{"disambiguationData":[OSD([subQ0])],"isStart":false}),"instanceName":"15"}),makeQuery(id+"F2.boolean.opBoolean","MERGE",FACE,{"derivedFrom":[subQ1,makeQuery(id+"F2.opPattern","COPY",FACE,{"derivedFrom":subQ1,"instanceName":"1"}),makeQuery(id+"F2.opPattern","COPY",FACE,{"derivedFrom":subQ1,"instanceName":"2"}),makeQuery(id+"F2.opPattern","COPY",FACE,{"derivedFrom":subQ1,"instanceName":"3"}),makeQuery(id+"F2.opPattern","COPY",FACE,{"derivedFrom":subQ1,"instanceName":"4"}),makeQuery(id+"F2.opPattern","COPY",FACE,{"derivedFrom":subQ1,"instanceName":"5"}),makeQuery(id+"F2.opPattern","COPY",FACE,{"derivedFrom":subQ1,"instanceName":"6"}),makeQuery(id+"F2.opPattern","COPY",FACE,{"derivedFrom":subQ1,"instanceName":"7"}),makeQuery(id+"F2.opPattern","COPY",FACE,{"derivedFrom":subQ1,"instanceName":"8"}),makeQuery(id+"F2.opPattern","COPY",FACE,{"derivedFrom":subQ1,"instanceName":"9"}),makeQuery(id+"F2.opPattern","COPY",FACE,{"derivedFrom":subQ1,"instanceName":"10"}),makeQuery(id+"F2.opPattern","COPY",FACE,{"derivedFrom":subQ1,"instanceName":"11"}),makeQuery(id+"F2.opPattern","COPY",FACE,{"derivedFrom":subQ1,"instanceName":"12"}),makeQuery(id+"F2.opPattern","COPY",FACE,{"derivedFrom":subQ1,"instanceName":"13"}),makeQuery(id+"F2.opPattern","COPY",FACE,{"derivedFrom":subQ1,"instanceName":"14"}),makeQuery(id+"F2.opPattern","COPY",FACE,{"derivedFrom":subQ1,"instanceName":"15"}),makeQuery(id+"F2.opPattern","COPY",FACE,{"derivedFrom":subQ1,"instanceName":"16"}),makeQuery(id+"F2.opPattern","COPY",FACE,{"derivedFrom":subQ1,"instanceName":"17"}),makeQuery(id+"F2.opPattern","COPY",FACE,{"derivedFrom":subQ1,"instanceName":"18"}),makeQuery(id+"F2.opPattern","COPY",FACE,{"derivedFrom":subQ1,"instanceName":"19"}),makeQuery(id+"F2.opPattern","COPY",FACE,{"derivedFrom":subQ1,"instanceName":"20"}),makeQuery(id+"F2.opPattern","COPY",FACE,{"derivedFrom":subQ1,"instanceName":"21"}),makeQuery(id+"F2.opPattern","COPY",FACE,{"derivedFrom":subQ1,"instanceName":"22"}),makeQuery(id+"F2.opPattern","COPY",FACE,{"derivedFrom":subQ1,"instanceName":"23"})]})],"blendedInto":[makeQuery(id+"F2.boolean.opBoolean","MERGE",FACE,{"derivedFrom":[subQ1,makeQuery(id+"F2.opPattern","COPY",FACE,{"derivedFrom":subQ1,"instanceName":"1"}),makeQuery(id+"F2.opPattern","COPY",FACE,{"derivedFrom":subQ1,"instanceName":"2"}),makeQuery(id+"F2.opPattern","COPY",FACE,{"derivedFrom":subQ1,"instanceName":"3"}),makeQuery(id+"F2.opPattern","COPY",FACE,{"derivedFrom":subQ1,"instanceName":"4"}),makeQuery(id+"F2.opPattern","COPY",FACE,{"derivedFrom":subQ1,"instanceName":"5"}),makeQuery(id+"F2.opPattern","COPY",FACE,{"derivedFrom":subQ1,"instanceName":"6"}),makeQuery(id+"F2.opPattern","COPY",FACE,{"derivedFrom":subQ1,"instanceName":"7"}),makeQuery(id+"F2.opPattern","COPY",FACE,{"derivedFrom":subQ1,"instanceName":"8"}),makeQuery(id+"F2.opPattern","COPY",FACE,{"derivedFrom":subQ1,"instanceName":"9"}),makeQuery(id+"F2.opPattern","COPY",FACE,{"derivedFrom":subQ1,"instanceName":"10"}),makeQuery(id+"F2.opPattern","COPY",FACE,{"derivedFrom":subQ1,"instanceName":"11"}),makeQuery(id+"F2.opPattern","COPY",FACE,{"derivedFrom":subQ1,"instanceName":"12"}),makeQuery(id+"F2.opPattern","COPY",FACE,{"derivedFrom":subQ1,"instanceName":"13"}),makeQuery(id+"F2.opPattern","COPY",FACE,{"derivedFrom":subQ1,"instanceName":"14"}),makeQuery(id+"F2.opPattern","COPY",FACE,{"derivedFrom":subQ1,"instanceName":"15"}),makeQuery(id+"F2.opPattern","COPY",FACE,{"derivedFrom":subQ1,"instanceName":"16"}),makeQuery(id+"F2.opPattern","COPY",FACE,{"derivedFrom":subQ1,"instanceName":"17"}),makeQuery(id+"F2.opPattern","COPY",FACE,{"derivedFrom":subQ1,"instanceName":"18"}),makeQuery(id+"F2.opPattern","COPY",FACE,{"derivedFrom":subQ1,"instanceName":"19"}),makeQuery(id+"F2.opPattern","COPY",FACE,{"derivedFrom":subQ1,"instanceName":"20"}),makeQuery(id+"F2.opPattern","COPY",FACE,{"derivedFrom":subQ1,"instanceName":"21"}),makeQuery(id+"F2.opPattern","COPY",FACE,{"derivedFrom":subQ1,"instanceName":"22"}),makeQuery(id+"F2.opPattern","COPY",FACE,{"derivedFrom":subQ1,"instanceName":"23"})]})]});}
            var Q33;
            {var subQ0=sQuery(id+"F0.wireOp",EDGE,"E12");var subQ1=makeQuery(id+"F1.opExtrude","CAP_FACE",FACE,{"disambiguationData":[OSD([sQuery(id+"F0.wireOp",EDGE,"E2"),sQuery(id+"F0.wireOp",EDGE,"E11"),subQ0,sQuery(id+"F0.wireOp",EDGE,"E13.MirrorCS"),sQuery(id+"F0.wireOp",EDGE,"E14.MirrorCS"),sQuery(id+"F0.wireOp",EDGE,"E15"),sQuery(id+"F0.wireOp",EDGE,"E19")])],"isStart":false});Q33=makeQuery(id+"F3.opFillet","BLEND_EDGE",EDGE,{"blendedFrom":[makeQuery(id+"F2.opPattern","COPY",EDGE,{"derivedFrom":makeQuery(id+"F1.opExtrude","CAP_EDGE",EDGE,{"disambiguationData":[OSD([subQ0])],"isStart":false}),"instanceName":"15"}),makeQuery(id+"F2.boolean.opBoolean","MERGE",FACE,{"derivedFrom":[subQ1,makeQuery(id+"F2.opPattern","COPY",FACE,{"derivedFrom":subQ1,"instanceName":"1"}),makeQuery(id+"F2.opPattern","COPY",FACE,{"derivedFrom":subQ1,"instanceName":"2"}),makeQuery(id+"F2.opPattern","COPY",FACE,{"derivedFrom":subQ1,"instanceName":"3"}),makeQuery(id+"F2.opPattern","COPY",FACE,{"derivedFrom":subQ1,"instanceName":"4"}),makeQuery(id+"F2.opPattern","COPY",FACE,{"derivedFrom":subQ1,"instanceName":"5"}),makeQuery(id+"F2.opPattern","COPY",FACE,{"derivedFrom":subQ1,"instanceName":"6"}),makeQuery(id+"F2.opPattern","COPY",FACE,{"derivedFrom":subQ1,"instanceName":"7"}),makeQuery(id+"F2.opPattern","COPY",FACE,{"derivedFrom":subQ1,"instanceName":"8"}),makeQuery(id+"F2.opPattern","COPY",FACE,{"derivedFrom":subQ1,"instanceName":"9"}),makeQuery(id+"F2.opPattern","COPY",FACE,{"derivedFrom":subQ1,"instanceName":"10"}),makeQuery(id+"F2.opPattern","COPY",FACE,{"derivedFrom":subQ1,"instanceName":"11"}),makeQuery(id+"F2.opPattern","COPY",FACE,{"derivedFrom":subQ1,"instanceName":"12"}),makeQuery(id+"F2.opPattern","COPY",FACE,{"derivedFrom":subQ1,"instanceName":"13"}),makeQuery(id+"F2.opPattern","COPY",FACE,{"derivedFrom":subQ1,"instanceName":"14"}),makeQuery(id+"F2.opPattern","COPY",FACE,{"derivedFrom":subQ1,"instanceName":"15"}),makeQuery(id+"F2.opPattern","COPY",FACE,{"derivedFrom":subQ1,"instanceName":"16"}),makeQuery(id+"F2.opPattern","COPY",FACE,{"derivedFrom":subQ1,"instanceName":"17"}),makeQuery(id+"F2.opPattern","COPY",FACE,{"derivedFrom":subQ1,"instanceName":"18"}),makeQuery(id+"F2.opPattern","COPY",FACE,{"derivedFrom":subQ1,"instanceName":"19"}),makeQuery(id+"F2.opPattern","COPY",FACE,{"derivedFrom":subQ1,"instanceName":"20"}),makeQuery(id+"F2.opPattern","COPY",FACE,{"derivedFrom":subQ1,"instanceName":"21"}),makeQuery(id+"F2.opPattern","COPY",FACE,{"derivedFrom":subQ1,"instanceName":"22"}),makeQuery(id+"F2.opPattern","COPY",FACE,{"derivedFrom":subQ1,"instanceName":"23"})]})],"blendedInto":[makeQuery(id+"F2.boolean.opBoolean","MERGE",FACE,{"derivedFrom":[subQ1,makeQuery(id+"F2.opPattern","COPY",FACE,{"derivedFrom":subQ1,"instanceName":"1"}),makeQuery(id+"F2.opPattern","COPY",FACE,{"derivedFrom":subQ1,"instanceName":"2"}),makeQuery(id+"F2.opPattern","COPY",FACE,{"derivedFrom":subQ1,"instanceName":"3"}),makeQuery(id+"F2.opPattern","COPY",FACE,{"derivedFrom":subQ1,"instanceName":"4"}),makeQuery(id+"F2.opPattern","COPY",FACE,{"derivedFrom":subQ1,"instanceName":"5"}),makeQuery(id+"F2.opPattern","COPY",FACE,{"derivedFrom":subQ1,"instanceName":"6"}),makeQuery(id+"F2.opPattern","COPY",FACE,{"derivedFrom":subQ1,"instanceName":"7"}),makeQuery(id+"F2.opPattern","COPY",FACE,{"derivedFrom":subQ1,"instanceName":"8"}),makeQuery(id+"F2.opPattern","COPY",FACE,{"derivedFrom":subQ1,"instanceName":"9"}),makeQuery(id+"F2.opPattern","COPY",FACE,{"derivedFrom":subQ1,"instanceName":"10"}),makeQuery(id+"F2.opPattern","COPY",FACE,{"derivedFrom":subQ1,"instanceName":"11"}),makeQuery(id+"F2.opPattern","COPY",FACE,{"derivedFrom":subQ1,"instanceName":"12"}),makeQuery(id+"F2.opPattern","COPY",FACE,{"derivedFrom":subQ1,"instanceName":"13"}),makeQuery(id+"F2.opPattern","COPY",FACE,{"derivedFrom":subQ1,"instanceName":"14"}),makeQuery(id+"F2.opPattern","COPY",FACE,{"derivedFrom":subQ1,"instanceName":"15"}),makeQuery(id+"F2.opPattern","COPY",FACE,{"derivedFrom":subQ1,"instanceName":"16"}),makeQuery(id+"F2.opPattern","COPY",FACE,{"derivedFrom":subQ1,"instanceName":"17"}),makeQuery(id+"F2.opPattern","COPY",FACE,{"derivedFrom":subQ1,"instanceName":"18"}),makeQuery(id+"F2.opPattern","COPY",FACE,{"derivedFrom":subQ1,"instanceName":"19"}),makeQuery(id+"F2.opPattern","COPY",FACE,{"derivedFrom":subQ1,"instanceName":"20"}),makeQuery(id+"F2.opPattern","COPY",FACE,{"derivedFrom":subQ1,"instanceName":"21"}),makeQuery(id+"F2.opPattern","COPY",FACE,{"derivedFrom":subQ1,"instanceName":"22"}),makeQuery(id+"F2.opPattern","COPY",FACE,{"derivedFrom":subQ1,"instanceName":"23"})]})]});}
            var Q34;
            {var subQ0=sQuery(id+"F0.wireOp",EDGE,"E14.MirrorCS");var subQ1=makeQuery(id+"F1.opExtrude","CAP_FACE",FACE,{"disambiguationData":[OSD([sQuery(id+"F0.wireOp",EDGE,"E2"),sQuery(id+"F0.wireOp",EDGE,"E11"),sQuery(id+"F0.wireOp",EDGE,"E12"),sQuery(id+"F0.wireOp",EDGE,"E13.MirrorCS"),subQ0,sQuery(id+"F0.wireOp",EDGE,"E15"),sQuery(id+"F0.wireOp",EDGE,"E19")])],"isStart":false});Q34=makeQuery(id+"F3.opFillet","BLEND_EDGE",EDGE,{"blendedFrom":[makeQuery(id+"F2.opPattern","COPY",EDGE,{"derivedFrom":makeQuery(id+"F1.opExtrude","CAP_EDGE",EDGE,{"disambiguationData":[OSD([subQ0])],"isStart":false}),"instanceName":"16"}),makeQuery(id+"F2.boolean.opBoolean","MERGE",FACE,{"derivedFrom":[subQ1,makeQuery(id+"F2.opPattern","COPY",FACE,{"derivedFrom":subQ1,"instanceName":"1"}),makeQuery(id+"F2.opPattern","COPY",FACE,{"derivedFrom":subQ1,"instanceName":"2"}),makeQuery(id+"F2.opPattern","COPY",FACE,{"derivedFrom":subQ1,"instanceName":"3"}),makeQuery(id+"F2.opPattern","COPY",FACE,{"derivedFrom":subQ1,"instanceName":"4"}),makeQuery(id+"F2.opPattern","COPY",FACE,{"derivedFrom":subQ1,"instanceName":"5"}),makeQuery(id+"F2.opPattern","COPY",FACE,{"derivedFrom":subQ1,"instanceName":"6"}),makeQuery(id+"F2.opPattern","COPY",FACE,{"derivedFrom":subQ1,"instanceName":"7"}),makeQuery(id+"F2.opPattern","COPY",FACE,{"derivedFrom":subQ1,"instanceName":"8"}),makeQuery(id+"F2.opPattern","COPY",FACE,{"derivedFrom":subQ1,"instanceName":"9"}),makeQuery(id+"F2.opPattern","COPY",FACE,{"derivedFrom":subQ1,"instanceName":"10"}),makeQuery(id+"F2.opPattern","COPY",FACE,{"derivedFrom":subQ1,"instanceName":"11"}),makeQuery(id+"F2.opPattern","COPY",FACE,{"derivedFrom":subQ1,"instanceName":"12"}),makeQuery(id+"F2.opPattern","COPY",FACE,{"derivedFrom":subQ1,"instanceName":"13"}),makeQuery(id+"F2.opPattern","COPY",FACE,{"derivedFrom":subQ1,"instanceName":"14"}),makeQuery(id+"F2.opPattern","COPY",FACE,{"derivedFrom":subQ1,"instanceName":"15"}),makeQuery(id+"F2.opPattern","COPY",FACE,{"derivedFrom":subQ1,"instanceName":"16"}),makeQuery(id+"F2.opPattern","COPY",FACE,{"derivedFrom":subQ1,"instanceName":"17"}),makeQuery(id+"F2.opPattern","COPY",FACE,{"derivedFrom":subQ1,"instanceName":"18"}),makeQuery(id+"F2.opPattern","COPY",FACE,{"derivedFrom":subQ1,"instanceName":"19"}),makeQuery(id+"F2.opPattern","COPY",FACE,{"derivedFrom":subQ1,"instanceName":"20"}),makeQuery(id+"F2.opPattern","COPY",FACE,{"derivedFrom":subQ1,"instanceName":"21"}),makeQuery(id+"F2.opPattern","COPY",FACE,{"derivedFrom":subQ1,"instanceName":"22"}),makeQuery(id+"F2.opPattern","COPY",FACE,{"derivedFrom":subQ1,"instanceName":"23"})]})],"blendedInto":[makeQuery(id+"F2.boolean.opBoolean","MERGE",FACE,{"derivedFrom":[subQ1,makeQuery(id+"F2.opPattern","COPY",FACE,{"derivedFrom":subQ1,"instanceName":"1"}),makeQuery(id+"F2.opPattern","COPY",FACE,{"derivedFrom":subQ1,"instanceName":"2"}),makeQuery(id+"F2.opPattern","COPY",FACE,{"derivedFrom":subQ1,"instanceName":"3"}),makeQuery(id+"F2.opPattern","COPY",FACE,{"derivedFrom":subQ1,"instanceName":"4"}),makeQuery(id+"F2.opPattern","COPY",FACE,{"derivedFrom":subQ1,"instanceName":"5"}),makeQuery(id+"F2.opPattern","COPY",FACE,{"derivedFrom":subQ1,"instanceName":"6"}),makeQuery(id+"F2.opPattern","COPY",FACE,{"derivedFrom":subQ1,"instanceName":"7"}),makeQuery(id+"F2.opPattern","COPY",FACE,{"derivedFrom":subQ1,"instanceName":"8"}),makeQuery(id+"F2.opPattern","COPY",FACE,{"derivedFrom":subQ1,"instanceName":"9"}),makeQuery(id+"F2.opPattern","COPY",FACE,{"derivedFrom":subQ1,"instanceName":"10"}),makeQuery(id+"F2.opPattern","COPY",FACE,{"derivedFrom":subQ1,"instanceName":"11"}),makeQuery(id+"F2.opPattern","COPY",FACE,{"derivedFrom":subQ1,"instanceName":"12"}),makeQuery(id+"F2.opPattern","COPY",FACE,{"derivedFrom":subQ1,"instanceName":"13"}),makeQuery(id+"F2.opPattern","COPY",FACE,{"derivedFrom":subQ1,"instanceName":"14"}),makeQuery(id+"F2.opPattern","COPY",FACE,{"derivedFrom":subQ1,"instanceName":"15"}),makeQuery(id+"F2.opPattern","COPY",FACE,{"derivedFrom":subQ1,"instanceName":"16"}),makeQuery(id+"F2.opPattern","COPY",FACE,{"derivedFrom":subQ1,"instanceName":"17"}),makeQuery(id+"F2.opPattern","COPY",FACE,{"derivedFrom":subQ1,"instanceName":"18"}),makeQuery(id+"F2.opPattern","COPY",FACE,{"derivedFrom":subQ1,"instanceName":"19"}),makeQuery(id+"F2.opPattern","COPY",FACE,{"derivedFrom":subQ1,"instanceName":"20"}),makeQuery(id+"F2.opPattern","COPY",FACE,{"derivedFrom":subQ1,"instanceName":"21"}),makeQuery(id+"F2.opPattern","COPY",FACE,{"derivedFrom":subQ1,"instanceName":"22"}),makeQuery(id+"F2.opPattern","COPY",FACE,{"derivedFrom":subQ1,"instanceName":"23"})]})]});}
            var Q35;
            {var subQ0=sQuery(id+"F0.wireOp",EDGE,"E12");var subQ1=makeQuery(id+"F1.opExtrude","CAP_FACE",FACE,{"disambiguationData":[OSD([sQuery(id+"F0.wireOp",EDGE,"E2"),sQuery(id+"F0.wireOp",EDGE,"E11"),subQ0,sQuery(id+"F0.wireOp",EDGE,"E13.MirrorCS"),sQuery(id+"F0.wireOp",EDGE,"E14.MirrorCS"),sQuery(id+"F0.wireOp",EDGE,"E15"),sQuery(id+"F0.wireOp",EDGE,"E19")])],"isStart":false});Q35=makeQuery(id+"F3.opFillet","BLEND_EDGE",EDGE,{"blendedFrom":[makeQuery(id+"F2.opPattern","COPY",EDGE,{"derivedFrom":makeQuery(id+"F1.opExtrude","CAP_EDGE",EDGE,{"disambiguationData":[OSD([subQ0])],"isStart":false}),"instanceName":"16"}),makeQuery(id+"F2.boolean.opBoolean","MERGE",FACE,{"derivedFrom":[subQ1,makeQuery(id+"F2.opPattern","COPY",FACE,{"derivedFrom":subQ1,"instanceName":"1"}),makeQuery(id+"F2.opPattern","COPY",FACE,{"derivedFrom":subQ1,"instanceName":"2"}),makeQuery(id+"F2.opPattern","COPY",FACE,{"derivedFrom":subQ1,"instanceName":"3"}),makeQuery(id+"F2.opPattern","COPY",FACE,{"derivedFrom":subQ1,"instanceName":"4"}),makeQuery(id+"F2.opPattern","COPY",FACE,{"derivedFrom":subQ1,"instanceName":"5"}),makeQuery(id+"F2.opPattern","COPY",FACE,{"derivedFrom":subQ1,"instanceName":"6"}),makeQuery(id+"F2.opPattern","COPY",FACE,{"derivedFrom":subQ1,"instanceName":"7"}),makeQuery(id+"F2.opPattern","COPY",FACE,{"derivedFrom":subQ1,"instanceName":"8"}),makeQuery(id+"F2.opPattern","COPY",FACE,{"derivedFrom":subQ1,"instanceName":"9"}),makeQuery(id+"F2.opPattern","COPY",FACE,{"derivedFrom":subQ1,"instanceName":"10"}),makeQuery(id+"F2.opPattern","COPY",FACE,{"derivedFrom":subQ1,"instanceName":"11"}),makeQuery(id+"F2.opPattern","COPY",FACE,{"derivedFrom":subQ1,"instanceName":"12"}),makeQuery(id+"F2.opPattern","COPY",FACE,{"derivedFrom":subQ1,"instanceName":"13"}),makeQuery(id+"F2.opPattern","COPY",FACE,{"derivedFrom":subQ1,"instanceName":"14"}),makeQuery(id+"F2.opPattern","COPY",FACE,{"derivedFrom":subQ1,"instanceName":"15"}),makeQuery(id+"F2.opPattern","COPY",FACE,{"derivedFrom":subQ1,"instanceName":"16"}),makeQuery(id+"F2.opPattern","COPY",FACE,{"derivedFrom":subQ1,"instanceName":"17"}),makeQuery(id+"F2.opPattern","COPY",FACE,{"derivedFrom":subQ1,"instanceName":"18"}),makeQuery(id+"F2.opPattern","COPY",FACE,{"derivedFrom":subQ1,"instanceName":"19"}),makeQuery(id+"F2.opPattern","COPY",FACE,{"derivedFrom":subQ1,"instanceName":"20"}),makeQuery(id+"F2.opPattern","COPY",FACE,{"derivedFrom":subQ1,"instanceName":"21"}),makeQuery(id+"F2.opPattern","COPY",FACE,{"derivedFrom":subQ1,"instanceName":"22"}),makeQuery(id+"F2.opPattern","COPY",FACE,{"derivedFrom":subQ1,"instanceName":"23"})]})],"blendedInto":[makeQuery(id+"F2.boolean.opBoolean","MERGE",FACE,{"derivedFrom":[subQ1,makeQuery(id+"F2.opPattern","COPY",FACE,{"derivedFrom":subQ1,"instanceName":"1"}),makeQuery(id+"F2.opPattern","COPY",FACE,{"derivedFrom":subQ1,"instanceName":"2"}),makeQuery(id+"F2.opPattern","COPY",FACE,{"derivedFrom":subQ1,"instanceName":"3"}),makeQuery(id+"F2.opPattern","COPY",FACE,{"derivedFrom":subQ1,"instanceName":"4"}),makeQuery(id+"F2.opPattern","COPY",FACE,{"derivedFrom":subQ1,"instanceName":"5"}),makeQuery(id+"F2.opPattern","COPY",FACE,{"derivedFrom":subQ1,"instanceName":"6"}),makeQuery(id+"F2.opPattern","COPY",FACE,{"derivedFrom":subQ1,"instanceName":"7"}),makeQuery(id+"F2.opPattern","COPY",FACE,{"derivedFrom":subQ1,"instanceName":"8"}),makeQuery(id+"F2.opPattern","COPY",FACE,{"derivedFrom":subQ1,"instanceName":"9"}),makeQuery(id+"F2.opPattern","COPY",FACE,{"derivedFrom":subQ1,"instanceName":"10"}),makeQuery(id+"F2.opPattern","COPY",FACE,{"derivedFrom":subQ1,"instanceName":"11"}),makeQuery(id+"F2.opPattern","COPY",FACE,{"derivedFrom":subQ1,"instanceName":"12"}),makeQuery(id+"F2.opPattern","COPY",FACE,{"derivedFrom":subQ1,"instanceName":"13"}),makeQuery(id+"F2.opPattern","COPY",FACE,{"derivedFrom":subQ1,"instanceName":"14"}),makeQuery(id+"F2.opPattern","COPY",FACE,{"derivedFrom":subQ1,"instanceName":"15"}),makeQuery(id+"F2.opPattern","COPY",FACE,{"derivedFrom":subQ1,"instanceName":"16"}),makeQuery(id+"F2.opPattern","COPY",FACE,{"derivedFrom":subQ1,"instanceName":"17"}),makeQuery(id+"F2.opPattern","COPY",FACE,{"derivedFrom":subQ1,"instanceName":"18"}),makeQuery(id+"F2.opPattern","COPY",FACE,{"derivedFrom":subQ1,"instanceName":"19"}),makeQuery(id+"F2.opPattern","COPY",FACE,{"derivedFrom":subQ1,"instanceName":"20"}),makeQuery(id+"F2.opPattern","COPY",FACE,{"derivedFrom":subQ1,"instanceName":"21"}),makeQuery(id+"F2.opPattern","COPY",FACE,{"derivedFrom":subQ1,"instanceName":"22"}),makeQuery(id+"F2.opPattern","COPY",FACE,{"derivedFrom":subQ1,"instanceName":"23"})]})]});}
            var Q36;
            {var subQ0=sQuery(id+"F0.wireOp",EDGE,"E12");var subQ1=makeQuery(id+"F1.opExtrude","CAP_FACE",FACE,{"disambiguationData":[OSD([sQuery(id+"F0.wireOp",EDGE,"E2"),sQuery(id+"F0.wireOp",EDGE,"E11"),subQ0,sQuery(id+"F0.wireOp",EDGE,"E13.MirrorCS"),sQuery(id+"F0.wireOp",EDGE,"E14.MirrorCS"),sQuery(id+"F0.wireOp",EDGE,"E15"),sQuery(id+"F0.wireOp",EDGE,"E19")])],"isStart":false});Q36=makeQuery(id+"F3.opFillet","BLEND_EDGE",EDGE,{"blendedFrom":[makeQuery(id+"F2.opPattern","COPY",EDGE,{"derivedFrom":makeQuery(id+"F1.opExtrude","CAP_EDGE",EDGE,{"disambiguationData":[OSD([subQ0])],"isStart":false}),"instanceName":"17"}),makeQuery(id+"F2.boolean.opBoolean","MERGE",FACE,{"derivedFrom":[subQ1,makeQuery(id+"F2.opPattern","COPY",FACE,{"derivedFrom":subQ1,"instanceName":"1"}),makeQuery(id+"F2.opPattern","COPY",FACE,{"derivedFrom":subQ1,"instanceName":"2"}),makeQuery(id+"F2.opPattern","COPY",FACE,{"derivedFrom":subQ1,"instanceName":"3"}),makeQuery(id+"F2.opPattern","COPY",FACE,{"derivedFrom":subQ1,"instanceName":"4"}),makeQuery(id+"F2.opPattern","COPY",FACE,{"derivedFrom":subQ1,"instanceName":"5"}),makeQuery(id+"F2.opPattern","COPY",FACE,{"derivedFrom":subQ1,"instanceName":"6"}),makeQuery(id+"F2.opPattern","COPY",FACE,{"derivedFrom":subQ1,"instanceName":"7"}),makeQuery(id+"F2.opPattern","COPY",FACE,{"derivedFrom":subQ1,"instanceName":"8"}),makeQuery(id+"F2.opPattern","COPY",FACE,{"derivedFrom":subQ1,"instanceName":"9"}),makeQuery(id+"F2.opPattern","COPY",FACE,{"derivedFrom":subQ1,"instanceName":"10"}),makeQuery(id+"F2.opPattern","COPY",FACE,{"derivedFrom":subQ1,"instanceName":"11"}),makeQuery(id+"F2.opPattern","COPY",FACE,{"derivedFrom":subQ1,"instanceName":"12"}),makeQuery(id+"F2.opPattern","COPY",FACE,{"derivedFrom":subQ1,"instanceName":"13"}),makeQuery(id+"F2.opPattern","COPY",FACE,{"derivedFrom":subQ1,"instanceName":"14"}),makeQuery(id+"F2.opPattern","COPY",FACE,{"derivedFrom":subQ1,"instanceName":"15"}),makeQuery(id+"F2.opPattern","COPY",FACE,{"derivedFrom":subQ1,"instanceName":"16"}),makeQuery(id+"F2.opPattern","COPY",FACE,{"derivedFrom":subQ1,"instanceName":"17"}),makeQuery(id+"F2.opPattern","COPY",FACE,{"derivedFrom":subQ1,"instanceName":"18"}),makeQuery(id+"F2.opPattern","COPY",FACE,{"derivedFrom":subQ1,"instanceName":"19"}),makeQuery(id+"F2.opPattern","COPY",FACE,{"derivedFrom":subQ1,"instanceName":"20"}),makeQuery(id+"F2.opPattern","COPY",FACE,{"derivedFrom":subQ1,"instanceName":"21"}),makeQuery(id+"F2.opPattern","COPY",FACE,{"derivedFrom":subQ1,"instanceName":"22"}),makeQuery(id+"F2.opPattern","COPY",FACE,{"derivedFrom":subQ1,"instanceName":"23"})]})],"blendedInto":[makeQuery(id+"F2.boolean.opBoolean","MERGE",FACE,{"derivedFrom":[subQ1,makeQuery(id+"F2.opPattern","COPY",FACE,{"derivedFrom":subQ1,"instanceName":"1"}),makeQuery(id+"F2.opPattern","COPY",FACE,{"derivedFrom":subQ1,"instanceName":"2"}),makeQuery(id+"F2.opPattern","COPY",FACE,{"derivedFrom":subQ1,"instanceName":"3"}),makeQuery(id+"F2.opPattern","COPY",FACE,{"derivedFrom":subQ1,"instanceName":"4"}),makeQuery(id+"F2.opPattern","COPY",FACE,{"derivedFrom":subQ1,"instanceName":"5"}),makeQuery(id+"F2.opPattern","COPY",FACE,{"derivedFrom":subQ1,"instanceName":"6"}),makeQuery(id+"F2.opPattern","COPY",FACE,{"derivedFrom":subQ1,"instanceName":"7"}),makeQuery(id+"F2.opPattern","COPY",FACE,{"derivedFrom":subQ1,"instanceName":"8"}),makeQuery(id+"F2.opPattern","COPY",FACE,{"derivedFrom":subQ1,"instanceName":"9"}),makeQuery(id+"F2.opPattern","COPY",FACE,{"derivedFrom":subQ1,"instanceName":"10"}),makeQuery(id+"F2.opPattern","COPY",FACE,{"derivedFrom":subQ1,"instanceName":"11"}),makeQuery(id+"F2.opPattern","COPY",FACE,{"derivedFrom":subQ1,"instanceName":"12"}),makeQuery(id+"F2.opPattern","COPY",FACE,{"derivedFrom":subQ1,"instanceName":"13"}),makeQuery(id+"F2.opPattern","COPY",FACE,{"derivedFrom":subQ1,"instanceName":"14"}),makeQuery(id+"F2.opPattern","COPY",FACE,{"derivedFrom":subQ1,"instanceName":"15"}),makeQuery(id+"F2.opPattern","COPY",FACE,{"derivedFrom":subQ1,"instanceName":"16"}),makeQuery(id+"F2.opPattern","COPY",FACE,{"derivedFrom":subQ1,"instanceName":"17"}),makeQuery(id+"F2.opPattern","COPY",FACE,{"derivedFrom":subQ1,"instanceName":"18"}),makeQuery(id+"F2.opPattern","COPY",FACE,{"derivedFrom":subQ1,"instanceName":"19"}),makeQuery(id+"F2.opPattern","COPY",FACE,{"derivedFrom":subQ1,"instanceName":"20"}),makeQuery(id+"F2.opPattern","COPY",FACE,{"derivedFrom":subQ1,"instanceName":"21"}),makeQuery(id+"F2.opPattern","COPY",FACE,{"derivedFrom":subQ1,"instanceName":"22"}),makeQuery(id+"F2.opPattern","COPY",FACE,{"derivedFrom":subQ1,"instanceName":"23"})]})]});}
            var Q37;
            {var subQ0=sQuery(id+"F0.wireOp",EDGE,"E14.MirrorCS");var subQ1=makeQuery(id+"F1.opExtrude","CAP_FACE",FACE,{"disambiguationData":[OSD([sQuery(id+"F0.wireOp",EDGE,"E2"),sQuery(id+"F0.wireOp",EDGE,"E11"),sQuery(id+"F0.wireOp",EDGE,"E12"),sQuery(id+"F0.wireOp",EDGE,"E13.MirrorCS"),subQ0,sQuery(id+"F0.wireOp",EDGE,"E15"),sQuery(id+"F0.wireOp",EDGE,"E19")])],"isStart":false});Q37=makeQuery(id+"F3.opFillet","BLEND_EDGE",EDGE,{"blendedFrom":[makeQuery(id+"F2.opPattern","COPY",EDGE,{"derivedFrom":makeQuery(id+"F1.opExtrude","CAP_EDGE",EDGE,{"disambiguationData":[OSD([subQ0])],"isStart":false}),"instanceName":"17"}),makeQuery(id+"F2.boolean.opBoolean","MERGE",FACE,{"derivedFrom":[subQ1,makeQuery(id+"F2.opPattern","COPY",FACE,{"derivedFrom":subQ1,"instanceName":"1"}),makeQuery(id+"F2.opPattern","COPY",FACE,{"derivedFrom":subQ1,"instanceName":"2"}),makeQuery(id+"F2.opPattern","COPY",FACE,{"derivedFrom":subQ1,"instanceName":"3"}),makeQuery(id+"F2.opPattern","COPY",FACE,{"derivedFrom":subQ1,"instanceName":"4"}),makeQuery(id+"F2.opPattern","COPY",FACE,{"derivedFrom":subQ1,"instanceName":"5"}),makeQuery(id+"F2.opPattern","COPY",FACE,{"derivedFrom":subQ1,"instanceName":"6"}),makeQuery(id+"F2.opPattern","COPY",FACE,{"derivedFrom":subQ1,"instanceName":"7"}),makeQuery(id+"F2.opPattern","COPY",FACE,{"derivedFrom":subQ1,"instanceName":"8"}),makeQuery(id+"F2.opPattern","COPY",FACE,{"derivedFrom":subQ1,"instanceName":"9"}),makeQuery(id+"F2.opPattern","COPY",FACE,{"derivedFrom":subQ1,"instanceName":"10"}),makeQuery(id+"F2.opPattern","COPY",FACE,{"derivedFrom":subQ1,"instanceName":"11"}),makeQuery(id+"F2.opPattern","COPY",FACE,{"derivedFrom":subQ1,"instanceName":"12"}),makeQuery(id+"F2.opPattern","COPY",FACE,{"derivedFrom":subQ1,"instanceName":"13"}),makeQuery(id+"F2.opPattern","COPY",FACE,{"derivedFrom":subQ1,"instanceName":"14"}),makeQuery(id+"F2.opPattern","COPY",FACE,{"derivedFrom":subQ1,"instanceName":"15"}),makeQuery(id+"F2.opPattern","COPY",FACE,{"derivedFrom":subQ1,"instanceName":"16"}),makeQuery(id+"F2.opPattern","COPY",FACE,{"derivedFrom":subQ1,"instanceName":"17"}),makeQuery(id+"F2.opPattern","COPY",FACE,{"derivedFrom":subQ1,"instanceName":"18"}),makeQuery(id+"F2.opPattern","COPY",FACE,{"derivedFrom":subQ1,"instanceName":"19"}),makeQuery(id+"F2.opPattern","COPY",FACE,{"derivedFrom":subQ1,"instanceName":"20"}),makeQuery(id+"F2.opPattern","COPY",FACE,{"derivedFrom":subQ1,"instanceName":"21"}),makeQuery(id+"F2.opPattern","COPY",FACE,{"derivedFrom":subQ1,"instanceName":"22"}),makeQuery(id+"F2.opPattern","COPY",FACE,{"derivedFrom":subQ1,"instanceName":"23"})]})],"blendedInto":[makeQuery(id+"F2.boolean.opBoolean","MERGE",FACE,{"derivedFrom":[subQ1,makeQuery(id+"F2.opPattern","COPY",FACE,{"derivedFrom":subQ1,"instanceName":"1"}),makeQuery(id+"F2.opPattern","COPY",FACE,{"derivedFrom":subQ1,"instanceName":"2"}),makeQuery(id+"F2.opPattern","COPY",FACE,{"derivedFrom":subQ1,"instanceName":"3"}),makeQuery(id+"F2.opPattern","COPY",FACE,{"derivedFrom":subQ1,"instanceName":"4"}),makeQuery(id+"F2.opPattern","COPY",FACE,{"derivedFrom":subQ1,"instanceName":"5"}),makeQuery(id+"F2.opPattern","COPY",FACE,{"derivedFrom":subQ1,"instanceName":"6"}),makeQuery(id+"F2.opPattern","COPY",FACE,{"derivedFrom":subQ1,"instanceName":"7"}),makeQuery(id+"F2.opPattern","COPY",FACE,{"derivedFrom":subQ1,"instanceName":"8"}),makeQuery(id+"F2.opPattern","COPY",FACE,{"derivedFrom":subQ1,"instanceName":"9"}),makeQuery(id+"F2.opPattern","COPY",FACE,{"derivedFrom":subQ1,"instanceName":"10"}),makeQuery(id+"F2.opPattern","COPY",FACE,{"derivedFrom":subQ1,"instanceName":"11"}),makeQuery(id+"F2.opPattern","COPY",FACE,{"derivedFrom":subQ1,"instanceName":"12"}),makeQuery(id+"F2.opPattern","COPY",FACE,{"derivedFrom":subQ1,"instanceName":"13"}),makeQuery(id+"F2.opPattern","COPY",FACE,{"derivedFrom":subQ1,"instanceName":"14"}),makeQuery(id+"F2.opPattern","COPY",FACE,{"derivedFrom":subQ1,"instanceName":"15"}),makeQuery(id+"F2.opPattern","COPY",FACE,{"derivedFrom":subQ1,"instanceName":"16"}),makeQuery(id+"F2.opPattern","COPY",FACE,{"derivedFrom":subQ1,"instanceName":"17"}),makeQuery(id+"F2.opPattern","COPY",FACE,{"derivedFrom":subQ1,"instanceName":"18"}),makeQuery(id+"F2.opPattern","COPY",FACE,{"derivedFrom":subQ1,"instanceName":"19"}),makeQuery(id+"F2.opPattern","COPY",FACE,{"derivedFrom":subQ1,"instanceName":"20"}),makeQuery(id+"F2.opPattern","COPY",FACE,{"derivedFrom":subQ1,"instanceName":"21"}),makeQuery(id+"F2.opPattern","COPY",FACE,{"derivedFrom":subQ1,"instanceName":"22"}),makeQuery(id+"F2.opPattern","COPY",FACE,{"derivedFrom":subQ1,"instanceName":"23"})]})]});}
            var Q38;
            {var subQ0=sQuery(id+"F0.wireOp",EDGE,"E14.MirrorCS");var subQ1=makeQuery(id+"F1.opExtrude","CAP_FACE",FACE,{"disambiguationData":[OSD([sQuery(id+"F0.wireOp",EDGE,"E2"),sQuery(id+"F0.wireOp",EDGE,"E11"),sQuery(id+"F0.wireOp",EDGE,"E12"),sQuery(id+"F0.wireOp",EDGE,"E13.MirrorCS"),subQ0,sQuery(id+"F0.wireOp",EDGE,"E15"),sQuery(id+"F0.wireOp",EDGE,"E19")])],"isStart":false});Q38=makeQuery(id+"F3.opFillet","BLEND_EDGE",EDGE,{"blendedFrom":[makeQuery(id+"F2.opPattern","COPY",EDGE,{"derivedFrom":makeQuery(id+"F1.opExtrude","CAP_EDGE",EDGE,{"disambiguationData":[OSD([subQ0])],"isStart":false}),"instanceName":"18"}),makeQuery(id+"F2.boolean.opBoolean","MERGE",FACE,{"derivedFrom":[subQ1,makeQuery(id+"F2.opPattern","COPY",FACE,{"derivedFrom":subQ1,"instanceName":"1"}),makeQuery(id+"F2.opPattern","COPY",FACE,{"derivedFrom":subQ1,"instanceName":"2"}),makeQuery(id+"F2.opPattern","COPY",FACE,{"derivedFrom":subQ1,"instanceName":"3"}),makeQuery(id+"F2.opPattern","COPY",FACE,{"derivedFrom":subQ1,"instanceName":"4"}),makeQuery(id+"F2.opPattern","COPY",FACE,{"derivedFrom":subQ1,"instanceName":"5"}),makeQuery(id+"F2.opPattern","COPY",FACE,{"derivedFrom":subQ1,"instanceName":"6"}),makeQuery(id+"F2.opPattern","COPY",FACE,{"derivedFrom":subQ1,"instanceName":"7"}),makeQuery(id+"F2.opPattern","COPY",FACE,{"derivedFrom":subQ1,"instanceName":"8"}),makeQuery(id+"F2.opPattern","COPY",FACE,{"derivedFrom":subQ1,"instanceName":"9"}),makeQuery(id+"F2.opPattern","COPY",FACE,{"derivedFrom":subQ1,"instanceName":"10"}),makeQuery(id+"F2.opPattern","COPY",FACE,{"derivedFrom":subQ1,"instanceName":"11"}),makeQuery(id+"F2.opPattern","COPY",FACE,{"derivedFrom":subQ1,"instanceName":"12"}),makeQuery(id+"F2.opPattern","COPY",FACE,{"derivedFrom":subQ1,"instanceName":"13"}),makeQuery(id+"F2.opPattern","COPY",FACE,{"derivedFrom":subQ1,"instanceName":"14"}),makeQuery(id+"F2.opPattern","COPY",FACE,{"derivedFrom":subQ1,"instanceName":"15"}),makeQuery(id+"F2.opPattern","COPY",FACE,{"derivedFrom":subQ1,"instanceName":"16"}),makeQuery(id+"F2.opPattern","COPY",FACE,{"derivedFrom":subQ1,"instanceName":"17"}),makeQuery(id+"F2.opPattern","COPY",FACE,{"derivedFrom":subQ1,"instanceName":"18"}),makeQuery(id+"F2.opPattern","COPY",FACE,{"derivedFrom":subQ1,"instanceName":"19"}),makeQuery(id+"F2.opPattern","COPY",FACE,{"derivedFrom":subQ1,"instanceName":"20"}),makeQuery(id+"F2.opPattern","COPY",FACE,{"derivedFrom":subQ1,"instanceName":"21"}),makeQuery(id+"F2.opPattern","COPY",FACE,{"derivedFrom":subQ1,"instanceName":"22"}),makeQuery(id+"F2.opPattern","COPY",FACE,{"derivedFrom":subQ1,"instanceName":"23"})]})],"blendedInto":[makeQuery(id+"F2.boolean.opBoolean","MERGE",FACE,{"derivedFrom":[subQ1,makeQuery(id+"F2.opPattern","COPY",FACE,{"derivedFrom":subQ1,"instanceName":"1"}),makeQuery(id+"F2.opPattern","COPY",FACE,{"derivedFrom":subQ1,"instanceName":"2"}),makeQuery(id+"F2.opPattern","COPY",FACE,{"derivedFrom":subQ1,"instanceName":"3"}),makeQuery(id+"F2.opPattern","COPY",FACE,{"derivedFrom":subQ1,"instanceName":"4"}),makeQuery(id+"F2.opPattern","COPY",FACE,{"derivedFrom":subQ1,"instanceName":"5"}),makeQuery(id+"F2.opPattern","COPY",FACE,{"derivedFrom":subQ1,"instanceName":"6"}),makeQuery(id+"F2.opPattern","COPY",FACE,{"derivedFrom":subQ1,"instanceName":"7"}),makeQuery(id+"F2.opPattern","COPY",FACE,{"derivedFrom":subQ1,"instanceName":"8"}),makeQuery(id+"F2.opPattern","COPY",FACE,{"derivedFrom":subQ1,"instanceName":"9"}),makeQuery(id+"F2.opPattern","COPY",FACE,{"derivedFrom":subQ1,"instanceName":"10"}),makeQuery(id+"F2.opPattern","COPY",FACE,{"derivedFrom":subQ1,"instanceName":"11"}),makeQuery(id+"F2.opPattern","COPY",FACE,{"derivedFrom":subQ1,"instanceName":"12"}),makeQuery(id+"F2.opPattern","COPY",FACE,{"derivedFrom":subQ1,"instanceName":"13"}),makeQuery(id+"F2.opPattern","COPY",FACE,{"derivedFrom":subQ1,"instanceName":"14"}),makeQuery(id+"F2.opPattern","COPY",FACE,{"derivedFrom":subQ1,"instanceName":"15"}),makeQuery(id+"F2.opPattern","COPY",FACE,{"derivedFrom":subQ1,"instanceName":"16"}),makeQuery(id+"F2.opPattern","COPY",FACE,{"derivedFrom":subQ1,"instanceName":"17"}),makeQuery(id+"F2.opPattern","COPY",FACE,{"derivedFrom":subQ1,"instanceName":"18"}),makeQuery(id+"F2.opPattern","COPY",FACE,{"derivedFrom":subQ1,"instanceName":"19"}),makeQuery(id+"F2.opPattern","COPY",FACE,{"derivedFrom":subQ1,"instanceName":"20"}),makeQuery(id+"F2.opPattern","COPY",FACE,{"derivedFrom":subQ1,"instanceName":"21"}),makeQuery(id+"F2.opPattern","COPY",FACE,{"derivedFrom":subQ1,"instanceName":"22"}),makeQuery(id+"F2.opPattern","COPY",FACE,{"derivedFrom":subQ1,"instanceName":"23"})]})]});}
            var Q39;
            {var subQ0=sQuery(id+"F0.wireOp",EDGE,"E12");var subQ1=makeQuery(id+"F1.opExtrude","CAP_FACE",FACE,{"disambiguationData":[OSD([sQuery(id+"F0.wireOp",EDGE,"E2"),sQuery(id+"F0.wireOp",EDGE,"E11"),subQ0,sQuery(id+"F0.wireOp",EDGE,"E13.MirrorCS"),sQuery(id+"F0.wireOp",EDGE,"E14.MirrorCS"),sQuery(id+"F0.wireOp",EDGE,"E15"),sQuery(id+"F0.wireOp",EDGE,"E19")])],"isStart":false});Q39=makeQuery(id+"F3.opFillet","BLEND_EDGE",EDGE,{"blendedFrom":[makeQuery(id+"F2.opPattern","COPY",EDGE,{"derivedFrom":makeQuery(id+"F1.opExtrude","CAP_EDGE",EDGE,{"disambiguationData":[OSD([subQ0])],"isStart":false}),"instanceName":"18"}),makeQuery(id+"F2.boolean.opBoolean","MERGE",FACE,{"derivedFrom":[subQ1,makeQuery(id+"F2.opPattern","COPY",FACE,{"derivedFrom":subQ1,"instanceName":"1"}),makeQuery(id+"F2.opPattern","COPY",FACE,{"derivedFrom":subQ1,"instanceName":"2"}),makeQuery(id+"F2.opPattern","COPY",FACE,{"derivedFrom":subQ1,"instanceName":"3"}),makeQuery(id+"F2.opPattern","COPY",FACE,{"derivedFrom":subQ1,"instanceName":"4"}),makeQuery(id+"F2.opPattern","COPY",FACE,{"derivedFrom":subQ1,"instanceName":"5"}),makeQuery(id+"F2.opPattern","COPY",FACE,{"derivedFrom":subQ1,"instanceName":"6"}),makeQuery(id+"F2.opPattern","COPY",FACE,{"derivedFrom":subQ1,"instanceName":"7"}),makeQuery(id+"F2.opPattern","COPY",FACE,{"derivedFrom":subQ1,"instanceName":"8"}),makeQuery(id+"F2.opPattern","COPY",FACE,{"derivedFrom":subQ1,"instanceName":"9"}),makeQuery(id+"F2.opPattern","COPY",FACE,{"derivedFrom":subQ1,"instanceName":"10"}),makeQuery(id+"F2.opPattern","COPY",FACE,{"derivedFrom":subQ1,"instanceName":"11"}),makeQuery(id+"F2.opPattern","COPY",FACE,{"derivedFrom":subQ1,"instanceName":"12"}),makeQuery(id+"F2.opPattern","COPY",FACE,{"derivedFrom":subQ1,"instanceName":"13"}),makeQuery(id+"F2.opPattern","COPY",FACE,{"derivedFrom":subQ1,"instanceName":"14"}),makeQuery(id+"F2.opPattern","COPY",FACE,{"derivedFrom":subQ1,"instanceName":"15"}),makeQuery(id+"F2.opPattern","COPY",FACE,{"derivedFrom":subQ1,"instanceName":"16"}),makeQuery(id+"F2.opPattern","COPY",FACE,{"derivedFrom":subQ1,"instanceName":"17"}),makeQuery(id+"F2.opPattern","COPY",FACE,{"derivedFrom":subQ1,"instanceName":"18"}),makeQuery(id+"F2.opPattern","COPY",FACE,{"derivedFrom":subQ1,"instanceName":"19"}),makeQuery(id+"F2.opPattern","COPY",FACE,{"derivedFrom":subQ1,"instanceName":"20"}),makeQuery(id+"F2.opPattern","COPY",FACE,{"derivedFrom":subQ1,"instanceName":"21"}),makeQuery(id+"F2.opPattern","COPY",FACE,{"derivedFrom":subQ1,"instanceName":"22"}),makeQuery(id+"F2.opPattern","COPY",FACE,{"derivedFrom":subQ1,"instanceName":"23"})]})],"blendedInto":[makeQuery(id+"F2.boolean.opBoolean","MERGE",FACE,{"derivedFrom":[subQ1,makeQuery(id+"F2.opPattern","COPY",FACE,{"derivedFrom":subQ1,"instanceName":"1"}),makeQuery(id+"F2.opPattern","COPY",FACE,{"derivedFrom":subQ1,"instanceName":"2"}),makeQuery(id+"F2.opPattern","COPY",FACE,{"derivedFrom":subQ1,"instanceName":"3"}),makeQuery(id+"F2.opPattern","COPY",FACE,{"derivedFrom":subQ1,"instanceName":"4"}),makeQuery(id+"F2.opPattern","COPY",FACE,{"derivedFrom":subQ1,"instanceName":"5"}),makeQuery(id+"F2.opPattern","COPY",FACE,{"derivedFrom":subQ1,"instanceName":"6"}),makeQuery(id+"F2.opPattern","COPY",FACE,{"derivedFrom":subQ1,"instanceName":"7"}),makeQuery(id+"F2.opPattern","COPY",FACE,{"derivedFrom":subQ1,"instanceName":"8"}),makeQuery(id+"F2.opPattern","COPY",FACE,{"derivedFrom":subQ1,"instanceName":"9"}),makeQuery(id+"F2.opPattern","COPY",FACE,{"derivedFrom":subQ1,"instanceName":"10"}),makeQuery(id+"F2.opPattern","COPY",FACE,{"derivedFrom":subQ1,"instanceName":"11"}),makeQuery(id+"F2.opPattern","COPY",FACE,{"derivedFrom":subQ1,"instanceName":"12"}),makeQuery(id+"F2.opPattern","COPY",FACE,{"derivedFrom":subQ1,"instanceName":"13"}),makeQuery(id+"F2.opPattern","COPY",FACE,{"derivedFrom":subQ1,"instanceName":"14"}),makeQuery(id+"F2.opPattern","COPY",FACE,{"derivedFrom":subQ1,"instanceName":"15"}),makeQuery(id+"F2.opPattern","COPY",FACE,{"derivedFrom":subQ1,"instanceName":"16"}),makeQuery(id+"F2.opPattern","COPY",FACE,{"derivedFrom":subQ1,"instanceName":"17"}),makeQuery(id+"F2.opPattern","COPY",FACE,{"derivedFrom":subQ1,"instanceName":"18"}),makeQuery(id+"F2.opPattern","COPY",FACE,{"derivedFrom":subQ1,"instanceName":"19"}),makeQuery(id+"F2.opPattern","COPY",FACE,{"derivedFrom":subQ1,"instanceName":"20"}),makeQuery(id+"F2.opPattern","COPY",FACE,{"derivedFrom":subQ1,"instanceName":"21"}),makeQuery(id+"F2.opPattern","COPY",FACE,{"derivedFrom":subQ1,"instanceName":"22"}),makeQuery(id+"F2.opPattern","COPY",FACE,{"derivedFrom":subQ1,"instanceName":"23"})]})]});}
            var Q40;
            {var subQ0=sQuery(id+"F0.wireOp",EDGE,"E14.MirrorCS");var subQ1=makeQuery(id+"F1.opExtrude","CAP_FACE",FACE,{"disambiguationData":[OSD([sQuery(id+"F0.wireOp",EDGE,"E2"),sQuery(id+"F0.wireOp",EDGE,"E11"),sQuery(id+"F0.wireOp",EDGE,"E12"),sQuery(id+"F0.wireOp",EDGE,"E13.MirrorCS"),subQ0,sQuery(id+"F0.wireOp",EDGE,"E15"),sQuery(id+"F0.wireOp",EDGE,"E19")])],"isStart":false});Q40=makeQuery(id+"F3.opFillet","BLEND_EDGE",EDGE,{"blendedFrom":[makeQuery(id+"F2.opPattern","COPY",EDGE,{"derivedFrom":makeQuery(id+"F1.opExtrude","CAP_EDGE",EDGE,{"disambiguationData":[OSD([subQ0])],"isStart":false}),"instanceName":"19"}),makeQuery(id+"F2.boolean.opBoolean","MERGE",FACE,{"derivedFrom":[subQ1,makeQuery(id+"F2.opPattern","COPY",FACE,{"derivedFrom":subQ1,"instanceName":"1"}),makeQuery(id+"F2.opPattern","COPY",FACE,{"derivedFrom":subQ1,"instanceName":"2"}),makeQuery(id+"F2.opPattern","COPY",FACE,{"derivedFrom":subQ1,"instanceName":"3"}),makeQuery(id+"F2.opPattern","COPY",FACE,{"derivedFrom":subQ1,"instanceName":"4"}),makeQuery(id+"F2.opPattern","COPY",FACE,{"derivedFrom":subQ1,"instanceName":"5"}),makeQuery(id+"F2.opPattern","COPY",FACE,{"derivedFrom":subQ1,"instanceName":"6"}),makeQuery(id+"F2.opPattern","COPY",FACE,{"derivedFrom":subQ1,"instanceName":"7"}),makeQuery(id+"F2.opPattern","COPY",FACE,{"derivedFrom":subQ1,"instanceName":"8"}),makeQuery(id+"F2.opPattern","COPY",FACE,{"derivedFrom":subQ1,"instanceName":"9"}),makeQuery(id+"F2.opPattern","COPY",FACE,{"derivedFrom":subQ1,"instanceName":"10"}),makeQuery(id+"F2.opPattern","COPY",FACE,{"derivedFrom":subQ1,"instanceName":"11"}),makeQuery(id+"F2.opPattern","COPY",FACE,{"derivedFrom":subQ1,"instanceName":"12"}),makeQuery(id+"F2.opPattern","COPY",FACE,{"derivedFrom":subQ1,"instanceName":"13"}),makeQuery(id+"F2.opPattern","COPY",FACE,{"derivedFrom":subQ1,"instanceName":"14"}),makeQuery(id+"F2.opPattern","COPY",FACE,{"derivedFrom":subQ1,"instanceName":"15"}),makeQuery(id+"F2.opPattern","COPY",FACE,{"derivedFrom":subQ1,"instanceName":"16"}),makeQuery(id+"F2.opPattern","COPY",FACE,{"derivedFrom":subQ1,"instanceName":"17"}),makeQuery(id+"F2.opPattern","COPY",FACE,{"derivedFrom":subQ1,"instanceName":"18"}),makeQuery(id+"F2.opPattern","COPY",FACE,{"derivedFrom":subQ1,"instanceName":"19"}),makeQuery(id+"F2.opPattern","COPY",FACE,{"derivedFrom":subQ1,"instanceName":"20"}),makeQuery(id+"F2.opPattern","COPY",FACE,{"derivedFrom":subQ1,"instanceName":"21"}),makeQuery(id+"F2.opPattern","COPY",FACE,{"derivedFrom":subQ1,"instanceName":"22"}),makeQuery(id+"F2.opPattern","COPY",FACE,{"derivedFrom":subQ1,"instanceName":"23"})]})],"blendedInto":[makeQuery(id+"F2.boolean.opBoolean","MERGE",FACE,{"derivedFrom":[subQ1,makeQuery(id+"F2.opPattern","COPY",FACE,{"derivedFrom":subQ1,"instanceName":"1"}),makeQuery(id+"F2.opPattern","COPY",FACE,{"derivedFrom":subQ1,"instanceName":"2"}),makeQuery(id+"F2.opPattern","COPY",FACE,{"derivedFrom":subQ1,"instanceName":"3"}),makeQuery(id+"F2.opPattern","COPY",FACE,{"derivedFrom":subQ1,"instanceName":"4"}),makeQuery(id+"F2.opPattern","COPY",FACE,{"derivedFrom":subQ1,"instanceName":"5"}),makeQuery(id+"F2.opPattern","COPY",FACE,{"derivedFrom":subQ1,"instanceName":"6"}),makeQuery(id+"F2.opPattern","COPY",FACE,{"derivedFrom":subQ1,"instanceName":"7"}),makeQuery(id+"F2.opPattern","COPY",FACE,{"derivedFrom":subQ1,"instanceName":"8"}),makeQuery(id+"F2.opPattern","COPY",FACE,{"derivedFrom":subQ1,"instanceName":"9"}),makeQuery(id+"F2.opPattern","COPY",FACE,{"derivedFrom":subQ1,"instanceName":"10"}),makeQuery(id+"F2.opPattern","COPY",FACE,{"derivedFrom":subQ1,"instanceName":"11"}),makeQuery(id+"F2.opPattern","COPY",FACE,{"derivedFrom":subQ1,"instanceName":"12"}),makeQuery(id+"F2.opPattern","COPY",FACE,{"derivedFrom":subQ1,"instanceName":"13"}),makeQuery(id+"F2.opPattern","COPY",FACE,{"derivedFrom":subQ1,"instanceName":"14"}),makeQuery(id+"F2.opPattern","COPY",FACE,{"derivedFrom":subQ1,"instanceName":"15"}),makeQuery(id+"F2.opPattern","COPY",FACE,{"derivedFrom":subQ1,"instanceName":"16"}),makeQuery(id+"F2.opPattern","COPY",FACE,{"derivedFrom":subQ1,"instanceName":"17"}),makeQuery(id+"F2.opPattern","COPY",FACE,{"derivedFrom":subQ1,"instanceName":"18"}),makeQuery(id+"F2.opPattern","COPY",FACE,{"derivedFrom":subQ1,"instanceName":"19"}),makeQuery(id+"F2.opPattern","COPY",FACE,{"derivedFrom":subQ1,"instanceName":"20"}),makeQuery(id+"F2.opPattern","COPY",FACE,{"derivedFrom":subQ1,"instanceName":"21"}),makeQuery(id+"F2.opPattern","COPY",FACE,{"derivedFrom":subQ1,"instanceName":"22"}),makeQuery(id+"F2.opPattern","COPY",FACE,{"derivedFrom":subQ1,"instanceName":"23"})]})]});}
            var Q41;
            {var subQ0=sQuery(id+"F0.wireOp",EDGE,"E12");var subQ1=makeQuery(id+"F1.opExtrude","CAP_FACE",FACE,{"disambiguationData":[OSD([sQuery(id+"F0.wireOp",EDGE,"E2"),sQuery(id+"F0.wireOp",EDGE,"E11"),subQ0,sQuery(id+"F0.wireOp",EDGE,"E13.MirrorCS"),sQuery(id+"F0.wireOp",EDGE,"E14.MirrorCS"),sQuery(id+"F0.wireOp",EDGE,"E15"),sQuery(id+"F0.wireOp",EDGE,"E19")])],"isStart":false});Q41=makeQuery(id+"F3.opFillet","BLEND_EDGE",EDGE,{"blendedFrom":[makeQuery(id+"F2.opPattern","COPY",EDGE,{"derivedFrom":makeQuery(id+"F1.opExtrude","CAP_EDGE",EDGE,{"disambiguationData":[OSD([subQ0])],"isStart":false}),"instanceName":"19"}),makeQuery(id+"F2.boolean.opBoolean","MERGE",FACE,{"derivedFrom":[subQ1,makeQuery(id+"F2.opPattern","COPY",FACE,{"derivedFrom":subQ1,"instanceName":"1"}),makeQuery(id+"F2.opPattern","COPY",FACE,{"derivedFrom":subQ1,"instanceName":"2"}),makeQuery(id+"F2.opPattern","COPY",FACE,{"derivedFrom":subQ1,"instanceName":"3"}),makeQuery(id+"F2.opPattern","COPY",FACE,{"derivedFrom":subQ1,"instanceName":"4"}),makeQuery(id+"F2.opPattern","COPY",FACE,{"derivedFrom":subQ1,"instanceName":"5"}),makeQuery(id+"F2.opPattern","COPY",FACE,{"derivedFrom":subQ1,"instanceName":"6"}),makeQuery(id+"F2.opPattern","COPY",FACE,{"derivedFrom":subQ1,"instanceName":"7"}),makeQuery(id+"F2.opPattern","COPY",FACE,{"derivedFrom":subQ1,"instanceName":"8"}),makeQuery(id+"F2.opPattern","COPY",FACE,{"derivedFrom":subQ1,"instanceName":"9"}),makeQuery(id+"F2.opPattern","COPY",FACE,{"derivedFrom":subQ1,"instanceName":"10"}),makeQuery(id+"F2.opPattern","COPY",FACE,{"derivedFrom":subQ1,"instanceName":"11"}),makeQuery(id+"F2.opPattern","COPY",FACE,{"derivedFrom":subQ1,"instanceName":"12"}),makeQuery(id+"F2.opPattern","COPY",FACE,{"derivedFrom":subQ1,"instanceName":"13"}),makeQuery(id+"F2.opPattern","COPY",FACE,{"derivedFrom":subQ1,"instanceName":"14"}),makeQuery(id+"F2.opPattern","COPY",FACE,{"derivedFrom":subQ1,"instanceName":"15"}),makeQuery(id+"F2.opPattern","COPY",FACE,{"derivedFrom":subQ1,"instanceName":"16"}),makeQuery(id+"F2.opPattern","COPY",FACE,{"derivedFrom":subQ1,"instanceName":"17"}),makeQuery(id+"F2.opPattern","COPY",FACE,{"derivedFrom":subQ1,"instanceName":"18"}),makeQuery(id+"F2.opPattern","COPY",FACE,{"derivedFrom":subQ1,"instanceName":"19"}),makeQuery(id+"F2.opPattern","COPY",FACE,{"derivedFrom":subQ1,"instanceName":"20"}),makeQuery(id+"F2.opPattern","COPY",FACE,{"derivedFrom":subQ1,"instanceName":"21"}),makeQuery(id+"F2.opPattern","COPY",FACE,{"derivedFrom":subQ1,"instanceName":"22"}),makeQuery(id+"F2.opPattern","COPY",FACE,{"derivedFrom":subQ1,"instanceName":"23"})]})],"blendedInto":[makeQuery(id+"F2.boolean.opBoolean","MERGE",FACE,{"derivedFrom":[subQ1,makeQuery(id+"F2.opPattern","COPY",FACE,{"derivedFrom":subQ1,"instanceName":"1"}),makeQuery(id+"F2.opPattern","COPY",FACE,{"derivedFrom":subQ1,"instanceName":"2"}),makeQuery(id+"F2.opPattern","COPY",FACE,{"derivedFrom":subQ1,"instanceName":"3"}),makeQuery(id+"F2.opPattern","COPY",FACE,{"derivedFrom":subQ1,"instanceName":"4"}),makeQuery(id+"F2.opPattern","COPY",FACE,{"derivedFrom":subQ1,"instanceName":"5"}),makeQuery(id+"F2.opPattern","COPY",FACE,{"derivedFrom":subQ1,"instanceName":"6"}),makeQuery(id+"F2.opPattern","COPY",FACE,{"derivedFrom":subQ1,"instanceName":"7"}),makeQuery(id+"F2.opPattern","COPY",FACE,{"derivedFrom":subQ1,"instanceName":"8"}),makeQuery(id+"F2.opPattern","COPY",FACE,{"derivedFrom":subQ1,"instanceName":"9"}),makeQuery(id+"F2.opPattern","COPY",FACE,{"derivedFrom":subQ1,"instanceName":"10"}),makeQuery(id+"F2.opPattern","COPY",FACE,{"derivedFrom":subQ1,"instanceName":"11"}),makeQuery(id+"F2.opPattern","COPY",FACE,{"derivedFrom":subQ1,"instanceName":"12"}),makeQuery(id+"F2.opPattern","COPY",FACE,{"derivedFrom":subQ1,"instanceName":"13"}),makeQuery(id+"F2.opPattern","COPY",FACE,{"derivedFrom":subQ1,"instanceName":"14"}),makeQuery(id+"F2.opPattern","COPY",FACE,{"derivedFrom":subQ1,"instanceName":"15"}),makeQuery(id+"F2.opPattern","COPY",FACE,{"derivedFrom":subQ1,"instanceName":"16"}),makeQuery(id+"F2.opPattern","COPY",FACE,{"derivedFrom":subQ1,"instanceName":"17"}),makeQuery(id+"F2.opPattern","COPY",FACE,{"derivedFrom":subQ1,"instanceName":"18"}),makeQuery(id+"F2.opPattern","COPY",FACE,{"derivedFrom":subQ1,"instanceName":"19"}),makeQuery(id+"F2.opPattern","COPY",FACE,{"derivedFrom":subQ1,"instanceName":"20"}),makeQuery(id+"F2.opPattern","COPY",FACE,{"derivedFrom":subQ1,"instanceName":"21"}),makeQuery(id+"F2.opPattern","COPY",FACE,{"derivedFrom":subQ1,"instanceName":"22"}),makeQuery(id+"F2.opPattern","COPY",FACE,{"derivedFrom":subQ1,"instanceName":"23"})]})]});}
            var Q42;
            {var subQ0=sQuery(id+"F0.wireOp",EDGE,"E14.MirrorCS");var subQ1=makeQuery(id+"F1.opExtrude","CAP_FACE",FACE,{"disambiguationData":[OSD([sQuery(id+"F0.wireOp",EDGE,"E2"),sQuery(id+"F0.wireOp",EDGE,"E11"),sQuery(id+"F0.wireOp",EDGE,"E12"),sQuery(id+"F0.wireOp",EDGE,"E13.MirrorCS"),subQ0,sQuery(id+"F0.wireOp",EDGE,"E15"),sQuery(id+"F0.wireOp",EDGE,"E19")])],"isStart":false});Q42=makeQuery(id+"F3.opFillet","BLEND_EDGE",EDGE,{"blendedFrom":[makeQuery(id+"F2.opPattern","COPY",EDGE,{"derivedFrom":makeQuery(id+"F1.opExtrude","CAP_EDGE",EDGE,{"disambiguationData":[OSD([subQ0])],"isStart":false}),"instanceName":"20"}),makeQuery(id+"F2.boolean.opBoolean","MERGE",FACE,{"derivedFrom":[subQ1,makeQuery(id+"F2.opPattern","COPY",FACE,{"derivedFrom":subQ1,"instanceName":"1"}),makeQuery(id+"F2.opPattern","COPY",FACE,{"derivedFrom":subQ1,"instanceName":"2"}),makeQuery(id+"F2.opPattern","COPY",FACE,{"derivedFrom":subQ1,"instanceName":"3"}),makeQuery(id+"F2.opPattern","COPY",FACE,{"derivedFrom":subQ1,"instanceName":"4"}),makeQuery(id+"F2.opPattern","COPY",FACE,{"derivedFrom":subQ1,"instanceName":"5"}),makeQuery(id+"F2.opPattern","COPY",FACE,{"derivedFrom":subQ1,"instanceName":"6"}),makeQuery(id+"F2.opPattern","COPY",FACE,{"derivedFrom":subQ1,"instanceName":"7"}),makeQuery(id+"F2.opPattern","COPY",FACE,{"derivedFrom":subQ1,"instanceName":"8"}),makeQuery(id+"F2.opPattern","COPY",FACE,{"derivedFrom":subQ1,"instanceName":"9"}),makeQuery(id+"F2.opPattern","COPY",FACE,{"derivedFrom":subQ1,"instanceName":"10"}),makeQuery(id+"F2.opPattern","COPY",FACE,{"derivedFrom":subQ1,"instanceName":"11"}),makeQuery(id+"F2.opPattern","COPY",FACE,{"derivedFrom":subQ1,"instanceName":"12"}),makeQuery(id+"F2.opPattern","COPY",FACE,{"derivedFrom":subQ1,"instanceName":"13"}),makeQuery(id+"F2.opPattern","COPY",FACE,{"derivedFrom":subQ1,"instanceName":"14"}),makeQuery(id+"F2.opPattern","COPY",FACE,{"derivedFrom":subQ1,"instanceName":"15"}),makeQuery(id+"F2.opPattern","COPY",FACE,{"derivedFrom":subQ1,"instanceName":"16"}),makeQuery(id+"F2.opPattern","COPY",FACE,{"derivedFrom":subQ1,"instanceName":"17"}),makeQuery(id+"F2.opPattern","COPY",FACE,{"derivedFrom":subQ1,"instanceName":"18"}),makeQuery(id+"F2.opPattern","COPY",FACE,{"derivedFrom":subQ1,"instanceName":"19"}),makeQuery(id+"F2.opPattern","COPY",FACE,{"derivedFrom":subQ1,"instanceName":"20"}),makeQuery(id+"F2.opPattern","COPY",FACE,{"derivedFrom":subQ1,"instanceName":"21"}),makeQuery(id+"F2.opPattern","COPY",FACE,{"derivedFrom":subQ1,"instanceName":"22"}),makeQuery(id+"F2.opPattern","COPY",FACE,{"derivedFrom":subQ1,"instanceName":"23"})]})],"blendedInto":[makeQuery(id+"F2.boolean.opBoolean","MERGE",FACE,{"derivedFrom":[subQ1,makeQuery(id+"F2.opPattern","COPY",FACE,{"derivedFrom":subQ1,"instanceName":"1"}),makeQuery(id+"F2.opPattern","COPY",FACE,{"derivedFrom":subQ1,"instanceName":"2"}),makeQuery(id+"F2.opPattern","COPY",FACE,{"derivedFrom":subQ1,"instanceName":"3"}),makeQuery(id+"F2.opPattern","COPY",FACE,{"derivedFrom":subQ1,"instanceName":"4"}),makeQuery(id+"F2.opPattern","COPY",FACE,{"derivedFrom":subQ1,"instanceName":"5"}),makeQuery(id+"F2.opPattern","COPY",FACE,{"derivedFrom":subQ1,"instanceName":"6"}),makeQuery(id+"F2.opPattern","COPY",FACE,{"derivedFrom":subQ1,"instanceName":"7"}),makeQuery(id+"F2.opPattern","COPY",FACE,{"derivedFrom":subQ1,"instanceName":"8"}),makeQuery(id+"F2.opPattern","COPY",FACE,{"derivedFrom":subQ1,"instanceName":"9"}),makeQuery(id+"F2.opPattern","COPY",FACE,{"derivedFrom":subQ1,"instanceName":"10"}),makeQuery(id+"F2.opPattern","COPY",FACE,{"derivedFrom":subQ1,"instanceName":"11"}),makeQuery(id+"F2.opPattern","COPY",FACE,{"derivedFrom":subQ1,"instanceName":"12"}),makeQuery(id+"F2.opPattern","COPY",FACE,{"derivedFrom":subQ1,"instanceName":"13"}),makeQuery(id+"F2.opPattern","COPY",FACE,{"derivedFrom":subQ1,"instanceName":"14"}),makeQuery(id+"F2.opPattern","COPY",FACE,{"derivedFrom":subQ1,"instanceName":"15"}),makeQuery(id+"F2.opPattern","COPY",FACE,{"derivedFrom":subQ1,"instanceName":"16"}),makeQuery(id+"F2.opPattern","COPY",FACE,{"derivedFrom":subQ1,"instanceName":"17"}),makeQuery(id+"F2.opPattern","COPY",FACE,{"derivedFrom":subQ1,"instanceName":"18"}),makeQuery(id+"F2.opPattern","COPY",FACE,{"derivedFrom":subQ1,"instanceName":"19"}),makeQuery(id+"F2.opPattern","COPY",FACE,{"derivedFrom":subQ1,"instanceName":"20"}),makeQuery(id+"F2.opPattern","COPY",FACE,{"derivedFrom":subQ1,"instanceName":"21"}),makeQuery(id+"F2.opPattern","COPY",FACE,{"derivedFrom":subQ1,"instanceName":"22"}),makeQuery(id+"F2.opPattern","COPY",FACE,{"derivedFrom":subQ1,"instanceName":"23"})]})]});}
            var Q43;
            {var subQ0=sQuery(id+"F0.wireOp",EDGE,"E12");var subQ1=makeQuery(id+"F1.opExtrude","CAP_FACE",FACE,{"disambiguationData":[OSD([sQuery(id+"F0.wireOp",EDGE,"E2"),sQuery(id+"F0.wireOp",EDGE,"E11"),subQ0,sQuery(id+"F0.wireOp",EDGE,"E13.MirrorCS"),sQuery(id+"F0.wireOp",EDGE,"E14.MirrorCS"),sQuery(id+"F0.wireOp",EDGE,"E15"),sQuery(id+"F0.wireOp",EDGE,"E19")])],"isStart":false});Q43=makeQuery(id+"F3.opFillet","BLEND_EDGE",EDGE,{"blendedFrom":[makeQuery(id+"F2.opPattern","COPY",EDGE,{"derivedFrom":makeQuery(id+"F1.opExtrude","CAP_EDGE",EDGE,{"disambiguationData":[OSD([subQ0])],"isStart":false}),"instanceName":"20"}),makeQuery(id+"F2.boolean.opBoolean","MERGE",FACE,{"derivedFrom":[subQ1,makeQuery(id+"F2.opPattern","COPY",FACE,{"derivedFrom":subQ1,"instanceName":"1"}),makeQuery(id+"F2.opPattern","COPY",FACE,{"derivedFrom":subQ1,"instanceName":"2"}),makeQuery(id+"F2.opPattern","COPY",FACE,{"derivedFrom":subQ1,"instanceName":"3"}),makeQuery(id+"F2.opPattern","COPY",FACE,{"derivedFrom":subQ1,"instanceName":"4"}),makeQuery(id+"F2.opPattern","COPY",FACE,{"derivedFrom":subQ1,"instanceName":"5"}),makeQuery(id+"F2.opPattern","COPY",FACE,{"derivedFrom":subQ1,"instanceName":"6"}),makeQuery(id+"F2.opPattern","COPY",FACE,{"derivedFrom":subQ1,"instanceName":"7"}),makeQuery(id+"F2.opPattern","COPY",FACE,{"derivedFrom":subQ1,"instanceName":"8"}),makeQuery(id+"F2.opPattern","COPY",FACE,{"derivedFrom":subQ1,"instanceName":"9"}),makeQuery(id+"F2.opPattern","COPY",FACE,{"derivedFrom":subQ1,"instanceName":"10"}),makeQuery(id+"F2.opPattern","COPY",FACE,{"derivedFrom":subQ1,"instanceName":"11"}),makeQuery(id+"F2.opPattern","COPY",FACE,{"derivedFrom":subQ1,"instanceName":"12"}),makeQuery(id+"F2.opPattern","COPY",FACE,{"derivedFrom":subQ1,"instanceName":"13"}),makeQuery(id+"F2.opPattern","COPY",FACE,{"derivedFrom":subQ1,"instanceName":"14"}),makeQuery(id+"F2.opPattern","COPY",FACE,{"derivedFrom":subQ1,"instanceName":"15"}),makeQuery(id+"F2.opPattern","COPY",FACE,{"derivedFrom":subQ1,"instanceName":"16"}),makeQuery(id+"F2.opPattern","COPY",FACE,{"derivedFrom":subQ1,"instanceName":"17"}),makeQuery(id+"F2.opPattern","COPY",FACE,{"derivedFrom":subQ1,"instanceName":"18"}),makeQuery(id+"F2.opPattern","COPY",FACE,{"derivedFrom":subQ1,"instanceName":"19"}),makeQuery(id+"F2.opPattern","COPY",FACE,{"derivedFrom":subQ1,"instanceName":"20"}),makeQuery(id+"F2.opPattern","COPY",FACE,{"derivedFrom":subQ1,"instanceName":"21"}),makeQuery(id+"F2.opPattern","COPY",FACE,{"derivedFrom":subQ1,"instanceName":"22"}),makeQuery(id+"F2.opPattern","COPY",FACE,{"derivedFrom":subQ1,"instanceName":"23"})]})],"blendedInto":[makeQuery(id+"F2.boolean.opBoolean","MERGE",FACE,{"derivedFrom":[subQ1,makeQuery(id+"F2.opPattern","COPY",FACE,{"derivedFrom":subQ1,"instanceName":"1"}),makeQuery(id+"F2.opPattern","COPY",FACE,{"derivedFrom":subQ1,"instanceName":"2"}),makeQuery(id+"F2.opPattern","COPY",FACE,{"derivedFrom":subQ1,"instanceName":"3"}),makeQuery(id+"F2.opPattern","COPY",FACE,{"derivedFrom":subQ1,"instanceName":"4"}),makeQuery(id+"F2.opPattern","COPY",FACE,{"derivedFrom":subQ1,"instanceName":"5"}),makeQuery(id+"F2.opPattern","COPY",FACE,{"derivedFrom":subQ1,"instanceName":"6"}),makeQuery(id+"F2.opPattern","COPY",FACE,{"derivedFrom":subQ1,"instanceName":"7"}),makeQuery(id+"F2.opPattern","COPY",FACE,{"derivedFrom":subQ1,"instanceName":"8"}),makeQuery(id+"F2.opPattern","COPY",FACE,{"derivedFrom":subQ1,"instanceName":"9"}),makeQuery(id+"F2.opPattern","COPY",FACE,{"derivedFrom":subQ1,"instanceName":"10"}),makeQuery(id+"F2.opPattern","COPY",FACE,{"derivedFrom":subQ1,"instanceName":"11"}),makeQuery(id+"F2.opPattern","COPY",FACE,{"derivedFrom":subQ1,"instanceName":"12"}),makeQuery(id+"F2.opPattern","COPY",FACE,{"derivedFrom":subQ1,"instanceName":"13"}),makeQuery(id+"F2.opPattern","COPY",FACE,{"derivedFrom":subQ1,"instanceName":"14"}),makeQuery(id+"F2.opPattern","COPY",FACE,{"derivedFrom":subQ1,"instanceName":"15"}),makeQuery(id+"F2.opPattern","COPY",FACE,{"derivedFrom":subQ1,"instanceName":"16"}),makeQuery(id+"F2.opPattern","COPY",FACE,{"derivedFrom":subQ1,"instanceName":"17"}),makeQuery(id+"F2.opPattern","COPY",FACE,{"derivedFrom":subQ1,"instanceName":"18"}),makeQuery(id+"F2.opPattern","COPY",FACE,{"derivedFrom":subQ1,"instanceName":"19"}),makeQuery(id+"F2.opPattern","COPY",FACE,{"derivedFrom":subQ1,"instanceName":"20"}),makeQuery(id+"F2.opPattern","COPY",FACE,{"derivedFrom":subQ1,"instanceName":"21"}),makeQuery(id+"F2.opPattern","COPY",FACE,{"derivedFrom":subQ1,"instanceName":"22"}),makeQuery(id+"F2.opPattern","COPY",FACE,{"derivedFrom":subQ1,"instanceName":"23"})]})]});}
            var Q44;
            {var subQ0=sQuery(id+"F0.wireOp",EDGE,"E14.MirrorCS");var subQ1=makeQuery(id+"F1.opExtrude","CAP_FACE",FACE,{"disambiguationData":[OSD([sQuery(id+"F0.wireOp",EDGE,"E2"),sQuery(id+"F0.wireOp",EDGE,"E11"),sQuery(id+"F0.wireOp",EDGE,"E12"),sQuery(id+"F0.wireOp",EDGE,"E13.MirrorCS"),subQ0,sQuery(id+"F0.wireOp",EDGE,"E15"),sQuery(id+"F0.wireOp",EDGE,"E19")])],"isStart":false});Q44=makeQuery(id+"F3.opFillet","BLEND_EDGE",EDGE,{"blendedFrom":[makeQuery(id+"F2.opPattern","COPY",EDGE,{"derivedFrom":makeQuery(id+"F1.opExtrude","CAP_EDGE",EDGE,{"disambiguationData":[OSD([subQ0])],"isStart":false}),"instanceName":"21"}),makeQuery(id+"F2.boolean.opBoolean","MERGE",FACE,{"derivedFrom":[subQ1,makeQuery(id+"F2.opPattern","COPY",FACE,{"derivedFrom":subQ1,"instanceName":"1"}),makeQuery(id+"F2.opPattern","COPY",FACE,{"derivedFrom":subQ1,"instanceName":"2"}),makeQuery(id+"F2.opPattern","COPY",FACE,{"derivedFrom":subQ1,"instanceName":"3"}),makeQuery(id+"F2.opPattern","COPY",FACE,{"derivedFrom":subQ1,"instanceName":"4"}),makeQuery(id+"F2.opPattern","COPY",FACE,{"derivedFrom":subQ1,"instanceName":"5"}),makeQuery(id+"F2.opPattern","COPY",FACE,{"derivedFrom":subQ1,"instanceName":"6"}),makeQuery(id+"F2.opPattern","COPY",FACE,{"derivedFrom":subQ1,"instanceName":"7"}),makeQuery(id+"F2.opPattern","COPY",FACE,{"derivedFrom":subQ1,"instanceName":"8"}),makeQuery(id+"F2.opPattern","COPY",FACE,{"derivedFrom":subQ1,"instanceName":"9"}),makeQuery(id+"F2.opPattern","COPY",FACE,{"derivedFrom":subQ1,"instanceName":"10"}),makeQuery(id+"F2.opPattern","COPY",FACE,{"derivedFrom":subQ1,"instanceName":"11"}),makeQuery(id+"F2.opPattern","COPY",FACE,{"derivedFrom":subQ1,"instanceName":"12"}),makeQuery(id+"F2.opPattern","COPY",FACE,{"derivedFrom":subQ1,"instanceName":"13"}),makeQuery(id+"F2.opPattern","COPY",FACE,{"derivedFrom":subQ1,"instanceName":"14"}),makeQuery(id+"F2.opPattern","COPY",FACE,{"derivedFrom":subQ1,"instanceName":"15"}),makeQuery(id+"F2.opPattern","COPY",FACE,{"derivedFrom":subQ1,"instanceName":"16"}),makeQuery(id+"F2.opPattern","COPY",FACE,{"derivedFrom":subQ1,"instanceName":"17"}),makeQuery(id+"F2.opPattern","COPY",FACE,{"derivedFrom":subQ1,"instanceName":"18"}),makeQuery(id+"F2.opPattern","COPY",FACE,{"derivedFrom":subQ1,"instanceName":"19"}),makeQuery(id+"F2.opPattern","COPY",FACE,{"derivedFrom":subQ1,"instanceName":"20"}),makeQuery(id+"F2.opPattern","COPY",FACE,{"derivedFrom":subQ1,"instanceName":"21"}),makeQuery(id+"F2.opPattern","COPY",FACE,{"derivedFrom":subQ1,"instanceName":"22"}),makeQuery(id+"F2.opPattern","COPY",FACE,{"derivedFrom":subQ1,"instanceName":"23"})]})],"blendedInto":[makeQuery(id+"F2.boolean.opBoolean","MERGE",FACE,{"derivedFrom":[subQ1,makeQuery(id+"F2.opPattern","COPY",FACE,{"derivedFrom":subQ1,"instanceName":"1"}),makeQuery(id+"F2.opPattern","COPY",FACE,{"derivedFrom":subQ1,"instanceName":"2"}),makeQuery(id+"F2.opPattern","COPY",FACE,{"derivedFrom":subQ1,"instanceName":"3"}),makeQuery(id+"F2.opPattern","COPY",FACE,{"derivedFrom":subQ1,"instanceName":"4"}),makeQuery(id+"F2.opPattern","COPY",FACE,{"derivedFrom":subQ1,"instanceName":"5"}),makeQuery(id+"F2.opPattern","COPY",FACE,{"derivedFrom":subQ1,"instanceName":"6"}),makeQuery(id+"F2.opPattern","COPY",FACE,{"derivedFrom":subQ1,"instanceName":"7"}),makeQuery(id+"F2.opPattern","COPY",FACE,{"derivedFrom":subQ1,"instanceName":"8"}),makeQuery(id+"F2.opPattern","COPY",FACE,{"derivedFrom":subQ1,"instanceName":"9"}),makeQuery(id+"F2.opPattern","COPY",FACE,{"derivedFrom":subQ1,"instanceName":"10"}),makeQuery(id+"F2.opPattern","COPY",FACE,{"derivedFrom":subQ1,"instanceName":"11"}),makeQuery(id+"F2.opPattern","COPY",FACE,{"derivedFrom":subQ1,"instanceName":"12"}),makeQuery(id+"F2.opPattern","COPY",FACE,{"derivedFrom":subQ1,"instanceName":"13"}),makeQuery(id+"F2.opPattern","COPY",FACE,{"derivedFrom":subQ1,"instanceName":"14"}),makeQuery(id+"F2.opPattern","COPY",FACE,{"derivedFrom":subQ1,"instanceName":"15"}),makeQuery(id+"F2.opPattern","COPY",FACE,{"derivedFrom":subQ1,"instanceName":"16"}),makeQuery(id+"F2.opPattern","COPY",FACE,{"derivedFrom":subQ1,"instanceName":"17"}),makeQuery(id+"F2.opPattern","COPY",FACE,{"derivedFrom":subQ1,"instanceName":"18"}),makeQuery(id+"F2.opPattern","COPY",FACE,{"derivedFrom":subQ1,"instanceName":"19"}),makeQuery(id+"F2.opPattern","COPY",FACE,{"derivedFrom":subQ1,"instanceName":"20"}),makeQuery(id+"F2.opPattern","COPY",FACE,{"derivedFrom":subQ1,"instanceName":"21"}),makeQuery(id+"F2.opPattern","COPY",FACE,{"derivedFrom":subQ1,"instanceName":"22"}),makeQuery(id+"F2.opPattern","COPY",FACE,{"derivedFrom":subQ1,"instanceName":"23"})]})]});}
            var Q45;
            {var subQ0=sQuery(id+"F0.wireOp",EDGE,"E12");var subQ1=makeQuery(id+"F1.opExtrude","CAP_FACE",FACE,{"disambiguationData":[OSD([sQuery(id+"F0.wireOp",EDGE,"E2"),sQuery(id+"F0.wireOp",EDGE,"E11"),subQ0,sQuery(id+"F0.wireOp",EDGE,"E13.MirrorCS"),sQuery(id+"F0.wireOp",EDGE,"E14.MirrorCS"),sQuery(id+"F0.wireOp",EDGE,"E15"),sQuery(id+"F0.wireOp",EDGE,"E19")])],"isStart":false});Q45=makeQuery(id+"F3.opFillet","BLEND_EDGE",EDGE,{"blendedFrom":[makeQuery(id+"F2.opPattern","COPY",EDGE,{"derivedFrom":makeQuery(id+"F1.opExtrude","CAP_EDGE",EDGE,{"disambiguationData":[OSD([subQ0])],"isStart":false}),"instanceName":"21"}),makeQuery(id+"F2.boolean.opBoolean","MERGE",FACE,{"derivedFrom":[subQ1,makeQuery(id+"F2.opPattern","COPY",FACE,{"derivedFrom":subQ1,"instanceName":"1"}),makeQuery(id+"F2.opPattern","COPY",FACE,{"derivedFrom":subQ1,"instanceName":"2"}),makeQuery(id+"F2.opPattern","COPY",FACE,{"derivedFrom":subQ1,"instanceName":"3"}),makeQuery(id+"F2.opPattern","COPY",FACE,{"derivedFrom":subQ1,"instanceName":"4"}),makeQuery(id+"F2.opPattern","COPY",FACE,{"derivedFrom":subQ1,"instanceName":"5"}),makeQuery(id+"F2.opPattern","COPY",FACE,{"derivedFrom":subQ1,"instanceName":"6"}),makeQuery(id+"F2.opPattern","COPY",FACE,{"derivedFrom":subQ1,"instanceName":"7"}),makeQuery(id+"F2.opPattern","COPY",FACE,{"derivedFrom":subQ1,"instanceName":"8"}),makeQuery(id+"F2.opPattern","COPY",FACE,{"derivedFrom":subQ1,"instanceName":"9"}),makeQuery(id+"F2.opPattern","COPY",FACE,{"derivedFrom":subQ1,"instanceName":"10"}),makeQuery(id+"F2.opPattern","COPY",FACE,{"derivedFrom":subQ1,"instanceName":"11"}),makeQuery(id+"F2.opPattern","COPY",FACE,{"derivedFrom":subQ1,"instanceName":"12"}),makeQuery(id+"F2.opPattern","COPY",FACE,{"derivedFrom":subQ1,"instanceName":"13"}),makeQuery(id+"F2.opPattern","COPY",FACE,{"derivedFrom":subQ1,"instanceName":"14"}),makeQuery(id+"F2.opPattern","COPY",FACE,{"derivedFrom":subQ1,"instanceName":"15"}),makeQuery(id+"F2.opPattern","COPY",FACE,{"derivedFrom":subQ1,"instanceName":"16"}),makeQuery(id+"F2.opPattern","COPY",FACE,{"derivedFrom":subQ1,"instanceName":"17"}),makeQuery(id+"F2.opPattern","COPY",FACE,{"derivedFrom":subQ1,"instanceName":"18"}),makeQuery(id+"F2.opPattern","COPY",FACE,{"derivedFrom":subQ1,"instanceName":"19"}),makeQuery(id+"F2.opPattern","COPY",FACE,{"derivedFrom":subQ1,"instanceName":"20"}),makeQuery(id+"F2.opPattern","COPY",FACE,{"derivedFrom":subQ1,"instanceName":"21"}),makeQuery(id+"F2.opPattern","COPY",FACE,{"derivedFrom":subQ1,"instanceName":"22"}),makeQuery(id+"F2.opPattern","COPY",FACE,{"derivedFrom":subQ1,"instanceName":"23"})]})],"blendedInto":[makeQuery(id+"F2.boolean.opBoolean","MERGE",FACE,{"derivedFrom":[subQ1,makeQuery(id+"F2.opPattern","COPY",FACE,{"derivedFrom":subQ1,"instanceName":"1"}),makeQuery(id+"F2.opPattern","COPY",FACE,{"derivedFrom":subQ1,"instanceName":"2"}),makeQuery(id+"F2.opPattern","COPY",FACE,{"derivedFrom":subQ1,"instanceName":"3"}),makeQuery(id+"F2.opPattern","COPY",FACE,{"derivedFrom":subQ1,"instanceName":"4"}),makeQuery(id+"F2.opPattern","COPY",FACE,{"derivedFrom":subQ1,"instanceName":"5"}),makeQuery(id+"F2.opPattern","COPY",FACE,{"derivedFrom":subQ1,"instanceName":"6"}),makeQuery(id+"F2.opPattern","COPY",FACE,{"derivedFrom":subQ1,"instanceName":"7"}),makeQuery(id+"F2.opPattern","COPY",FACE,{"derivedFrom":subQ1,"instanceName":"8"}),makeQuery(id+"F2.opPattern","COPY",FACE,{"derivedFrom":subQ1,"instanceName":"9"}),makeQuery(id+"F2.opPattern","COPY",FACE,{"derivedFrom":subQ1,"instanceName":"10"}),makeQuery(id+"F2.opPattern","COPY",FACE,{"derivedFrom":subQ1,"instanceName":"11"}),makeQuery(id+"F2.opPattern","COPY",FACE,{"derivedFrom":subQ1,"instanceName":"12"}),makeQuery(id+"F2.opPattern","COPY",FACE,{"derivedFrom":subQ1,"instanceName":"13"}),makeQuery(id+"F2.opPattern","COPY",FACE,{"derivedFrom":subQ1,"instanceName":"14"}),makeQuery(id+"F2.opPattern","COPY",FACE,{"derivedFrom":subQ1,"instanceName":"15"}),makeQuery(id+"F2.opPattern","COPY",FACE,{"derivedFrom":subQ1,"instanceName":"16"}),makeQuery(id+"F2.opPattern","COPY",FACE,{"derivedFrom":subQ1,"instanceName":"17"}),makeQuery(id+"F2.opPattern","COPY",FACE,{"derivedFrom":subQ1,"instanceName":"18"}),makeQuery(id+"F2.opPattern","COPY",FACE,{"derivedFrom":subQ1,"instanceName":"19"}),makeQuery(id+"F2.opPattern","COPY",FACE,{"derivedFrom":subQ1,"instanceName":"20"}),makeQuery(id+"F2.opPattern","COPY",FACE,{"derivedFrom":subQ1,"instanceName":"21"}),makeQuery(id+"F2.opPattern","COPY",FACE,{"derivedFrom":subQ1,"instanceName":"22"}),makeQuery(id+"F2.opPattern","COPY",FACE,{"derivedFrom":subQ1,"instanceName":"23"})]})]});}
            var Q46;
            {var subQ0=sQuery(id+"F0.wireOp",EDGE,"E14.MirrorCS");var subQ1=makeQuery(id+"F1.opExtrude","CAP_FACE",FACE,{"disambiguationData":[OSD([sQuery(id+"F0.wireOp",EDGE,"E2"),sQuery(id+"F0.wireOp",EDGE,"E11"),sQuery(id+"F0.wireOp",EDGE,"E12"),sQuery(id+"F0.wireOp",EDGE,"E13.MirrorCS"),subQ0,sQuery(id+"F0.wireOp",EDGE,"E15"),sQuery(id+"F0.wireOp",EDGE,"E19")])],"isStart":false});Q46=makeQuery(id+"F3.opFillet","BLEND_EDGE",EDGE,{"blendedFrom":[makeQuery(id+"F2.opPattern","COPY",EDGE,{"derivedFrom":makeQuery(id+"F1.opExtrude","CAP_EDGE",EDGE,{"disambiguationData":[OSD([subQ0])],"isStart":false}),"instanceName":"22"}),makeQuery(id+"F2.boolean.opBoolean","MERGE",FACE,{"derivedFrom":[subQ1,makeQuery(id+"F2.opPattern","COPY",FACE,{"derivedFrom":subQ1,"instanceName":"1"}),makeQuery(id+"F2.opPattern","COPY",FACE,{"derivedFrom":subQ1,"instanceName":"2"}),makeQuery(id+"F2.opPattern","COPY",FACE,{"derivedFrom":subQ1,"instanceName":"3"}),makeQuery(id+"F2.opPattern","COPY",FACE,{"derivedFrom":subQ1,"instanceName":"4"}),makeQuery(id+"F2.opPattern","COPY",FACE,{"derivedFrom":subQ1,"instanceName":"5"}),makeQuery(id+"F2.opPattern","COPY",FACE,{"derivedFrom":subQ1,"instanceName":"6"}),makeQuery(id+"F2.opPattern","COPY",FACE,{"derivedFrom":subQ1,"instanceName":"7"}),makeQuery(id+"F2.opPattern","COPY",FACE,{"derivedFrom":subQ1,"instanceName":"8"}),makeQuery(id+"F2.opPattern","COPY",FACE,{"derivedFrom":subQ1,"instanceName":"9"}),makeQuery(id+"F2.opPattern","COPY",FACE,{"derivedFrom":subQ1,"instanceName":"10"}),makeQuery(id+"F2.opPattern","COPY",FACE,{"derivedFrom":subQ1,"instanceName":"11"}),makeQuery(id+"F2.opPattern","COPY",FACE,{"derivedFrom":subQ1,"instanceName":"12"}),makeQuery(id+"F2.opPattern","COPY",FACE,{"derivedFrom":subQ1,"instanceName":"13"}),makeQuery(id+"F2.opPattern","COPY",FACE,{"derivedFrom":subQ1,"instanceName":"14"}),makeQuery(id+"F2.opPattern","COPY",FACE,{"derivedFrom":subQ1,"instanceName":"15"}),makeQuery(id+"F2.opPattern","COPY",FACE,{"derivedFrom":subQ1,"instanceName":"16"}),makeQuery(id+"F2.opPattern","COPY",FACE,{"derivedFrom":subQ1,"instanceName":"17"}),makeQuery(id+"F2.opPattern","COPY",FACE,{"derivedFrom":subQ1,"instanceName":"18"}),makeQuery(id+"F2.opPattern","COPY",FACE,{"derivedFrom":subQ1,"instanceName":"19"}),makeQuery(id+"F2.opPattern","COPY",FACE,{"derivedFrom":subQ1,"instanceName":"20"}),makeQuery(id+"F2.opPattern","COPY",FACE,{"derivedFrom":subQ1,"instanceName":"21"}),makeQuery(id+"F2.opPattern","COPY",FACE,{"derivedFrom":subQ1,"instanceName":"22"}),makeQuery(id+"F2.opPattern","COPY",FACE,{"derivedFrom":subQ1,"instanceName":"23"})]})],"blendedInto":[makeQuery(id+"F2.boolean.opBoolean","MERGE",FACE,{"derivedFrom":[subQ1,makeQuery(id+"F2.opPattern","COPY",FACE,{"derivedFrom":subQ1,"instanceName":"1"}),makeQuery(id+"F2.opPattern","COPY",FACE,{"derivedFrom":subQ1,"instanceName":"2"}),makeQuery(id+"F2.opPattern","COPY",FACE,{"derivedFrom":subQ1,"instanceName":"3"}),makeQuery(id+"F2.opPattern","COPY",FACE,{"derivedFrom":subQ1,"instanceName":"4"}),makeQuery(id+"F2.opPattern","COPY",FACE,{"derivedFrom":subQ1,"instanceName":"5"}),makeQuery(id+"F2.opPattern","COPY",FACE,{"derivedFrom":subQ1,"instanceName":"6"}),makeQuery(id+"F2.opPattern","COPY",FACE,{"derivedFrom":subQ1,"instanceName":"7"}),makeQuery(id+"F2.opPattern","COPY",FACE,{"derivedFrom":subQ1,"instanceName":"8"}),makeQuery(id+"F2.opPattern","COPY",FACE,{"derivedFrom":subQ1,"instanceName":"9"}),makeQuery(id+"F2.opPattern","COPY",FACE,{"derivedFrom":subQ1,"instanceName":"10"}),makeQuery(id+"F2.opPattern","COPY",FACE,{"derivedFrom":subQ1,"instanceName":"11"}),makeQuery(id+"F2.opPattern","COPY",FACE,{"derivedFrom":subQ1,"instanceName":"12"}),makeQuery(id+"F2.opPattern","COPY",FACE,{"derivedFrom":subQ1,"instanceName":"13"}),makeQuery(id+"F2.opPattern","COPY",FACE,{"derivedFrom":subQ1,"instanceName":"14"}),makeQuery(id+"F2.opPattern","COPY",FACE,{"derivedFrom":subQ1,"instanceName":"15"}),makeQuery(id+"F2.opPattern","COPY",FACE,{"derivedFrom":subQ1,"instanceName":"16"}),makeQuery(id+"F2.opPattern","COPY",FACE,{"derivedFrom":subQ1,"instanceName":"17"}),makeQuery(id+"F2.opPattern","COPY",FACE,{"derivedFrom":subQ1,"instanceName":"18"}),makeQuery(id+"F2.opPattern","COPY",FACE,{"derivedFrom":subQ1,"instanceName":"19"}),makeQuery(id+"F2.opPattern","COPY",FACE,{"derivedFrom":subQ1,"instanceName":"20"}),makeQuery(id+"F2.opPattern","COPY",FACE,{"derivedFrom":subQ1,"instanceName":"21"}),makeQuery(id+"F2.opPattern","COPY",FACE,{"derivedFrom":subQ1,"instanceName":"22"}),makeQuery(id+"F2.opPattern","COPY",FACE,{"derivedFrom":subQ1,"instanceName":"23"})]})]});}
            var Q47;
            {var subQ0=sQuery(id+"F0.wireOp",EDGE,"E12");var subQ1=makeQuery(id+"F1.opExtrude","CAP_FACE",FACE,{"disambiguationData":[OSD([sQuery(id+"F0.wireOp",EDGE,"E2"),sQuery(id+"F0.wireOp",EDGE,"E11"),subQ0,sQuery(id+"F0.wireOp",EDGE,"E13.MirrorCS"),sQuery(id+"F0.wireOp",EDGE,"E14.MirrorCS"),sQuery(id+"F0.wireOp",EDGE,"E15"),sQuery(id+"F0.wireOp",EDGE,"E19")])],"isStart":false});Q47=makeQuery(id+"F3.opFillet","BLEND_EDGE",EDGE,{"blendedFrom":[makeQuery(id+"F2.opPattern","COPY",EDGE,{"derivedFrom":makeQuery(id+"F1.opExtrude","CAP_EDGE",EDGE,{"disambiguationData":[OSD([subQ0])],"isStart":false}),"instanceName":"22"}),makeQuery(id+"F2.boolean.opBoolean","MERGE",FACE,{"derivedFrom":[subQ1,makeQuery(id+"F2.opPattern","COPY",FACE,{"derivedFrom":subQ1,"instanceName":"1"}),makeQuery(id+"F2.opPattern","COPY",FACE,{"derivedFrom":subQ1,"instanceName":"2"}),makeQuery(id+"F2.opPattern","COPY",FACE,{"derivedFrom":subQ1,"instanceName":"3"}),makeQuery(id+"F2.opPattern","COPY",FACE,{"derivedFrom":subQ1,"instanceName":"4"}),makeQuery(id+"F2.opPattern","COPY",FACE,{"derivedFrom":subQ1,"instanceName":"5"}),makeQuery(id+"F2.opPattern","COPY",FACE,{"derivedFrom":subQ1,"instanceName":"6"}),makeQuery(id+"F2.opPattern","COPY",FACE,{"derivedFrom":subQ1,"instanceName":"7"}),makeQuery(id+"F2.opPattern","COPY",FACE,{"derivedFrom":subQ1,"instanceName":"8"}),makeQuery(id+"F2.opPattern","COPY",FACE,{"derivedFrom":subQ1,"instanceName":"9"}),makeQuery(id+"F2.opPattern","COPY",FACE,{"derivedFrom":subQ1,"instanceName":"10"}),makeQuery(id+"F2.opPattern","COPY",FACE,{"derivedFrom":subQ1,"instanceName":"11"}),makeQuery(id+"F2.opPattern","COPY",FACE,{"derivedFrom":subQ1,"instanceName":"12"}),makeQuery(id+"F2.opPattern","COPY",FACE,{"derivedFrom":subQ1,"instanceName":"13"}),makeQuery(id+"F2.opPattern","COPY",FACE,{"derivedFrom":subQ1,"instanceName":"14"}),makeQuery(id+"F2.opPattern","COPY",FACE,{"derivedFrom":subQ1,"instanceName":"15"}),makeQuery(id+"F2.opPattern","COPY",FACE,{"derivedFrom":subQ1,"instanceName":"16"}),makeQuery(id+"F2.opPattern","COPY",FACE,{"derivedFrom":subQ1,"instanceName":"17"}),makeQuery(id+"F2.opPattern","COPY",FACE,{"derivedFrom":subQ1,"instanceName":"18"}),makeQuery(id+"F2.opPattern","COPY",FACE,{"derivedFrom":subQ1,"instanceName":"19"}),makeQuery(id+"F2.opPattern","COPY",FACE,{"derivedFrom":subQ1,"instanceName":"20"}),makeQuery(id+"F2.opPattern","COPY",FACE,{"derivedFrom":subQ1,"instanceName":"21"}),makeQuery(id+"F2.opPattern","COPY",FACE,{"derivedFrom":subQ1,"instanceName":"22"}),makeQuery(id+"F2.opPattern","COPY",FACE,{"derivedFrom":subQ1,"instanceName":"23"})]})],"blendedInto":[makeQuery(id+"F2.boolean.opBoolean","MERGE",FACE,{"derivedFrom":[subQ1,makeQuery(id+"F2.opPattern","COPY",FACE,{"derivedFrom":subQ1,"instanceName":"1"}),makeQuery(id+"F2.opPattern","COPY",FACE,{"derivedFrom":subQ1,"instanceName":"2"}),makeQuery(id+"F2.opPattern","COPY",FACE,{"derivedFrom":subQ1,"instanceName":"3"}),makeQuery(id+"F2.opPattern","COPY",FACE,{"derivedFrom":subQ1,"instanceName":"4"}),makeQuery(id+"F2.opPattern","COPY",FACE,{"derivedFrom":subQ1,"instanceName":"5"}),makeQuery(id+"F2.opPattern","COPY",FACE,{"derivedFrom":subQ1,"instanceName":"6"}),makeQuery(id+"F2.opPattern","COPY",FACE,{"derivedFrom":subQ1,"instanceName":"7"}),makeQuery(id+"F2.opPattern","COPY",FACE,{"derivedFrom":subQ1,"instanceName":"8"}),makeQuery(id+"F2.opPattern","COPY",FACE,{"derivedFrom":subQ1,"instanceName":"9"}),makeQuery(id+"F2.opPattern","COPY",FACE,{"derivedFrom":subQ1,"instanceName":"10"}),makeQuery(id+"F2.opPattern","COPY",FACE,{"derivedFrom":subQ1,"instanceName":"11"}),makeQuery(id+"F2.opPattern","COPY",FACE,{"derivedFrom":subQ1,"instanceName":"12"}),makeQuery(id+"F2.opPattern","COPY",FACE,{"derivedFrom":subQ1,"instanceName":"13"}),makeQuery(id+"F2.opPattern","COPY",FACE,{"derivedFrom":subQ1,"instanceName":"14"}),makeQuery(id+"F2.opPattern","COPY",FACE,{"derivedFrom":subQ1,"instanceName":"15"}),makeQuery(id+"F2.opPattern","COPY",FACE,{"derivedFrom":subQ1,"instanceName":"16"}),makeQuery(id+"F2.opPattern","COPY",FACE,{"derivedFrom":subQ1,"instanceName":"17"}),makeQuery(id+"F2.opPattern","COPY",FACE,{"derivedFrom":subQ1,"instanceName":"18"}),makeQuery(id+"F2.opPattern","COPY",FACE,{"derivedFrom":subQ1,"instanceName":"19"}),makeQuery(id+"F2.opPattern","COPY",FACE,{"derivedFrom":subQ1,"instanceName":"20"}),makeQuery(id+"F2.opPattern","COPY",FACE,{"derivedFrom":subQ1,"instanceName":"21"}),makeQuery(id+"F2.opPattern","COPY",FACE,{"derivedFrom":subQ1,"instanceName":"22"}),makeQuery(id+"F2.opPattern","COPY",FACE,{"derivedFrom":subQ1,"instanceName":"23"})]})]});}
            var Q48;
            {var subQ0=sQuery(id+"F0.wireOp",EDGE,"E14.MirrorCS");var subQ1=makeQuery(id+"F1.opExtrude","CAP_FACE",FACE,{"disambiguationData":[OSD([sQuery(id+"F0.wireOp",EDGE,"E2"),sQuery(id+"F0.wireOp",EDGE,"E11"),sQuery(id+"F0.wireOp",EDGE,"E12"),sQuery(id+"F0.wireOp",EDGE,"E13.MirrorCS"),subQ0,sQuery(id+"F0.wireOp",EDGE,"E15"),sQuery(id+"F0.wireOp",EDGE,"E19")])],"isStart":false});Q48=makeQuery(id+"F3.opFillet","BLEND_EDGE",EDGE,{"blendedFrom":[makeQuery(id+"F2.opPattern","COPY",EDGE,{"derivedFrom":makeQuery(id+"F1.opExtrude","CAP_EDGE",EDGE,{"disambiguationData":[OSD([subQ0])],"isStart":false}),"instanceName":"23"}),makeQuery(id+"F2.boolean.opBoolean","MERGE",FACE,{"derivedFrom":[subQ1,makeQuery(id+"F2.opPattern","COPY",FACE,{"derivedFrom":subQ1,"instanceName":"1"}),makeQuery(id+"F2.opPattern","COPY",FACE,{"derivedFrom":subQ1,"instanceName":"2"}),makeQuery(id+"F2.opPattern","COPY",FACE,{"derivedFrom":subQ1,"instanceName":"3"}),makeQuery(id+"F2.opPattern","COPY",FACE,{"derivedFrom":subQ1,"instanceName":"4"}),makeQuery(id+"F2.opPattern","COPY",FACE,{"derivedFrom":subQ1,"instanceName":"5"}),makeQuery(id+"F2.opPattern","COPY",FACE,{"derivedFrom":subQ1,"instanceName":"6"}),makeQuery(id+"F2.opPattern","COPY",FACE,{"derivedFrom":subQ1,"instanceName":"7"}),makeQuery(id+"F2.opPattern","COPY",FACE,{"derivedFrom":subQ1,"instanceName":"8"}),makeQuery(id+"F2.opPattern","COPY",FACE,{"derivedFrom":subQ1,"instanceName":"9"}),makeQuery(id+"F2.opPattern","COPY",FACE,{"derivedFrom":subQ1,"instanceName":"10"}),makeQuery(id+"F2.opPattern","COPY",FACE,{"derivedFrom":subQ1,"instanceName":"11"}),makeQuery(id+"F2.opPattern","COPY",FACE,{"derivedFrom":subQ1,"instanceName":"12"}),makeQuery(id+"F2.opPattern","COPY",FACE,{"derivedFrom":subQ1,"instanceName":"13"}),makeQuery(id+"F2.opPattern","COPY",FACE,{"derivedFrom":subQ1,"instanceName":"14"}),makeQuery(id+"F2.opPattern","COPY",FACE,{"derivedFrom":subQ1,"instanceName":"15"}),makeQuery(id+"F2.opPattern","COPY",FACE,{"derivedFrom":subQ1,"instanceName":"16"}),makeQuery(id+"F2.opPattern","COPY",FACE,{"derivedFrom":subQ1,"instanceName":"17"}),makeQuery(id+"F2.opPattern","COPY",FACE,{"derivedFrom":subQ1,"instanceName":"18"}),makeQuery(id+"F2.opPattern","COPY",FACE,{"derivedFrom":subQ1,"instanceName":"19"}),makeQuery(id+"F2.opPattern","COPY",FACE,{"derivedFrom":subQ1,"instanceName":"20"}),makeQuery(id+"F2.opPattern","COPY",FACE,{"derivedFrom":subQ1,"instanceName":"21"}),makeQuery(id+"F2.opPattern","COPY",FACE,{"derivedFrom":subQ1,"instanceName":"22"}),makeQuery(id+"F2.opPattern","COPY",FACE,{"derivedFrom":subQ1,"instanceName":"23"})]})],"blendedInto":[makeQuery(id+"F2.boolean.opBoolean","MERGE",FACE,{"derivedFrom":[subQ1,makeQuery(id+"F2.opPattern","COPY",FACE,{"derivedFrom":subQ1,"instanceName":"1"}),makeQuery(id+"F2.opPattern","COPY",FACE,{"derivedFrom":subQ1,"instanceName":"2"}),makeQuery(id+"F2.opPattern","COPY",FACE,{"derivedFrom":subQ1,"instanceName":"3"}),makeQuery(id+"F2.opPattern","COPY",FACE,{"derivedFrom":subQ1,"instanceName":"4"}),makeQuery(id+"F2.opPattern","COPY",FACE,{"derivedFrom":subQ1,"instanceName":"5"}),makeQuery(id+"F2.opPattern","COPY",FACE,{"derivedFrom":subQ1,"instanceName":"6"}),makeQuery(id+"F2.opPattern","COPY",FACE,{"derivedFrom":subQ1,"instanceName":"7"}),makeQuery(id+"F2.opPattern","COPY",FACE,{"derivedFrom":subQ1,"instanceName":"8"}),makeQuery(id+"F2.opPattern","COPY",FACE,{"derivedFrom":subQ1,"instanceName":"9"}),makeQuery(id+"F2.opPattern","COPY",FACE,{"derivedFrom":subQ1,"instanceName":"10"}),makeQuery(id+"F2.opPattern","COPY",FACE,{"derivedFrom":subQ1,"instanceName":"11"}),makeQuery(id+"F2.opPattern","COPY",FACE,{"derivedFrom":subQ1,"instanceName":"12"}),makeQuery(id+"F2.opPattern","COPY",FACE,{"derivedFrom":subQ1,"instanceName":"13"}),makeQuery(id+"F2.opPattern","COPY",FACE,{"derivedFrom":subQ1,"instanceName":"14"}),makeQuery(id+"F2.opPattern","COPY",FACE,{"derivedFrom":subQ1,"instanceName":"15"}),makeQuery(id+"F2.opPattern","COPY",FACE,{"derivedFrom":subQ1,"instanceName":"16"}),makeQuery(id+"F2.opPattern","COPY",FACE,{"derivedFrom":subQ1,"instanceName":"17"}),makeQuery(id+"F2.opPattern","COPY",FACE,{"derivedFrom":subQ1,"instanceName":"18"}),makeQuery(id+"F2.opPattern","COPY",FACE,{"derivedFrom":subQ1,"instanceName":"19"}),makeQuery(id+"F2.opPattern","COPY",FACE,{"derivedFrom":subQ1,"instanceName":"20"}),makeQuery(id+"F2.opPattern","COPY",FACE,{"derivedFrom":subQ1,"instanceName":"21"}),makeQuery(id+"F2.opPattern","COPY",FACE,{"derivedFrom":subQ1,"instanceName":"22"}),makeQuery(id+"F2.opPattern","COPY",FACE,{"derivedFrom":subQ1,"instanceName":"23"})]})]});}
            var Q49;
            {var subQ0=sQuery(id+"F0.wireOp",EDGE,"E12");var subQ1=makeQuery(id+"F1.opExtrude","CAP_FACE",FACE,{"disambiguationData":[OSD([sQuery(id+"F0.wireOp",EDGE,"E2"),sQuery(id+"F0.wireOp",EDGE,"E11"),subQ0,sQuery(id+"F0.wireOp",EDGE,"E13.MirrorCS"),sQuery(id+"F0.wireOp",EDGE,"E14.MirrorCS"),sQuery(id+"F0.wireOp",EDGE,"E15"),sQuery(id+"F0.wireOp",EDGE,"E19")])],"isStart":false});Q49=makeQuery(id+"F3.opFillet","BLEND_EDGE",EDGE,{"blendedFrom":[makeQuery(id+"F2.opPattern","COPY",EDGE,{"derivedFrom":makeQuery(id+"F1.opExtrude","CAP_EDGE",EDGE,{"disambiguationData":[OSD([subQ0])],"isStart":false}),"instanceName":"23"}),makeQuery(id+"F2.boolean.opBoolean","MERGE",FACE,{"derivedFrom":[subQ1,makeQuery(id+"F2.opPattern","COPY",FACE,{"derivedFrom":subQ1,"instanceName":"1"}),makeQuery(id+"F2.opPattern","COPY",FACE,{"derivedFrom":subQ1,"instanceName":"2"}),makeQuery(id+"F2.opPattern","COPY",FACE,{"derivedFrom":subQ1,"instanceName":"3"}),makeQuery(id+"F2.opPattern","COPY",FACE,{"derivedFrom":subQ1,"instanceName":"4"}),makeQuery(id+"F2.opPattern","COPY",FACE,{"derivedFrom":subQ1,"instanceName":"5"}),makeQuery(id+"F2.opPattern","COPY",FACE,{"derivedFrom":subQ1,"instanceName":"6"}),makeQuery(id+"F2.opPattern","COPY",FACE,{"derivedFrom":subQ1,"instanceName":"7"}),makeQuery(id+"F2.opPattern","COPY",FACE,{"derivedFrom":subQ1,"instanceName":"8"}),makeQuery(id+"F2.opPattern","COPY",FACE,{"derivedFrom":subQ1,"instanceName":"9"}),makeQuery(id+"F2.opPattern","COPY",FACE,{"derivedFrom":subQ1,"instanceName":"10"}),makeQuery(id+"F2.opPattern","COPY",FACE,{"derivedFrom":subQ1,"instanceName":"11"}),makeQuery(id+"F2.opPattern","COPY",FACE,{"derivedFrom":subQ1,"instanceName":"12"}),makeQuery(id+"F2.opPattern","COPY",FACE,{"derivedFrom":subQ1,"instanceName":"13"}),makeQuery(id+"F2.opPattern","COPY",FACE,{"derivedFrom":subQ1,"instanceName":"14"}),makeQuery(id+"F2.opPattern","COPY",FACE,{"derivedFrom":subQ1,"instanceName":"15"}),makeQuery(id+"F2.opPattern","COPY",FACE,{"derivedFrom":subQ1,"instanceName":"16"}),makeQuery(id+"F2.opPattern","COPY",FACE,{"derivedFrom":subQ1,"instanceName":"17"}),makeQuery(id+"F2.opPattern","COPY",FACE,{"derivedFrom":subQ1,"instanceName":"18"}),makeQuery(id+"F2.opPattern","COPY",FACE,{"derivedFrom":subQ1,"instanceName":"19"}),makeQuery(id+"F2.opPattern","COPY",FACE,{"derivedFrom":subQ1,"instanceName":"20"}),makeQuery(id+"F2.opPattern","COPY",FACE,{"derivedFrom":subQ1,"instanceName":"21"}),makeQuery(id+"F2.opPattern","COPY",FACE,{"derivedFrom":subQ1,"instanceName":"22"}),makeQuery(id+"F2.opPattern","COPY",FACE,{"derivedFrom":subQ1,"instanceName":"23"})]})],"blendedInto":[makeQuery(id+"F2.boolean.opBoolean","MERGE",FACE,{"derivedFrom":[subQ1,makeQuery(id+"F2.opPattern","COPY",FACE,{"derivedFrom":subQ1,"instanceName":"1"}),makeQuery(id+"F2.opPattern","COPY",FACE,{"derivedFrom":subQ1,"instanceName":"2"}),makeQuery(id+"F2.opPattern","COPY",FACE,{"derivedFrom":subQ1,"instanceName":"3"}),makeQuery(id+"F2.opPattern","COPY",FACE,{"derivedFrom":subQ1,"instanceName":"4"}),makeQuery(id+"F2.opPattern","COPY",FACE,{"derivedFrom":subQ1,"instanceName":"5"}),makeQuery(id+"F2.opPattern","COPY",FACE,{"derivedFrom":subQ1,"instanceName":"6"}),makeQuery(id+"F2.opPattern","COPY",FACE,{"derivedFrom":subQ1,"instanceName":"7"}),makeQuery(id+"F2.opPattern","COPY",FACE,{"derivedFrom":subQ1,"instanceName":"8"}),makeQuery(id+"F2.opPattern","COPY",FACE,{"derivedFrom":subQ1,"instanceName":"9"}),makeQuery(id+"F2.opPattern","COPY",FACE,{"derivedFrom":subQ1,"instanceName":"10"}),makeQuery(id+"F2.opPattern","COPY",FACE,{"derivedFrom":subQ1,"instanceName":"11"}),makeQuery(id+"F2.opPattern","COPY",FACE,{"derivedFrom":subQ1,"instanceName":"12"}),makeQuery(id+"F2.opPattern","COPY",FACE,{"derivedFrom":subQ1,"instanceName":"13"}),makeQuery(id+"F2.opPattern","COPY",FACE,{"derivedFrom":subQ1,"instanceName":"14"}),makeQuery(id+"F2.opPattern","COPY",FACE,{"derivedFrom":subQ1,"instanceName":"15"}),makeQuery(id+"F2.opPattern","COPY",FACE,{"derivedFrom":subQ1,"instanceName":"16"}),makeQuery(id+"F2.opPattern","COPY",FACE,{"derivedFrom":subQ1,"instanceName":"17"}),makeQuery(id+"F2.opPattern","COPY",FACE,{"derivedFrom":subQ1,"instanceName":"18"}),makeQuery(id+"F2.opPattern","COPY",FACE,{"derivedFrom":subQ1,"instanceName":"19"}),makeQuery(id+"F2.opPattern","COPY",FACE,{"derivedFrom":subQ1,"instanceName":"20"}),makeQuery(id+"F2.opPattern","COPY",FACE,{"derivedFrom":subQ1,"instanceName":"21"}),makeQuery(id+"F2.opPattern","COPY",FACE,{"derivedFrom":subQ1,"instanceName":"22"}),makeQuery(id+"F2.opPattern","COPY",FACE,{"derivedFrom":subQ1,"instanceName":"23"})]})]});}
            chamfer(context, id + "F6", {"entities" : qUnion([Q0, Q1, Q2, Q3, Q4, Q5, Q6, Q7, Q8, Q9, Q10, Q11, Q12, Q13, Q14, Q15, Q16, Q17, Q18, Q19, Q20, Q21, Q22, Q23, Q24, Q25, Q26, Q27, Q28, Q29, Q30, Q31, Q32, Q33, Q34, Q35, Q36, Q37, Q38, Q39, Q40, Q41, Q42, Q43, Q44, Q45, Q46, Q47, Q48, Q49]), "width" : 2 * mm, "tangentPropagation" : true});
        }
    });
